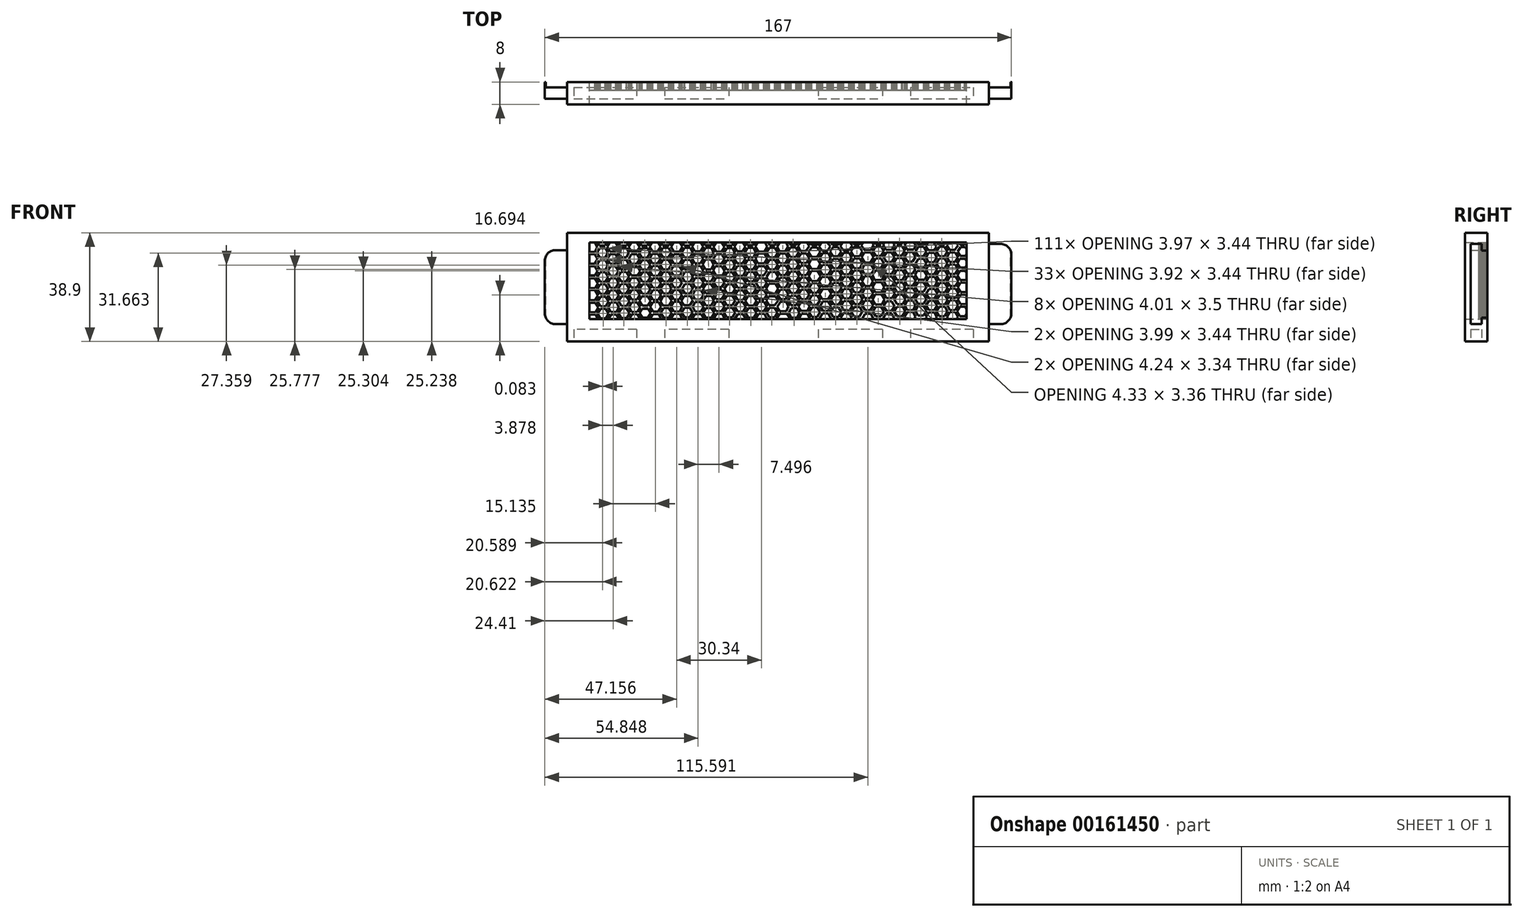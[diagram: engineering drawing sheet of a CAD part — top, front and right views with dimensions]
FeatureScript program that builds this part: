
annotation { "Feature Type Name" : "Feature", "Feature Type Description" : "" }
export const myFeature = defineFeature(function(context is Context, id is Id, definition is map)
    precondition{}
    {
        {
            var Q0;
            Q0=qCreatedBy(makeId("Front.planeOp"),FACE);
            var sketch = newSketch(context, id + "F0", { "sketchPlane" : qUnion([Q0])});
            skLineSegment(sketch, "E0.bottom", {"start": v(-77.72, 39.57) * mm, "end": v(73.28, 39.57) * mm});
            skLineSegment(sketch, "E0.top", {"start": v(-77.72, 0.67) * mm, "end": v(73.28, 0.67) * mm});
            skLineSegment(sketch, "E0.left", {"start": v(-77.72, 39.57) * mm, "end": v(-77.72, 0.67) * mm});
            skLineSegment(sketch, "E0.right", {"start": v(73.28, 39.57) * mm, "end": v(73.28, 0.67) * mm});
            skLineSegment(sketch, "E1.left", {"start": v(-77.72, 0.67) * mm, "end": v(-77.72, 15.56) * mm});
            skLineSegment(sketch, "E1.right", {"start": v(-85.72, 10.7) * mm, "end": v(-85.72, 29.54) * mm});
            skLineSegment(sketch, "E2.left", {"start": v(73.28, 39.57) * mm, "end": v(73.28, -23.35) * mm});
            skLineSegment(sketch, "E3.top", {"start": v(-77.72, 6.87) * mm, "end": v(-81.89, 6.87) * mm});
            skLineSegment(sketch, "E3.left", {"start": v(-77.72, 0.67) * mm, "end": v(-77.72, 6.87) * mm});
            skLineSegment(sketch, "E4.top", {"start": v(-81.89, 33.37) * mm, "end": v(-77.72, 33.37) * mm});
            skLineSegment(sketch, "E4.right", {"start": v(-77.72, 33.37) * mm, "end": v(-77.72, 15.56) * mm});
            skLineSegment(sketch, "E5.bottom", {"start": v(73.28, 6.87) * mm, "end": v(77.44, 6.87) * mm});
            skLineSegment(sketch, "E5.top", {"start": v(73.28, 35.57) * mm, "end": v(77.44, 35.57) * mm});
            skLineSegment(sketch, "E5.left", {"start": v(73.28, 6.87) * mm, "end": v(73.28, 35.57) * mm});
            skLineSegment(sketch, "E5.right", {"start": v(81.28, 10.7) * mm, "end": v(81.28, 31.74) * mm});
            skArc(sketch, "E6.filletArc", {"start": v(81.28, 31.74) * mm, "mid": v(80.15, 34.45) * mm, "end": v(77.44, 35.57) * mm});
            skPoint(sketch, "E7.visualSharp", {"position": v(81.28, 6.87) * mm});
            skArc(sketch, "E7.filletArc", {"start": v(77.44, 6.87) * mm, "mid": v(80.15, 8) * mm, "end": v(81.28, 10.7) * mm});
            skArc(sketch, "E8.filletArc", {"start": v(-81.89, 33.37) * mm, "mid": v(-84.6, 32.25) * mm, "end": v(-85.72, 29.54) * mm});
            skPoint(sketch, "E9.visualSharp", {"position": v(-85.72, 6.87) * mm});
            skArc(sketch, "E9.filletArc", {"start": v(-85.72, 10.7) * mm, "mid": v(-84.6, 8) * mm, "end": v(-81.89, 6.87) * mm});
            skLineSegment(sketch, "E10.bottom", {"start": v(-77.72, 39.57) * mm, "end": v(-69.72, 39.57) * mm});
            skLineSegment(sketch, "E10.top", {"start": v(-77.72, 0.67) * mm, "end": v(-69.72, 0.67) * mm});
            skLineSegment(sketch, "E10.right", {"start": v(-69.72, 36.1) * mm, "end": v(-69.72, 32.73) * mm});
            skLineSegment(sketch, "E11.bottom", {"start": v(73.28, 39.57) * mm, "end": v(65.28, 39.57) * mm});
            skLineSegment(sketch, "E11.top", {"start": v(73.28, 0.67) * mm, "end": v(65.28, 0.67) * mm});
            skLineSegment(sketch, "E11.right", {"start": v(65.28, 36.1) * mm, "end": v(65.28, 8.67) * mm});
            skLineSegment(sketch, "E12.bottom", {"start": v(-69.72, 8.67) * mm, "end": v(-61.72, 8.67) * mm});
            skLineSegment(sketch, "E12.left", {"start": v(-77.72, 8.67) * mm, "end": v(-77.72, 0.67) * mm});
            skLineSegment(sketch, "E12.right", {"start": v(73.28, 8.67) * mm, "end": v(73.28, 0.67) * mm});
            skLineSegment(sketch, "E13.top", {"start": v(-69.72, 36.1) * mm, "end": v(-61.72, 36.1) * mm});
            skLineSegment(sketch, "E13.left", {"start": v(-77.72, 39.57) * mm, "end": v(-77.72, 36.1) * mm});
            skLineSegment(sketch, "E13.right", {"start": v(73.28, 39.57) * mm, "end": v(73.28, 35.57) * mm});
            skLineSegment(sketch, "E14.bottom", {"start": v(-36.72, 36.1) * mm, "end": v(-28.72, 36.1) * mm});
            skLineSegment(sketch, "E14.top", {"start": v(-36.57, 8.67) * mm, "end": v(-28.72, 8.67) * mm});
            skLineSegment(sketch, "E15.bottom", {"start": v(-25.72, 36.1) * mm, "end": v(-17.72, 36.1) * mm});
            skLineSegment(sketch, "E15.top", {"start": v(-25.72, 8.67) * mm, "end": v(-17.72, 8.67) * mm});
            skLineSegment(sketch, "E16.bottom", {"start": v(32.28, 36.1) * mm, "end": v(35.28, 36.1) * mm});
            skLineSegment(sketch, "E17.right", {"start": v(73.28, 11.56) * mm, "end": v(73.28, 8.67) * mm});
            skLineSegment(sketch, "E18.trimOffspring", {"start": v(13.28, 8.67) * mm, "end": v(17.28, 8.67) * mm});
            skLineSegment(sketch, "E19.trimOffspring", {"start": v(24.28, 8.67) * mm, "end": v(32.28, 8.67) * mm});
            skLineSegment(sketch, "E20.trimOffspring", {"start": v(35.28, 8.67) * mm, "end": v(43.28, 8.67) * mm});
            skLineSegment(sketch, "E21.trimOffspring", {"start": v(57.28, 8.67) * mm, "end": v(65.28, 8.67) * mm});
            skLineSegment(sketch, "E22.trimOffspring", {"start": v(24.28, 36.1) * mm, "end": v(32.28, 36.1) * mm});
            skLineSegment(sketch, "E23.trimOffspring", {"start": v(35.28, 36.1) * mm, "end": v(43.28, 36.1) * mm});
            skLineSegment(sketch, "E24.trimOffspring", {"start": v(46.28, 36.1) * mm, "end": v(54.28, 36.1) * mm});
            skLineSegment(sketch, "E25.trimOffspring", {"start": v(-47.72, 36.1) * mm, "end": v(-39.72, 36.1) * mm});
            skLineSegment(sketch, "E26.trimOffspring", {"start": v(-58.72, 8.67) * mm, "end": v(-50.72, 8.67) * mm});
            skLineSegment(sketch, "E27.trimOffspring", {"start": v(-58.72, 36.1) * mm, "end": v(-50.72, 36.1) * mm});
            skLineSegment(sketch, "E28.trimOffspring", {"start": v(-47.72, 8.67) * mm, "end": v(-40.46, 8.67) * mm});
            skLineSegment(sketch, "E29.trimOffspring", {"start": v(-25.48, 36.1) * mm, "end": v(-18.05, 36.1) * mm});
            skLineSegment(sketch, "E30.trimOffspring", {"start": v(57.28, 36.1) * mm, "end": v(65.28, 36.1) * mm});
            skLineSegment(sketch, "E31.trimOffspring", {"start": v(46.28, 8.67) * mm, "end": v(54.28, 8.67) * mm});
            skLineSegment(sketch, "E32", {"start": v(80.98, 9.22) * mm, "end": v(80.98, 33.23) * mm});
            skLineSegment(sketch, "E33", {"start": v(-85.42, 9.22) * mm, "end": v(-85.42, 31.03) * mm});
            skLineSegment(sketch, "E34", {"start": v(7.51, 8.67) * mm, "end": v(-11.96, 8.67) * mm});
            skLineSegment(sketch, "E35", {"start": v(65.28, 8.67) * mm, "end": v(-44.09, 8.67) * mm});
            skLineSegment(sketch, "E36", {"start": v(-69.72, 36.1) * mm, "end": v(-58.72, 36.1) * mm});
            skLineSegment(sketch, "E37.0", {"start": v(-60.4, 28.54) * mm, "end": v(-62.38, 28.54) * mm});
            skLineSegment(sketch, "E37.1", {"start": v(-62.38, 28.54) * mm, "end": v(-63.37, 30.26) * mm});
            skLineSegment(sketch, "E37.2", {"start": v(-63.37, 30.26) * mm, "end": v(-62.38, 31.98) * mm});
            skLineSegment(sketch, "E37.3", {"start": v(-62.38, 31.98) * mm, "end": v(-60.4, 31.98) * mm});
            skLineSegment(sketch, "E37.4", {"start": v(-60.4, 31.98) * mm, "end": v(-59.4, 30.26) * mm});
            skLineSegment(sketch, "E37.5", {"start": v(-59.4, 30.26) * mm, "end": v(-60.4, 28.54) * mm});
            skLineSegment(sketch, "E38.trimOffspring", {"start": v(-47.72, 36.1) * mm, "end": v(-14.8, 36.1) * mm});
            skLineSegment(sketch, "E39", {"start": v(-63.17, 32.36) * mm, "end": v(-64.18, 30.61) * mm});
            skLineSegment(sketch, "E40", {"start": v(-62.32, 27.66) * mm, "end": v(-60.32, 27.66) * mm});
            skLineSegment(sketch, "E41", {"start": v(-47.72, 36.1) * mm, "end": v(-50.72, 36.1) * mm});
            skLineSegment(sketch, "E42.0", {"start": v(-60.4, 32.84) * mm, "end": v(-62.39, 32.84) * mm});
            skLineSegment(sketch, "E42.1", {"start": v(-62.39, 32.84) * mm, "end": v(-63.38, 34.56) * mm});
            skLineSegment(sketch, "E42.2", {"start": v(-63.38, 34.56) * mm, "end": v(-62.5, 36.1) * mm});
            skLineSegment(sketch, "E42.4", {"start": v(-60.3, 36.1) * mm, "end": v(-59.41, 34.56) * mm});
            skLineSegment(sketch, "E42.5", {"start": v(-59.41, 34.56) * mm, "end": v(-60.4, 32.84) * mm});
            skLineSegment(sketch, "E43", {"start": v(-63.5, 36.1) * mm, "end": v(-64.19, 34.92) * mm});
            skLineSegment(sketch, "E44", {"start": v(-59.3, 36.1) * mm, "end": v(-58.68, 35.02) * mm});
            skLineSegment(sketch, "E45.0", {"start": v(-56.6, 26.42) * mm, "end": v(-58.6, 26.42) * mm});
            skLineSegment(sketch, "E45.1", {"start": v(-58.6, 26.42) * mm, "end": v(-59.59, 28.14) * mm});
            skLineSegment(sketch, "E45.2", {"start": v(-59.59, 28.14) * mm, "end": v(-58.6, 29.85) * mm});
            skLineSegment(sketch, "E45.3", {"start": v(-58.6, 29.85) * mm, "end": v(-56.6, 29.85) * mm});
            skLineSegment(sketch, "E45.4", {"start": v(-56.6, 29.85) * mm, "end": v(-55.62, 28.14) * mm});
            skLineSegment(sketch, "E45.5", {"start": v(-55.62, 28.14) * mm, "end": v(-56.6, 26.42) * mm});
            skLineSegment(sketch, "E46", {"start": v(-60.32, 27.66) * mm, "end": v(-59.3, 25.9) * mm});
            skLineSegment(sketch, "E47", {"start": v(-54.93, 27.59) * mm, "end": v(-55.82, 26.02) * mm});
            skLineSegment(sketch, "E48.0", {"start": v(-56.62, 30.72) * mm, "end": v(-58.6, 30.72) * mm});
            skLineSegment(sketch, "E48.1", {"start": v(-58.6, 30.72) * mm, "end": v(-59.6, 32.44) * mm});
            skLineSegment(sketch, "E48.2", {"start": v(-59.6, 32.44) * mm, "end": v(-58.6, 34.16) * mm});
            skLineSegment(sketch, "E48.3", {"start": v(-58.6, 34.16) * mm, "end": v(-56.62, 34.16) * mm});
            skLineSegment(sketch, "E48.4", {"start": v(-56.62, 34.16) * mm, "end": v(-55.63, 32.44) * mm});
            skLineSegment(sketch, "E48.5", {"start": v(-55.63, 32.44) * mm, "end": v(-56.62, 30.72) * mm});
            skLineSegment(sketch, "E49", {"start": v(-56.45, 35.02) * mm, "end": v(-58.68, 35.02) * mm});
            skLineSegment(sketch, "E50.0", {"start": v(-67.9, 28.43) * mm, "end": v(-69.72, 28.43) * mm});
            skLineSegment(sketch, "E50.3", {"start": v(-69.72, 31.87) * mm, "end": v(-67.9, 31.87) * mm});
            skLineSegment(sketch, "E50.4", {"start": v(-67.9, 31.87) * mm, "end": v(-66.9, 30.15) * mm});
            skLineSegment(sketch, "E50.5", {"start": v(-66.9, 30.15) * mm, "end": v(-67.9, 28.43) * mm});
            skLineSegment(sketch, "E51", {"start": v(-69.72, 27.55) * mm, "end": v(-67.82, 27.55) * mm});
            skLineSegment(sketch, "E52.0", {"start": v(-67.9, 32.73) * mm, "end": v(-69.72, 32.73) * mm});
            skLineSegment(sketch, "E52.4", {"start": v(-67.86, 36.1) * mm, "end": v(-66.9, 34.45) * mm});
            skLineSegment(sketch, "E52.5", {"start": v(-66.9, 34.45) * mm, "end": v(-67.9, 32.73) * mm});
            skLineSegment(sketch, "E53", {"start": v(-66.86, 36.1) * mm, "end": v(-66.18, 34.92) * mm});
            skLineSegment(sketch, "E54.0", {"start": v(-64.1, 26.31) * mm, "end": v(-66.09, 26.31) * mm});
            skLineSegment(sketch, "E54.1", {"start": v(-66.09, 26.31) * mm, "end": v(-67.08, 28.03) * mm});
            skLineSegment(sketch, "E54.2", {"start": v(-67.08, 28.03) * mm, "end": v(-66.1, 29.75) * mm});
            skLineSegment(sketch, "E54.3", {"start": v(-66.1, 29.75) * mm, "end": v(-64.1, 29.75) * mm});
            skLineSegment(sketch, "E54.4", {"start": v(-64.1, 29.75) * mm, "end": v(-63.11, 28.03) * mm});
            skLineSegment(sketch, "E54.5", {"start": v(-63.11, 28.03) * mm, "end": v(-64.1, 26.31) * mm});
            skLineSegment(sketch, "E55", {"start": v(-67.82, 27.55) * mm, "end": v(-66.8, 25.8) * mm});
            skLineSegment(sketch, "E56", {"start": v(-62.32, 27.66) * mm, "end": v(-63.31, 25.92) * mm});
            skLineSegment(sketch, "E57.0", {"start": v(-64.18, 30.61) * mm, "end": v(-66.1, 30.61) * mm});
            skLineSegment(sketch, "E57.1", {"start": v(-66.1, 30.61) * mm, "end": v(-67.1, 32.33) * mm});
            skLineSegment(sketch, "E57.2", {"start": v(-67.1, 32.33) * mm, "end": v(-66.1, 34.05) * mm});
            skLineSegment(sketch, "E57.3", {"start": v(-66.1, 34.05) * mm, "end": v(-64.11, 34.05) * mm});
            skLineSegment(sketch, "E57.4", {"start": v(-64.11, 34.05) * mm, "end": v(-63.17, 32.36) * mm});
            skLineSegment(sketch, "E58", {"start": v(-64.19, 34.92) * mm, "end": v(-66.18, 34.92) * mm});
            skLineSegment(sketch, "E59.0", {"start": v(-56.52, 17.78) * mm, "end": v(-58.5, 17.78) * mm});
            skLineSegment(sketch, "E59.1", {"start": v(-58.5, 17.78) * mm, "end": v(-59.5, 19.5) * mm});
            skLineSegment(sketch, "E59.2", {"start": v(-59.5, 19.5) * mm, "end": v(-58.5, 21.22) * mm});
            skLineSegment(sketch, "E59.3", {"start": v(-58.5, 21.22) * mm, "end": v(-56.52, 21.22) * mm});
            skLineSegment(sketch, "E59.4", {"start": v(-56.52, 21.22) * mm, "end": v(-55.53, 19.5) * mm});
            skLineSegment(sketch, "E59.5", {"start": v(-55.53, 19.5) * mm, "end": v(-56.52, 17.78) * mm});
            skLineSegment(sketch, "E60", {"start": v(-59.3, 21.6) * mm, "end": v(-60.3, 19.85) * mm});
            skLineSegment(sketch, "E61.0", {"start": v(-56.53, 22.08) * mm, "end": v(-58.51, 22.08) * mm});
            skLineSegment(sketch, "E61.1", {"start": v(-58.51, 22.08) * mm, "end": v(-59.5, 23.8) * mm});
            skLineSegment(sketch, "E61.2", {"start": v(-59.5, 23.8) * mm, "end": v(-58.51, 25.52) * mm});
            skLineSegment(sketch, "E61.3", {"start": v(-58.51, 25.52) * mm, "end": v(-56.53, 25.52) * mm});
            skLineSegment(sketch, "E61.4", {"start": v(-56.53, 25.52) * mm, "end": v(-55.53, 23.8) * mm});
            skLineSegment(sketch, "E61.5", {"start": v(-55.53, 23.8) * mm, "end": v(-56.53, 22.08) * mm});
            skLineSegment(sketch, "E62", {"start": v(-59.3, 25.9) * mm, "end": v(-60.3, 24.16) * mm});
            skLineSegment(sketch, "E63", {"start": v(-55.82, 26.02) * mm, "end": v(-54.8, 24.26) * mm});
            skLineSegment(sketch, "E64.0", {"start": v(-52.73, 15.66) * mm, "end": v(-54.72, 15.66) * mm});
            skLineSegment(sketch, "E64.1", {"start": v(-54.72, 15.66) * mm, "end": v(-55.7, 17.38) * mm});
            skLineSegment(sketch, "E64.2", {"start": v(-55.7, 17.38) * mm, "end": v(-54.72, 19.1) * mm});
            skLineSegment(sketch, "E64.3", {"start": v(-54.72, 19.1) * mm, "end": v(-52.73, 19.1) * mm});
            skLineSegment(sketch, "E64.4", {"start": v(-52.73, 19.1) * mm, "end": v(-51.74, 17.38) * mm});
            skLineSegment(sketch, "E64.5", {"start": v(-51.74, 17.38) * mm, "end": v(-52.73, 15.66) * mm});
            skLineSegment(sketch, "E65", {"start": v(-56.4, 16.82) * mm, "end": v(-55.4, 15.1) * mm});
            skLineSegment(sketch, "E66", {"start": v(-51.05, 16.83) * mm, "end": v(-51.94, 15.27) * mm});
            skLineSegment(sketch, "E67.0", {"start": v(-52.74, 19.96) * mm, "end": v(-54.72, 19.96) * mm});
            skLineSegment(sketch, "E67.1", {"start": v(-54.72, 19.96) * mm, "end": v(-55.72, 21.68) * mm});
            skLineSegment(sketch, "E67.2", {"start": v(-55.72, 21.68) * mm, "end": v(-54.73, 23.4) * mm});
            skLineSegment(sketch, "E67.3", {"start": v(-54.73, 23.4) * mm, "end": v(-52.74, 23.4) * mm});
            skLineSegment(sketch, "E67.4", {"start": v(-52.74, 23.4) * mm, "end": v(-51.75, 21.68) * mm});
            skLineSegment(sketch, "E67.5", {"start": v(-51.75, 21.68) * mm, "end": v(-52.74, 19.96) * mm});
            skLineSegment(sketch, "E68", {"start": v(-52.57, 24.26) * mm, "end": v(-54.8, 24.26) * mm});
            skLineSegment(sketch, "E69", {"start": v(-54.72, 19.08) * mm, "end": v(-52.72, 19.08) * mm});
            skLineSegment(sketch, "E70.0", {"start": v(-64.01, 17.67) * mm, "end": v(-66, 17.67) * mm});
            skLineSegment(sketch, "E70.1", {"start": v(-66, 17.67) * mm, "end": v(-67, 19.4) * mm});
            skLineSegment(sketch, "E70.2", {"start": v(-67, 19.4) * mm, "end": v(-66, 21.1) * mm});
            skLineSegment(sketch, "E70.3", {"start": v(-66, 21.1) * mm, "end": v(-64.02, 21.1) * mm});
            skLineSegment(sketch, "E70.4", {"start": v(-64.02, 21.1) * mm, "end": v(-63.02, 19.4) * mm});
            skLineSegment(sketch, "E70.5", {"start": v(-63.02, 19.4) * mm, "end": v(-64.01, 17.67) * mm});
            skLineSegment(sketch, "E71", {"start": v(-66.77, 21.54) * mm, "end": v(-67.78, 19.78) * mm});
            skLineSegment(sketch, "E72", {"start": v(-67.8, 19.04) * mm, "end": v(-66.67, 17.09) * mm});
            skLineSegment(sketch, "E73.0", {"start": v(-64.02, 21.98) * mm, "end": v(-66, 21.98) * mm});
            skLineSegment(sketch, "E73.1", {"start": v(-66, 21.98) * mm, "end": v(-67, 23.7) * mm});
            skLineSegment(sketch, "E73.2", {"start": v(-67, 23.7) * mm, "end": v(-66, 25.41) * mm});
            skLineSegment(sketch, "E73.3", {"start": v(-66, 25.41) * mm, "end": v(-64.02, 25.41) * mm});
            skLineSegment(sketch, "E73.4", {"start": v(-64.02, 25.41) * mm, "end": v(-63.03, 23.7) * mm});
            skLineSegment(sketch, "E73.5", {"start": v(-63.03, 23.7) * mm, "end": v(-64.02, 21.98) * mm});
            skLineSegment(sketch, "E74", {"start": v(-66.8, 25.8) * mm, "end": v(-67.69, 24.25) * mm});
            skLineSegment(sketch, "E75", {"start": v(-67.8, 23.33) * mm, "end": v(-66.77, 21.54) * mm});
            skLineSegment(sketch, "E76", {"start": v(-63.31, 25.92) * mm, "end": v(-62.3, 24.16) * mm});
            skLineSegment(sketch, "E77.0", {"start": v(-60.23, 15.55) * mm, "end": v(-62.21, 15.55) * mm});
            skLineSegment(sketch, "E77.1", {"start": v(-62.21, 15.55) * mm, "end": v(-63.2, 17.27) * mm});
            skLineSegment(sketch, "E77.2", {"start": v(-63.2, 17.27) * mm, "end": v(-62.21, 18.99) * mm});
            skLineSegment(sketch, "E77.3", {"start": v(-62.21, 18.99) * mm, "end": v(-60.23, 18.99) * mm});
            skLineSegment(sketch, "E77.4", {"start": v(-60.23, 18.99) * mm, "end": v(-59.24, 17.27) * mm});
            skLineSegment(sketch, "E77.5", {"start": v(-59.24, 17.27) * mm, "end": v(-60.23, 15.55) * mm});
            skLineSegment(sketch, "E78.0", {"start": v(-60.3, 19.85) * mm, "end": v(-62.22, 19.85) * mm});
            skLineSegment(sketch, "E78.1", {"start": v(-62.22, 19.85) * mm, "end": v(-63.21, 21.57) * mm});
            skLineSegment(sketch, "E78.2", {"start": v(-63.21, 21.57) * mm, "end": v(-62.22, 23.3) * mm});
            skLineSegment(sketch, "E78.3", {"start": v(-62.22, 23.3) * mm, "end": v(-60.24, 23.3) * mm});
            skLineSegment(sketch, "E78.4", {"start": v(-60.24, 23.3) * mm, "end": v(-59.3, 21.6) * mm});
            skLineSegment(sketch, "E79", {"start": v(-60.3, 24.16) * mm, "end": v(-62.3, 24.16) * mm});
            skLineSegment(sketch, "E80.0", {"start": v(-45.26, 28.58) * mm, "end": v(-47.24, 28.58) * mm});
            skLineSegment(sketch, "E80.1", {"start": v(-47.24, 28.58) * mm, "end": v(-48.24, 30.3) * mm});
            skLineSegment(sketch, "E80.2", {"start": v(-48.24, 30.3) * mm, "end": v(-47.25, 32.01) * mm});
            skLineSegment(sketch, "E80.3", {"start": v(-47.25, 32.01) * mm, "end": v(-45.26, 32.01) * mm});
            skLineSegment(sketch, "E80.4", {"start": v(-45.26, 32.01) * mm, "end": v(-44.27, 30.3) * mm});
            skLineSegment(sketch, "E80.5", {"start": v(-44.27, 30.3) * mm, "end": v(-45.26, 28.58) * mm});
            skLineSegment(sketch, "E81", {"start": v(-48.04, 32.4) * mm, "end": v(-49.04, 30.65) * mm});
            skLineSegment(sketch, "E82", {"start": v(-47.19, 27.7) * mm, "end": v(-45.19, 27.7) * mm});
            skLineSegment(sketch, "E83.0", {"start": v(-45.27, 32.88) * mm, "end": v(-47.25, 32.88) * mm});
            skLineSegment(sketch, "E83.1", {"start": v(-47.25, 32.88) * mm, "end": v(-48.25, 34.6) * mm});
            skLineSegment(sketch, "E83.2", {"start": v(-48.25, 34.6) * mm, "end": v(-47.38, 36.1) * mm});
            skLineSegment(sketch, "E83.4", {"start": v(-45.15, 36.1) * mm, "end": v(-44.28, 34.6) * mm});
            skLineSegment(sketch, "E83.5", {"start": v(-44.28, 34.6) * mm, "end": v(-45.27, 32.88) * mm});
            skLineSegment(sketch, "E84", {"start": v(-48.4, 36.1) * mm, "end": v(-49.05, 34.95) * mm});
            skLineSegment(sketch, "E85", {"start": v(-44.14, 36.1) * mm, "end": v(-43.54, 35.06) * mm});
            skLineSegment(sketch, "E86.0", {"start": v(-41.47, 26.45) * mm, "end": v(-43.46, 26.45) * mm});
            skLineSegment(sketch, "E86.1", {"start": v(-43.46, 26.45) * mm, "end": v(-44.45, 28.17) * mm});
            skLineSegment(sketch, "E86.2", {"start": v(-44.45, 28.17) * mm, "end": v(-43.46, 29.9) * mm});
            skLineSegment(sketch, "E86.3", {"start": v(-43.46, 29.9) * mm, "end": v(-41.47, 29.9) * mm});
            skLineSegment(sketch, "E86.4", {"start": v(-41.47, 29.9) * mm, "end": v(-40.48, 28.17) * mm});
            skLineSegment(sketch, "E86.5", {"start": v(-40.48, 28.17) * mm, "end": v(-41.47, 26.45) * mm});
            skLineSegment(sketch, "E87", {"start": v(-45.19, 27.7) * mm, "end": v(-44.17, 25.94) * mm});
            skLineSegment(sketch, "E88", {"start": v(-39.78, 27.65) * mm, "end": v(-40.68, 26.06) * mm});
            skLineSegment(sketch, "E89.0", {"start": v(-41.48, 30.76) * mm, "end": v(-43.47, 30.76) * mm});
            skLineSegment(sketch, "E89.1", {"start": v(-43.47, 30.76) * mm, "end": v(-44.46, 32.48) * mm});
            skLineSegment(sketch, "E89.2", {"start": v(-44.46, 32.48) * mm, "end": v(-43.47, 34.2) * mm});
            skLineSegment(sketch, "E89.3", {"start": v(-43.47, 34.2) * mm, "end": v(-41.48, 34.2) * mm});
            skLineSegment(sketch, "E89.4", {"start": v(-41.48, 34.2) * mm, "end": v(-40.5, 32.48) * mm});
            skLineSegment(sketch, "E89.5", {"start": v(-40.5, 32.48) * mm, "end": v(-41.48, 30.76) * mm});
            skLineSegment(sketch, "E90", {"start": v(-41.24, 35.06) * mm, "end": v(-43.54, 35.06) * mm});
            skLineSegment(sketch, "E91", {"start": v(-43.47, 29.88) * mm, "end": v(-41.47, 29.88) * mm});
            skLineSegment(sketch, "E92.0", {"start": v(-52.76, 28.47) * mm, "end": v(-54.74, 28.47) * mm});
            skLineSegment(sketch, "E92.1", {"start": v(-54.74, 28.47) * mm, "end": v(-55.73, 30.19) * mm});
            skLineSegment(sketch, "E92.2", {"start": v(-55.73, 30.19) * mm, "end": v(-54.74, 31.9) * mm});
            skLineSegment(sketch, "E92.3", {"start": v(-54.74, 31.9) * mm, "end": v(-52.76, 31.9) * mm});
            skLineSegment(sketch, "E92.4", {"start": v(-52.76, 31.9) * mm, "end": v(-51.76, 30.19) * mm});
            skLineSegment(sketch, "E92.5", {"start": v(-51.76, 30.19) * mm, "end": v(-52.76, 28.47) * mm});
            skLineSegment(sketch, "E93", {"start": v(-54.93, 27.59) * mm, "end": v(-52.68, 27.59) * mm});
            skLineSegment(sketch, "E94.0", {"start": v(-52.77, 32.77) * mm, "end": v(-54.75, 32.77) * mm});
            skLineSegment(sketch, "E94.1", {"start": v(-54.75, 32.77) * mm, "end": v(-55.74, 34.5) * mm});
            skLineSegment(sketch, "E94.2", {"start": v(-55.74, 34.5) * mm, "end": v(-54.81, 36.1) * mm});
            skLineSegment(sketch, "E94.4", {"start": v(-52.7, 36.1) * mm, "end": v(-51.77, 34.5) * mm});
            skLineSegment(sketch, "E94.5", {"start": v(-51.77, 34.5) * mm, "end": v(-52.77, 32.77) * mm});
            skLineSegment(sketch, "E95", {"start": v(-55.83, 36.1) * mm, "end": v(-56.45, 35.02) * mm});
            skLineSegment(sketch, "E96", {"start": v(-51.7, 36.1) * mm, "end": v(-51.04, 34.95) * mm});
            skLineSegment(sketch, "E97.0", {"start": v(-48.97, 26.35) * mm, "end": v(-50.95, 26.35) * mm});
            skLineSegment(sketch, "E97.1", {"start": v(-50.95, 26.35) * mm, "end": v(-51.95, 28.07) * mm});
            skLineSegment(sketch, "E97.2", {"start": v(-51.95, 28.07) * mm, "end": v(-50.96, 29.79) * mm});
            skLineSegment(sketch, "E97.3", {"start": v(-50.96, 29.79) * mm, "end": v(-48.97, 29.79) * mm});
            skLineSegment(sketch, "E97.4", {"start": v(-48.97, 29.79) * mm, "end": v(-47.98, 28.07) * mm});
            skLineSegment(sketch, "E97.5", {"start": v(-47.98, 28.07) * mm, "end": v(-48.97, 26.35) * mm});
            skLineSegment(sketch, "E98", {"start": v(-52.68, 27.59) * mm, "end": v(-51.67, 25.83) * mm});
            skLineSegment(sketch, "E99", {"start": v(-47.19, 27.7) * mm, "end": v(-48.18, 25.96) * mm});
            skLineSegment(sketch, "E100.0", {"start": v(-49.04, 30.65) * mm, "end": v(-50.96, 30.65) * mm});
            skLineSegment(sketch, "E100.1", {"start": v(-50.96, 30.65) * mm, "end": v(-51.96, 32.37) * mm});
            skLineSegment(sketch, "E100.2", {"start": v(-51.96, 32.37) * mm, "end": v(-50.96, 34.09) * mm});
            skLineSegment(sketch, "E100.3", {"start": v(-50.96, 34.09) * mm, "end": v(-48.98, 34.09) * mm});
            skLineSegment(sketch, "E100.4", {"start": v(-48.98, 34.09) * mm, "end": v(-48.04, 32.4) * mm});
            skLineSegment(sketch, "E101", {"start": v(-49.05, 34.95) * mm, "end": v(-51.04, 34.95) * mm});
            skLineSegment(sketch, "E102", {"start": v(-50.96, 29.77) * mm, "end": v(-48.96, 29.77) * mm});
            skLineSegment(sketch, "E103.0", {"start": v(-41.38, 17.82) * mm, "end": v(-43.37, 17.82) * mm});
            skLineSegment(sketch, "E103.1", {"start": v(-43.37, 17.82) * mm, "end": v(-44.36, 19.53) * mm});
            skLineSegment(sketch, "E103.2", {"start": v(-44.36, 19.53) * mm, "end": v(-43.37, 21.25) * mm});
            skLineSegment(sketch, "E103.3", {"start": v(-43.37, 21.25) * mm, "end": v(-41.38, 21.25) * mm});
            skLineSegment(sketch, "E103.4", {"start": v(-41.38, 21.25) * mm, "end": v(-40.4, 19.53) * mm});
            skLineSegment(sketch, "E103.5", {"start": v(-40.4, 19.53) * mm, "end": v(-41.38, 17.82) * mm});
            skLineSegment(sketch, "E104", {"start": v(-44.16, 21.64) * mm, "end": v(-45.17, 19.9) * mm});
            skLineSegment(sketch, "E105", {"start": v(-43.31, 16.94) * mm, "end": v(-41.3, 16.94) * mm});
            skLineSegment(sketch, "E106.0", {"start": v(-41.4, 22.12) * mm, "end": v(-43.38, 22.12) * mm});
            skLineSegment(sketch, "E106.1", {"start": v(-43.38, 22.12) * mm, "end": v(-44.37, 23.84) * mm});
            skLineSegment(sketch, "E106.2", {"start": v(-44.37, 23.84) * mm, "end": v(-43.38, 25.56) * mm});
            skLineSegment(sketch, "E106.3", {"start": v(-43.38, 25.56) * mm, "end": v(-41.4, 25.56) * mm});
            skLineSegment(sketch, "E106.4", {"start": v(-41.4, 25.56) * mm, "end": v(-40.4, 23.84) * mm});
            skLineSegment(sketch, "E106.5", {"start": v(-40.4, 23.84) * mm, "end": v(-41.4, 22.12) * mm});
            skLineSegment(sketch, "E107", {"start": v(-44.17, 25.94) * mm, "end": v(-45.17, 24.2) * mm});
            skLineSegment(sketch, "E108", {"start": v(-40.68, 26.06) * mm, "end": v(-39.67, 24.3) * mm});
            skLineSegment(sketch, "E109.0", {"start": v(-37.6, 15.7) * mm, "end": v(-39.58, 15.7) * mm});
            skLineSegment(sketch, "E109.1", {"start": v(-39.58, 15.7) * mm, "end": v(-40.57, 17.41) * mm});
            skLineSegment(sketch, "E109.2", {"start": v(-40.57, 17.41) * mm, "end": v(-39.58, 19.13) * mm});
            skLineSegment(sketch, "E109.3", {"start": v(-39.58, 19.13) * mm, "end": v(-37.6, 19.13) * mm});
            skLineSegment(sketch, "E109.4", {"start": v(-37.6, 19.13) * mm, "end": v(-36.6, 17.41) * mm});
            skLineSegment(sketch, "E109.5", {"start": v(-36.6, 17.41) * mm, "end": v(-37.6, 15.7) * mm});
            skLineSegment(sketch, "E110", {"start": v(-41.3, 16.94) * mm, "end": v(-40.33, 15.25) * mm});
            skLineSegment(sketch, "E111", {"start": v(-35.9, 16.89) * mm, "end": v(-36.9, 15.14) * mm});
            skLineSegment(sketch, "E112.0", {"start": v(-37.6, 20) * mm, "end": v(-39.59, 20) * mm});
            skLineSegment(sketch, "E112.1", {"start": v(-39.59, 20) * mm, "end": v(-40.58, 21.72) * mm});
            skLineSegment(sketch, "E112.2", {"start": v(-40.58, 21.72) * mm, "end": v(-39.6, 23.44) * mm});
            skLineSegment(sketch, "E112.3", {"start": v(-39.6, 23.44) * mm, "end": v(-37.6, 23.44) * mm});
            skLineSegment(sketch, "E112.4", {"start": v(-37.6, 23.44) * mm, "end": v(-36.61, 21.72) * mm});
            skLineSegment(sketch, "E112.5", {"start": v(-36.61, 21.72) * mm, "end": v(-37.6, 20) * mm});
            skLineSegment(sketch, "E113", {"start": v(-37.36, 24.3) * mm, "end": v(-39.67, 24.3) * mm});
            skLineSegment(sketch, "E114.0", {"start": v(-48.88, 17.7) * mm, "end": v(-50.86, 17.7) * mm});
            skLineSegment(sketch, "E114.1", {"start": v(-50.86, 17.7) * mm, "end": v(-51.86, 19.43) * mm});
            skLineSegment(sketch, "E114.2", {"start": v(-51.86, 19.43) * mm, "end": v(-50.86, 21.15) * mm});
            skLineSegment(sketch, "E114.3", {"start": v(-50.86, 21.15) * mm, "end": v(-48.88, 21.15) * mm});
            skLineSegment(sketch, "E114.4", {"start": v(-48.88, 21.15) * mm, "end": v(-47.89, 19.43) * mm});
            skLineSegment(sketch, "E114.5", {"start": v(-47.89, 19.43) * mm, "end": v(-48.88, 17.7) * mm});
            skLineSegment(sketch, "E115", {"start": v(-51.05, 16.83) * mm, "end": v(-48.8, 16.83) * mm});
            skLineSegment(sketch, "E116.0", {"start": v(-48.89, 22.01) * mm, "end": v(-50.87, 22.01) * mm});
            skLineSegment(sketch, "E116.1", {"start": v(-50.87, 22.01) * mm, "end": v(-51.86, 23.73) * mm});
            skLineSegment(sketch, "E116.2", {"start": v(-51.86, 23.73) * mm, "end": v(-50.87, 25.45) * mm});
            skLineSegment(sketch, "E116.3", {"start": v(-50.87, 25.45) * mm, "end": v(-48.89, 25.45) * mm});
            skLineSegment(sketch, "E116.4", {"start": v(-48.89, 25.45) * mm, "end": v(-47.9, 23.73) * mm});
            skLineSegment(sketch, "E116.5", {"start": v(-47.9, 23.73) * mm, "end": v(-48.89, 22.01) * mm});
            skLineSegment(sketch, "E117", {"start": v(-51.67, 25.83) * mm, "end": v(-52.57, 24.26) * mm});
            skLineSegment(sketch, "E118", {"start": v(-48.18, 25.96) * mm, "end": v(-47.16, 24.2) * mm});
            skLineSegment(sketch, "E119.0", {"start": v(-45.1, 15.59) * mm, "end": v(-47.08, 15.59) * mm});
            skLineSegment(sketch, "E119.1", {"start": v(-47.08, 15.59) * mm, "end": v(-48.07, 17.3) * mm});
            skLineSegment(sketch, "E119.2", {"start": v(-48.07, 17.3) * mm, "end": v(-47.08, 19.03) * mm});
            skLineSegment(sketch, "E119.3", {"start": v(-47.08, 19.03) * mm, "end": v(-45.1, 19.03) * mm});
            skLineSegment(sketch, "E119.4", {"start": v(-45.1, 19.03) * mm, "end": v(-44.1, 17.3) * mm});
            skLineSegment(sketch, "E119.5", {"start": v(-44.1, 17.3) * mm, "end": v(-45.1, 15.59) * mm});
            skLineSegment(sketch, "E120", {"start": v(-48.8, 16.83) * mm, "end": v(-47.83, 15.14) * mm});
            skLineSegment(sketch, "E121", {"start": v(-47.07, 14.7) * mm, "end": v(-45.06, 14.7) * mm});
            skLineSegment(sketch, "E122", {"start": v(-43.31, 16.94) * mm, "end": v(-44.37, 15.07) * mm});
            skLineSegment(sketch, "E123.0", {"start": v(-45.17, 19.9) * mm, "end": v(-47.09, 19.9) * mm});
            skLineSegment(sketch, "E123.1", {"start": v(-47.09, 19.9) * mm, "end": v(-48.08, 21.61) * mm});
            skLineSegment(sketch, "E123.2", {"start": v(-48.08, 21.61) * mm, "end": v(-47.09, 23.33) * mm});
            skLineSegment(sketch, "E123.3", {"start": v(-47.09, 23.33) * mm, "end": v(-45.1, 23.33) * mm});
            skLineSegment(sketch, "E123.4", {"start": v(-45.1, 23.33) * mm, "end": v(-44.16, 21.64) * mm});
            skLineSegment(sketch, "E124", {"start": v(-45.17, 24.2) * mm, "end": v(-47.16, 24.2) * mm});
            skLineSegment(sketch, "E125.0", {"start": v(-56.39, 9.08) * mm, "end": v(-58.37, 9.08) * mm});
            skLineSegment(sketch, "E125.1", {"start": v(-58.37, 9.08) * mm, "end": v(-59.37, 10.8) * mm});
            skLineSegment(sketch, "E125.2", {"start": v(-59.37, 10.8) * mm, "end": v(-58.37, 12.52) * mm});
            skLineSegment(sketch, "E125.3", {"start": v(-58.37, 12.52) * mm, "end": v(-56.39, 12.52) * mm});
            skLineSegment(sketch, "E125.4", {"start": v(-56.39, 12.52) * mm, "end": v(-55.4, 10.8) * mm});
            skLineSegment(sketch, "E125.5", {"start": v(-55.4, 10.8) * mm, "end": v(-56.39, 9.08) * mm});
            skLineSegment(sketch, "E126", {"start": v(-59.16, 12.9) * mm, "end": v(-60.17, 11.16) * mm});
            skLineSegment(sketch, "E127.0", {"start": v(-56.4, 13.38) * mm, "end": v(-58.38, 13.38) * mm});
            skLineSegment(sketch, "E127.1", {"start": v(-58.38, 13.38) * mm, "end": v(-59.37, 15.1) * mm});
            skLineSegment(sketch, "E127.2", {"start": v(-59.37, 15.1) * mm, "end": v(-58.38, 16.82) * mm});
            skLineSegment(sketch, "E127.3", {"start": v(-58.38, 16.82) * mm, "end": v(-56.4, 16.82) * mm});
            skLineSegment(sketch, "E127.5", {"start": v(-55.4, 15.1) * mm, "end": v(-56.4, 13.38) * mm});
            skLineSegment(sketch, "E128.2", {"start": v(-55.25, 9.24) * mm, "end": v(-54.59, 10.4) * mm});
            skLineSegment(sketch, "E128.3", {"start": v(-54.59, 10.4) * mm, "end": v(-52.6, 10.4) * mm});
            skLineSegment(sketch, "E128.4", {"start": v(-52.6, 10.4) * mm, "end": v(-51.74, 8.9) * mm});
            skLineSegment(sketch, "E129", {"start": v(-51.85, 10.82) * mm, "end": v(-50.87, 9.13) * mm});
            skLineSegment(sketch, "E130.0", {"start": v(-52.61, 11.26) * mm, "end": v(-54.6, 11.26) * mm});
            skLineSegment(sketch, "E130.1", {"start": v(-54.6, 11.26) * mm, "end": v(-55.59, 12.98) * mm});
            skLineSegment(sketch, "E130.2", {"start": v(-55.59, 12.98) * mm, "end": v(-54.6, 14.7) * mm});
            skLineSegment(sketch, "E130.3", {"start": v(-54.6, 14.7) * mm, "end": v(-52.61, 14.7) * mm});
            skLineSegment(sketch, "E130.4", {"start": v(-52.61, 14.7) * mm, "end": v(-51.62, 12.98) * mm});
            skLineSegment(sketch, "E130.5", {"start": v(-51.62, 12.98) * mm, "end": v(-52.61, 11.26) * mm});
            skLineSegment(sketch, "E131", {"start": v(-51.94, 15.27) * mm, "end": v(-50.88, 13.44) * mm});
            skLineSegment(sketch, "E132", {"start": v(-51, 12.31) * mm, "end": v(-51.85, 10.82) * mm});
            skLineSegment(sketch, "E133.0", {"start": v(-63.89, 8.97) * mm, "end": v(-65.87, 8.97) * mm});
            skLineSegment(sketch, "E133.1", {"start": v(-65.87, 8.97) * mm, "end": v(-66.86, 10.7) * mm});
            skLineSegment(sketch, "E133.2", {"start": v(-66.86, 10.7) * mm, "end": v(-65.87, 12.4) * mm});
            skLineSegment(sketch, "E133.3", {"start": v(-65.87, 12.4) * mm, "end": v(-63.89, 12.4) * mm});
            skLineSegment(sketch, "E133.4", {"start": v(-63.89, 12.4) * mm, "end": v(-62.9, 10.7) * mm});
            skLineSegment(sketch, "E133.5", {"start": v(-62.9, 10.7) * mm, "end": v(-63.89, 8.97) * mm});
            skLineSegment(sketch, "E134", {"start": v(-66.64, 12.84) * mm, "end": v(-67.65, 11.08) * mm});
            skLineSegment(sketch, "E135", {"start": v(-67.67, 10.33) * mm, "end": v(-66.7, 8.67) * mm});
            skLineSegment(sketch, "E136.0", {"start": v(-63.9, 13.28) * mm, "end": v(-65.88, 13.28) * mm});
            skLineSegment(sketch, "E136.1", {"start": v(-65.88, 13.28) * mm, "end": v(-66.87, 15) * mm});
            skLineSegment(sketch, "E136.2", {"start": v(-66.87, 15) * mm, "end": v(-65.88, 16.71) * mm});
            skLineSegment(sketch, "E136.3", {"start": v(-65.88, 16.71) * mm, "end": v(-63.9, 16.71) * mm});
            skLineSegment(sketch, "E136.4", {"start": v(-63.9, 16.71) * mm, "end": v(-62.9, 15) * mm});
            skLineSegment(sketch, "E136.5", {"start": v(-62.9, 15) * mm, "end": v(-63.9, 13.28) * mm});
            skLineSegment(sketch, "E137", {"start": v(-66.67, 17.09) * mm, "end": v(-67.68, 15.34) * mm});
            skLineSegment(sketch, "E138", {"start": v(-67.63, 14.56) * mm, "end": v(-66.64, 12.84) * mm});
            skLineSegment(sketch, "E139", {"start": v(-65.88, 12.4) * mm, "end": v(-63.88, 12.4) * mm});
            skLineSegment(sketch, "E140.2", {"start": v(-63.02, 8.67) * mm, "end": v(-62.08, 10.29) * mm});
            skLineSegment(sketch, "E140.3", {"start": v(-62.08, 10.29) * mm, "end": v(-60.1, 10.29) * mm});
            skLineSegment(sketch, "E140.4", {"start": v(-60.1, 10.29) * mm, "end": v(-59.23, 8.79) * mm});
            skLineSegment(sketch, "E141.0", {"start": v(-60.17, 11.16) * mm, "end": v(-62.1, 11.16) * mm});
            skLineSegment(sketch, "E141.1", {"start": v(-62.1, 11.16) * mm, "end": v(-63.08, 12.87) * mm});
            skLineSegment(sketch, "E141.2", {"start": v(-63.08, 12.87) * mm, "end": v(-62.1, 14.6) * mm});
            skLineSegment(sketch, "E141.3", {"start": v(-62.1, 14.6) * mm, "end": v(-60.1, 14.6) * mm});
            skLineSegment(sketch, "E141.4", {"start": v(-60.1, 14.6) * mm, "end": v(-59.16, 12.9) * mm});
            skLineSegment(sketch, "E142.1", {"start": v(-40.46, 8.67) * mm, "end": v(-40.54, 8.81) * mm});
            skLineSegment(sketch, "E142.2", {"start": v(-40.54, 8.81) * mm, "end": v(-39.55, 10.53) * mm});
            skLineSegment(sketch, "E142.3", {"start": v(-39.55, 10.53) * mm, "end": v(-37.56, 10.53) * mm});
            skLineSegment(sketch, "E142.4", {"start": v(-37.56, 10.53) * mm, "end": v(-36.57, 8.81) * mm});
            skLineSegment(sketch, "E143", {"start": v(-40.34, 10.92) * mm, "end": v(-41.35, 9.17) * mm});
            skLineSegment(sketch, "E144.0", {"start": v(-37.57, 11.4) * mm, "end": v(-39.56, 11.4) * mm});
            skLineSegment(sketch, "E144.1", {"start": v(-39.56, 11.4) * mm, "end": v(-40.55, 13.12) * mm});
            skLineSegment(sketch, "E144.2", {"start": v(-40.55, 13.12) * mm, "end": v(-39.56, 14.84) * mm});
            skLineSegment(sketch, "E144.3", {"start": v(-39.56, 14.84) * mm, "end": v(-37.57, 14.84) * mm});
            skLineSegment(sketch, "E144.4", {"start": v(-37.57, 14.84) * mm, "end": v(-36.58, 13.12) * mm});
            skLineSegment(sketch, "E144.5", {"start": v(-36.58, 13.12) * mm, "end": v(-37.57, 11.4) * mm});
            skLineSegment(sketch, "E145.0", {"start": v(-33.78, 9.28) * mm, "end": v(-35.77, 9.28) * mm});
            skLineSegment(sketch, "E145.1", {"start": v(-35.77, 9.28) * mm, "end": v(-36.76, 11) * mm});
            skLineSegment(sketch, "E145.2", {"start": v(-36.76, 11) * mm, "end": v(-35.77, 12.72) * mm});
            skLineSegment(sketch, "E145.3", {"start": v(-35.77, 12.72) * mm, "end": v(-33.79, 12.72) * mm});
            skLineSegment(sketch, "E145.4", {"start": v(-33.79, 12.72) * mm, "end": v(-32.8, 11) * mm});
            skLineSegment(sketch, "E145.5", {"start": v(-32.8, 11) * mm, "end": v(-33.78, 9.28) * mm});
            skLineSegment(sketch, "E146", {"start": v(-33.8, 13.58) * mm, "end": v(-35.85, 13.58) * mm});
            skLineSegment(sketch, "E147", {"start": v(-32.1, 10.47) * mm, "end": v(-33.02, 8.84) * mm});
            skLineSegment(sketch, "E148.1", {"start": v(-48.02, 8.67) * mm, "end": v(-48.04, 8.7) * mm});
            skLineSegment(sketch, "E148.2", {"start": v(-48.04, 8.7) * mm, "end": v(-47.04, 10.43) * mm});
            skLineSegment(sketch, "E148.3", {"start": v(-47.04, 10.43) * mm, "end": v(-45.06, 10.43) * mm});
            skLineSegment(sketch, "E148.4", {"start": v(-45.06, 10.43) * mm, "end": v(-44.07, 8.7) * mm});
            skLineSegment(sketch, "E148.5", {"start": v(-44.07, 8.7) * mm, "end": v(-44.09, 8.67) * mm});
            skLineSegment(sketch, "E149", {"start": v(-47.81, 10.85) * mm, "end": v(-48.8, 9.13) * mm});
            skLineSegment(sketch, "E150.0", {"start": v(-45.07, 11.3) * mm, "end": v(-47.05, 11.3) * mm});
            skLineSegment(sketch, "E150.1", {"start": v(-47.05, 11.3) * mm, "end": v(-48.04, 13.01) * mm});
            skLineSegment(sketch, "E150.2", {"start": v(-48.04, 13.01) * mm, "end": v(-47.05, 14.73) * mm});
            skLineSegment(sketch, "E150.4", {"start": v(-45.07, 14.73) * mm, "end": v(-44.08, 13.01) * mm});
            skLineSegment(sketch, "E150.5", {"start": v(-44.08, 13.01) * mm, "end": v(-45.07, 11.3) * mm});
            skLineSegment(sketch, "E151", {"start": v(-48.65, 12.31) * mm, "end": v(-47.81, 10.85) * mm});
            skLineSegment(sketch, "E152.0", {"start": v(-41.35, 9.17) * mm, "end": v(-43.27, 9.17) * mm});
            skLineSegment(sketch, "E152.1", {"start": v(-43.27, 9.17) * mm, "end": v(-44.26, 10.9) * mm});
            skLineSegment(sketch, "E152.2", {"start": v(-44.26, 10.9) * mm, "end": v(-43.27, 12.6) * mm});
            skLineSegment(sketch, "E152.3", {"start": v(-43.27, 12.6) * mm, "end": v(-41.28, 12.6) * mm});
            skLineSegment(sketch, "E152.4", {"start": v(-41.28, 12.6) * mm, "end": v(-40.34, 10.92) * mm});
            skLineSegment(sketch, "E153", {"start": v(-41.35, 13.48) * mm, "end": v(-43.34, 13.48) * mm});
            skLineSegment(sketch, "E154.1", {"start": v(-10.09, 8.67) * mm, "end": v(-10.2, 8.86) * mm});
            skLineSegment(sketch, "E154.2", {"start": v(-10.2, 8.86) * mm, "end": v(-9.2, 10.58) * mm});
            skLineSegment(sketch, "E154.3", {"start": v(-9.2, 10.58) * mm, "end": v(-7.22, 10.58) * mm});
            skLineSegment(sketch, "E154.4", {"start": v(-7.22, 10.58) * mm, "end": v(-6.23, 8.86) * mm});
            skLineSegment(sketch, "E154.5", {"start": v(-6.23, 8.86) * mm, "end": v(-6.34, 8.67) * mm});
            skLineSegment(sketch, "E155", {"start": v(-10, 10.97) * mm, "end": v(-11, 9.22) * mm});
            skLineSegment(sketch, "E156.0", {"start": v(-7.23, 11.45) * mm, "end": v(-9.21, 11.45) * mm});
            skLineSegment(sketch, "E156.1", {"start": v(-9.21, 11.45) * mm, "end": v(-10.2, 13.17) * mm});
            skLineSegment(sketch, "E156.2", {"start": v(-10.2, 13.17) * mm, "end": v(-9.21, 14.89) * mm});
            skLineSegment(sketch, "E156.3", {"start": v(-9.21, 14.89) * mm, "end": v(-7.23, 14.89) * mm});
            skLineSegment(sketch, "E156.4", {"start": v(-7.23, 14.89) * mm, "end": v(-6.24, 13.17) * mm});
            skLineSegment(sketch, "E156.5", {"start": v(-6.24, 13.17) * mm, "end": v(-7.23, 11.45) * mm});
            skLineSegment(sketch, "E157", {"start": v(-10, 15.27) * mm, "end": v(-11.01, 13.53) * mm});
            skLineSegment(sketch, "E158", {"start": v(-6.47, 15.3) * mm, "end": v(-5.5, 13.63) * mm});
            skLineSegment(sketch, "E159.0", {"start": v(-3.44, 9.33) * mm, "end": v(-5.43, 9.33) * mm});
            skLineSegment(sketch, "E159.1", {"start": v(-5.43, 9.33) * mm, "end": v(-6.42, 11.05) * mm});
            skLineSegment(sketch, "E159.2", {"start": v(-6.42, 11.05) * mm, "end": v(-5.43, 12.77) * mm});
            skLineSegment(sketch, "E159.3", {"start": v(-5.43, 12.77) * mm, "end": v(-3.44, 12.77) * mm});
            skLineSegment(sketch, "E159.4", {"start": v(-3.44, 12.77) * mm, "end": v(-2.45, 11.05) * mm});
            skLineSegment(sketch, "E159.5", {"start": v(-2.45, 11.05) * mm, "end": v(-3.44, 9.33) * mm});
            skLineSegment(sketch, "E160", {"start": v(-3.45, 13.63) * mm, "end": v(-5.5, 13.63) * mm});
            skLineSegment(sketch, "E161", {"start": v(-2.6, 13.04) * mm, "end": v(-1.68, 11.45) * mm});
            skLineSegment(sketch, "E162", {"start": v(-1.71, 10.58) * mm, "end": v(-2.68, 8.89) * mm});
            skLineSegment(sketch, "E163.1", {"start": v(-17.64, 8.67) * mm, "end": v(-17.7, 8.76) * mm});
            skLineSegment(sketch, "E163.2", {"start": v(-17.7, 8.76) * mm, "end": v(-16.7, 10.48) * mm});
            skLineSegment(sketch, "E163.3", {"start": v(-16.7, 10.48) * mm, "end": v(-14.72, 10.48) * mm});
            skLineSegment(sketch, "E163.4", {"start": v(-14.72, 10.48) * mm, "end": v(-13.72, 8.76) * mm});
            skLineSegment(sketch, "E163.5", {"start": v(-13.72, 8.76) * mm, "end": v(-13.77, 8.67) * mm});
            skLineSegment(sketch, "E164.0", {"start": v(-14.72, 11.34) * mm, "end": v(-16.7, 11.34) * mm});
            skLineSegment(sketch, "E164.1", {"start": v(-16.7, 11.34) * mm, "end": v(-17.7, 13.06) * mm});
            skLineSegment(sketch, "E164.2", {"start": v(-17.7, 13.06) * mm, "end": v(-16.7, 14.78) * mm});
            skLineSegment(sketch, "E164.3", {"start": v(-16.7, 14.78) * mm, "end": v(-14.73, 14.78) * mm});
            skLineSegment(sketch, "E164.4", {"start": v(-14.73, 14.78) * mm, "end": v(-13.73, 13.06) * mm});
            skLineSegment(sketch, "E164.5", {"start": v(-13.73, 13.06) * mm, "end": v(-14.72, 11.34) * mm});
            skLineSegment(sketch, "E165", {"start": v(-13.96, 15.19) * mm, "end": v(-13, 13.53) * mm});
            skLineSegment(sketch, "E166.0", {"start": v(-11, 9.22) * mm, "end": v(-12.92, 9.22) * mm});
            skLineSegment(sketch, "E166.1", {"start": v(-12.92, 9.22) * mm, "end": v(-13.91, 10.94) * mm});
            skLineSegment(sketch, "E166.2", {"start": v(-13.91, 10.94) * mm, "end": v(-12.92, 12.66) * mm});
            skLineSegment(sketch, "E166.3", {"start": v(-12.92, 12.66) * mm, "end": v(-10.94, 12.66) * mm});
            skLineSegment(sketch, "E166.4", {"start": v(-10.94, 12.66) * mm, "end": v(-10, 10.97) * mm});
            skLineSegment(sketch, "E167", {"start": v(-11.01, 13.53) * mm, "end": v(-13, 13.53) * mm});
            skLineSegment(sketch, "E168.0", {"start": v(-22.39, 11.45) * mm, "end": v(-24.37, 11.45) * mm});
            skLineSegment(sketch, "E168.1", {"start": v(-24.37, 11.45) * mm, "end": v(-25.36, 13.17) * mm});
            skLineSegment(sketch, "E168.2", {"start": v(-25.36, 13.17) * mm, "end": v(-24.37, 14.9) * mm});
            skLineSegment(sketch, "E168.3", {"start": v(-24.37, 14.9) * mm, "end": v(-22.39, 14.9) * mm});
            skLineSegment(sketch, "E168.4", {"start": v(-22.39, 14.9) * mm, "end": v(-21.4, 13.17) * mm});
            skLineSegment(sketch, "E168.5", {"start": v(-21.4, 13.17) * mm, "end": v(-22.39, 11.45) * mm});
            skLineSegment(sketch, "E169", {"start": v(-25.16, 15.28) * mm, "end": v(-26.17, 13.53) * mm});
            skLineSegment(sketch, "E170", {"start": v(-24.31, 10.57) * mm, "end": v(-22.31, 10.57) * mm});
            skLineSegment(sketch, "E171.0", {"start": v(-22.4, 15.76) * mm, "end": v(-24.38, 15.76) * mm});
            skLineSegment(sketch, "E171.1", {"start": v(-24.38, 15.76) * mm, "end": v(-25.37, 17.48) * mm});
            skLineSegment(sketch, "E171.2", {"start": v(-25.37, 17.48) * mm, "end": v(-24.38, 19.2) * mm});
            skLineSegment(sketch, "E171.3", {"start": v(-24.38, 19.2) * mm, "end": v(-22.4, 19.2) * mm});
            skLineSegment(sketch, "E172", {"start": v(-25.17, 19.57) * mm, "end": v(-26.18, 17.83) * mm});
            skLineSegment(sketch, "E173.0", {"start": v(-18.6, 9.33) * mm, "end": v(-20.58, 9.33) * mm});
            skLineSegment(sketch, "E173.1", {"start": v(-20.58, 9.33) * mm, "end": v(-21.58, 11.05) * mm});
            skLineSegment(sketch, "E173.2", {"start": v(-21.58, 11.05) * mm, "end": v(-20.58, 12.77) * mm});
            skLineSegment(sketch, "E173.3", {"start": v(-20.58, 12.77) * mm, "end": v(-18.6, 12.77) * mm});
            skLineSegment(sketch, "E173.4", {"start": v(-18.6, 12.77) * mm, "end": v(-17.6, 11.05) * mm});
            skLineSegment(sketch, "E173.5", {"start": v(-17.6, 11.05) * mm, "end": v(-18.6, 9.33) * mm});
            skLineSegment(sketch, "E174", {"start": v(-22.31, 10.57) * mm, "end": v(-21.22, 8.67) * mm});
            skLineSegment(sketch, "E175.0", {"start": v(-18.6, 13.64) * mm, "end": v(-20.6, 13.64) * mm});
            skLineSegment(sketch, "E175.1", {"start": v(-20.6, 13.64) * mm, "end": v(-21.58, 15.36) * mm});
            skLineSegment(sketch, "E175.2", {"start": v(-21.58, 15.36) * mm, "end": v(-20.6, 17.07) * mm});
            skLineSegment(sketch, "E175.3", {"start": v(-20.6, 17.07) * mm, "end": v(-18.6, 17.07) * mm});
            skLineSegment(sketch, "E175.4", {"start": v(-18.6, 17.07) * mm, "end": v(-17.62, 15.36) * mm});
            skLineSegment(sketch, "E175.5", {"start": v(-17.62, 15.36) * mm, "end": v(-18.6, 13.64) * mm});
            skLineSegment(sketch, "E176", {"start": v(-18.4, 17.94) * mm, "end": v(-20.66, 17.94) * mm});
            skLineSegment(sketch, "E177.0", {"start": v(-29.88, 11.35) * mm, "end": v(-31.87, 11.35) * mm});
            skLineSegment(sketch, "E177.1", {"start": v(-31.87, 11.35) * mm, "end": v(-32.86, 13.07) * mm});
            skLineSegment(sketch, "E177.2", {"start": v(-32.86, 13.07) * mm, "end": v(-31.87, 14.78) * mm});
            skLineSegment(sketch, "E177.3", {"start": v(-31.87, 14.78) * mm, "end": v(-29.88, 14.78) * mm});
            skLineSegment(sketch, "E177.4", {"start": v(-29.88, 14.78) * mm, "end": v(-28.9, 13.07) * mm});
            skLineSegment(sketch, "E177.5", {"start": v(-28.9, 13.07) * mm, "end": v(-29.88, 11.35) * mm});
            skLineSegment(sketch, "E178", {"start": v(-32.1, 10.47) * mm, "end": v(-29.8, 10.47) * mm});
            skLineSegment(sketch, "E179.0", {"start": v(-31.86, 15.65) * mm, "end": v(-31.88, 15.65) * mm});
            skLineSegment(sketch, "E179.1", {"start": v(-31.88, 15.65) * mm, "end": v(-32.87, 17.37) * mm});
            skLineSegment(sketch, "E179.2", {"start": v(-32.87, 17.37) * mm, "end": v(-31.88, 19.08) * mm});
            skLineSegment(sketch, "E179.4", {"start": v(-29.9, 19.09) * mm, "end": v(-29.88, 19.07) * mm});
            skLineSegment(sketch, "E180", {"start": v(-29.16, 19.56) * mm, "end": v(-28.17, 17.83) * mm});
            skLineSegment(sketch, "E181.0", {"start": v(-26.1, 9.23) * mm, "end": v(-28.08, 9.23) * mm});
            skLineSegment(sketch, "E181.1", {"start": v(-28.08, 9.23) * mm, "end": v(-29.07, 10.94) * mm});
            skLineSegment(sketch, "E181.2", {"start": v(-29.07, 10.94) * mm, "end": v(-28.08, 12.66) * mm});
            skLineSegment(sketch, "E181.3", {"start": v(-28.08, 12.66) * mm, "end": v(-26.1, 12.66) * mm});
            skLineSegment(sketch, "E181.4", {"start": v(-26.1, 12.66) * mm, "end": v(-25.1, 10.94) * mm});
            skLineSegment(sketch, "E181.5", {"start": v(-25.1, 10.94) * mm, "end": v(-26.1, 9.23) * mm});
            skLineSegment(sketch, "E182", {"start": v(-29.8, 10.47) * mm, "end": v(-28.77, 8.67) * mm});
            skLineSegment(sketch, "E183", {"start": v(-24.31, 10.57) * mm, "end": v(-25.4, 8.67) * mm});
            skLineSegment(sketch, "E184.0", {"start": v(-26.17, 13.53) * mm, "end": v(-28.09, 13.53) * mm});
            skLineSegment(sketch, "E184.1", {"start": v(-28.09, 13.53) * mm, "end": v(-29.08, 15.25) * mm});
            skLineSegment(sketch, "E184.2", {"start": v(-29.08, 15.25) * mm, "end": v(-28.09, 16.97) * mm});
            skLineSegment(sketch, "E184.3", {"start": v(-28.09, 16.97) * mm, "end": v(-26.1, 16.97) * mm});
            skLineSegment(sketch, "E184.4", {"start": v(-26.1, 16.97) * mm, "end": v(-25.16, 15.28) * mm});
            skLineSegment(sketch, "E185", {"start": v(-26.18, 17.83) * mm, "end": v(-28.17, 17.83) * mm});
            skLineSegment(sketch, "E186.trimOffspring", {"start": v(-40.33, 15.25) * mm, "end": v(-41.35, 13.48) * mm});
            skLineSegment(sketch, "E187.trimOffspring", {"start": v(-47.83, 15.14) * mm, "end": v(-48.81, 13.44) * mm});
            skLineSegment(sketch, "E188", {"start": v(-36.57, 8.81) * mm, "end": v(-36.57, 8.67) * mm});
            skLineSegment(sketch, "E189", {"start": v(-33.02, 8.84) * mm, "end": v(-33.02, 8.67) * mm});
            skLineSegment(sketch, "E190", {"start": v(-59.23, 8.79) * mm, "end": v(-59.23, 8.67) * mm});
            skLineSegment(sketch, "E191", {"start": v(-55.25, 9.24) * mm, "end": v(-55.58, 8.67) * mm});
            skLineSegment(sketch, "E192", {"start": v(-50.87, 9.13) * mm, "end": v(-48.8, 9.13) * mm});
            skLineSegment(sketch, "E193", {"start": v(-51.74, 8.9) * mm, "end": v(-51.86, 8.67) * mm});
            skLineSegment(sketch, "E194.trimOffspring", {"start": v(-48.02, 8.67) * mm, "end": v(-69.72, 8.67) * mm});
            skLineSegment(sketch, "E195", {"start": v(-47.72, 8.67) * mm, "end": v(-48.02, 8.67) * mm});
            skPoint(sketch, "E196.end.orphan", {"position": v(-65.72, 36.1) * mm});
            skLineSegment(sketch, "E197", {"start": v(-50.88, 13.44) * mm, "end": v(-48.81, 13.44) * mm});
            skLineSegment(sketch, "E198", {"start": v(-51, 12.31) * mm, "end": v(-48.65, 12.31) * mm});
            skLineSegment(sketch, "E199", {"start": v(-43.34, 13.48) * mm, "end": v(-44.37, 15.07) * mm});
            skLineSegment(sketch, "E200", {"start": v(-67.69, 24.25) * mm, "end": v(-69.72, 24.25) * mm});
            skLineSegment(sketch, "E201", {"start": v(-67.8, 23.33) * mm, "end": v(-69.72, 23.33) * mm});
            skLineSegment(sketch, "E202", {"start": v(-67.78, 19.78) * mm, "end": v(-69.72, 19.78) * mm});
            skLineSegment(sketch, "E203", {"start": v(-67.8, 19.04) * mm, "end": v(-69.72, 19.04) * mm});
            skLineSegment(sketch, "E204", {"start": v(-67.68, 15.34) * mm, "end": v(-69.72, 15.34) * mm});
            skLineSegment(sketch, "E205", {"start": v(-67.63, 14.56) * mm, "end": v(-69.72, 14.56) * mm});
            skLineSegment(sketch, "E206", {"start": v(-67.65, 11.08) * mm, "end": v(-69.72, 11.08) * mm});
            skLineSegment(sketch, "E207", {"start": v(-67.67, 10.33) * mm, "end": v(-69.72, 10.33) * mm});
            skLineSegment(sketch, "E208.trimOffspring", {"start": v(-69.72, 31.87) * mm, "end": v(-69.72, 8.67) * mm});
            skLineSegment(sketch, "E209.0", {"start": v(-30.04, 28.63) * mm, "end": v(-32.02, 28.63) * mm});
            skLineSegment(sketch, "E209.1", {"start": v(-32.02, 28.63) * mm, "end": v(-33.01, 30.35) * mm});
            skLineSegment(sketch, "E209.2", {"start": v(-33.01, 30.35) * mm, "end": v(-32.02, 32.07) * mm});
            skLineSegment(sketch, "E209.3", {"start": v(-32.02, 32.07) * mm, "end": v(-30.04, 32.07) * mm});
            skLineSegment(sketch, "E209.4", {"start": v(-30.04, 32.07) * mm, "end": v(-29.05, 30.35) * mm});
            skLineSegment(sketch, "E209.5", {"start": v(-29.05, 30.35) * mm, "end": v(-30.04, 28.63) * mm});
            skLineSegment(sketch, "E210", {"start": v(-32.81, 32.46) * mm, "end": v(-33.82, 30.7) * mm});
            skLineSegment(sketch, "E211", {"start": v(-31.97, 27.75) * mm, "end": v(-29.96, 27.75) * mm});
            skLineSegment(sketch, "E212.0", {"start": v(-30.05, 32.94) * mm, "end": v(-32.03, 32.94) * mm});
            skLineSegment(sketch, "E212.1", {"start": v(-32.03, 32.94) * mm, "end": v(-33.02, 34.65) * mm});
            skLineSegment(sketch, "E212.2", {"start": v(-33.02, 34.65) * mm, "end": v(-32.19, 36.1) * mm});
            skLineSegment(sketch, "E212.4", {"start": v(-29.89, 36.1) * mm, "end": v(-29.05, 34.65) * mm});
            skLineSegment(sketch, "E212.5", {"start": v(-29.05, 34.65) * mm, "end": v(-30.05, 32.94) * mm});
            skLineSegment(sketch, "E213", {"start": v(-33.2, 36.1) * mm, "end": v(-33.83, 35.01) * mm});
            skLineSegment(sketch, "E214", {"start": v(-28.89, 36.1) * mm, "end": v(-28.32, 35.12) * mm});
            skLineSegment(sketch, "E215.0", {"start": v(-26.25, 26.51) * mm, "end": v(-28.24, 26.51) * mm});
            skLineSegment(sketch, "E215.1", {"start": v(-28.24, 26.51) * mm, "end": v(-29.23, 28.23) * mm});
            skLineSegment(sketch, "E215.2", {"start": v(-29.23, 28.23) * mm, "end": v(-28.24, 29.95) * mm});
            skLineSegment(sketch, "E215.3", {"start": v(-28.24, 29.95) * mm, "end": v(-26.25, 29.95) * mm});
            skLineSegment(sketch, "E215.4", {"start": v(-26.25, 29.95) * mm, "end": v(-26.24, 29.94) * mm});
            skLineSegment(sketch, "E215.5", {"start": v(-25.26, 28.23) * mm, "end": v(-26.25, 26.51) * mm});
            skLineSegment(sketch, "E216", {"start": v(-29.96, 27.75) * mm, "end": v(-28.95, 26) * mm});
            skLineSegment(sketch, "E217", {"start": v(-24.63, 27.58) * mm, "end": v(-25.46, 26.12) * mm});
            skLineSegment(sketch, "E218.0", {"start": v(-26.26, 30.81) * mm, "end": v(-28.24, 30.81) * mm});
            skLineSegment(sketch, "E218.1", {"start": v(-28.24, 30.81) * mm, "end": v(-29.24, 32.53) * mm});
            skLineSegment(sketch, "E218.2", {"start": v(-29.24, 32.53) * mm, "end": v(-28.24, 34.25) * mm});
            skLineSegment(sketch, "E218.3", {"start": v(-28.24, 34.25) * mm, "end": v(-26.26, 34.25) * mm});
            skLineSegment(sketch, "E218.4", {"start": v(-26.26, 34.25) * mm, "end": v(-25.27, 32.53) * mm});
            skLineSegment(sketch, "E218.5", {"start": v(-25.27, 32.53) * mm, "end": v(-26.26, 30.81) * mm});
            skLineSegment(sketch, "E219", {"start": v(-26.05, 35.12) * mm, "end": v(-28.32, 35.12) * mm});
            skLineSegment(sketch, "E220", {"start": v(-28.24, 29.94) * mm, "end": v(-26.24, 29.94) * mm});
            skLineSegment(sketch, "E221.0", {"start": v(-37.53, 28.53) * mm, "end": v(-39.52, 28.53) * mm});
            skLineSegment(sketch, "E221.1", {"start": v(-39.52, 28.53) * mm, "end": v(-40.51, 30.24) * mm});
            skLineSegment(sketch, "E221.2", {"start": v(-40.51, 30.24) * mm, "end": v(-39.52, 31.96) * mm});
            skLineSegment(sketch, "E221.3", {"start": v(-39.52, 31.96) * mm, "end": v(-37.53, 31.96) * mm});
            skLineSegment(sketch, "E221.4", {"start": v(-37.53, 31.96) * mm, "end": v(-36.54, 30.24) * mm});
            skLineSegment(sketch, "E221.5", {"start": v(-36.54, 30.24) * mm, "end": v(-37.53, 28.53) * mm});
            skLineSegment(sketch, "E222", {"start": v(-39.78, 27.65) * mm, "end": v(-37.46, 27.65) * mm});
            skLineSegment(sketch, "E223.0", {"start": v(-37.54, 32.83) * mm, "end": v(-39.53, 32.83) * mm});
            skLineSegment(sketch, "E223.1", {"start": v(-39.53, 32.83) * mm, "end": v(-40.52, 34.55) * mm});
            skLineSegment(sketch, "E223.2", {"start": v(-40.52, 34.55) * mm, "end": v(-39.62, 36.1) * mm});
            skLineSegment(sketch, "E223.4", {"start": v(-37.45, 36.1) * mm, "end": v(-36.55, 34.55) * mm});
            skLineSegment(sketch, "E223.5", {"start": v(-36.55, 34.55) * mm, "end": v(-37.54, 32.83) * mm});
            skLineSegment(sketch, "E224", {"start": v(-40.64, 36.1) * mm, "end": v(-41.24, 35.06) * mm});
            skLineSegment(sketch, "E225", {"start": v(-36.45, 36.1) * mm, "end": v(-35.82, 35.01) * mm});
            skLineSegment(sketch, "E226.0", {"start": v(-33.75, 26.4) * mm, "end": v(-35.73, 26.4) * mm});
            skLineSegment(sketch, "E226.1", {"start": v(-35.73, 26.4) * mm, "end": v(-36.72, 28.12) * mm});
            skLineSegment(sketch, "E226.2", {"start": v(-36.72, 28.12) * mm, "end": v(-35.73, 29.84) * mm});
            skLineSegment(sketch, "E226.3", {"start": v(-35.73, 29.84) * mm, "end": v(-33.75, 29.84) * mm});
            skLineSegment(sketch, "E226.4", {"start": v(-33.75, 29.84) * mm, "end": v(-32.76, 28.12) * mm});
            skLineSegment(sketch, "E226.5", {"start": v(-32.76, 28.12) * mm, "end": v(-33.75, 26.4) * mm});
            skLineSegment(sketch, "E227", {"start": v(-37.46, 27.65) * mm, "end": v(-36.44, 25.89) * mm});
            skLineSegment(sketch, "E228", {"start": v(-31.97, 27.75) * mm, "end": v(-32.96, 26.01) * mm});
            skLineSegment(sketch, "E229.0", {"start": v(-33.82, 30.7) * mm, "end": v(-35.74, 30.7) * mm});
            skLineSegment(sketch, "E229.1", {"start": v(-35.74, 30.7) * mm, "end": v(-36.73, 32.43) * mm});
            skLineSegment(sketch, "E229.2", {"start": v(-36.73, 32.43) * mm, "end": v(-35.74, 34.15) * mm});
            skLineSegment(sketch, "E229.3", {"start": v(-35.74, 34.15) * mm, "end": v(-33.76, 34.15) * mm});
            skLineSegment(sketch, "E229.4", {"start": v(-33.76, 34.15) * mm, "end": v(-32.81, 32.46) * mm});
            skLineSegment(sketch, "E230", {"start": v(-33.83, 35.01) * mm, "end": v(-35.82, 35.01) * mm});
            skLineSegment(sketch, "E231.2", {"start": v(-29.14, 19.6) * mm, "end": v(-28.14, 21.3) * mm});
            skLineSegment(sketch, "E231.3", {"start": v(-28.14, 21.3) * mm, "end": v(-26.16, 21.3) * mm});
            skLineSegment(sketch, "E231.4", {"start": v(-26.16, 21.3) * mm, "end": v(-25.17, 19.6) * mm});
            skLineSegment(sketch, "E232", {"start": v(-28.94, 21.7) * mm, "end": v(-29.94, 19.95) * mm});
            skLineSegment(sketch, "E233.0", {"start": v(-26.17, 22.18) * mm, "end": v(-28.15, 22.18) * mm});
            skLineSegment(sketch, "E233.1", {"start": v(-28.15, 22.18) * mm, "end": v(-29.14, 23.9) * mm});
            skLineSegment(sketch, "E233.2", {"start": v(-29.14, 23.9) * mm, "end": v(-28.15, 25.61) * mm});
            skLineSegment(sketch, "E233.3", {"start": v(-28.15, 25.61) * mm, "end": v(-26.17, 25.61) * mm});
            skLineSegment(sketch, "E233.4", {"start": v(-26.17, 25.61) * mm, "end": v(-25.18, 23.9) * mm});
            skLineSegment(sketch, "E233.5", {"start": v(-25.18, 23.9) * mm, "end": v(-26.17, 22.18) * mm});
            skLineSegment(sketch, "E234", {"start": v(-28.95, 26) * mm, "end": v(-29.95, 24.25) * mm});
            skLineSegment(sketch, "E235", {"start": v(-25.46, 26.12) * mm, "end": v(-24.44, 24.36) * mm});
            skLineSegment(sketch, "E236.4", {"start": v(-22.37, 19.19) * mm, "end": v(-21.38, 17.47) * mm});
            skLineSegment(sketch, "E236.5", {"start": v(-21.38, 17.47) * mm, "end": v(-22.37, 15.76) * mm});
            skLineSegment(sketch, "E237.0", {"start": v(-22.38, 20.06) * mm, "end": v(-24.37, 20.06) * mm});
            skLineSegment(sketch, "E237.1", {"start": v(-24.37, 20.06) * mm, "end": v(-25.36, 21.77) * mm});
            skLineSegment(sketch, "E237.2", {"start": v(-25.36, 21.77) * mm, "end": v(-24.37, 23.5) * mm});
            skLineSegment(sketch, "E237.3", {"start": v(-24.37, 23.5) * mm, "end": v(-22.38, 23.5) * mm});
            skLineSegment(sketch, "E237.4", {"start": v(-22.38, 23.5) * mm, "end": v(-21.39, 21.77) * mm});
            skLineSegment(sketch, "E237.5", {"start": v(-21.39, 21.77) * mm, "end": v(-22.38, 20.06) * mm});
            skLineSegment(sketch, "E238", {"start": v(-22.17, 24.36) * mm, "end": v(-24.44, 24.36) * mm});
            skLineSegment(sketch, "E239.0", {"start": v(-33.66, 17.77) * mm, "end": v(-35.64, 17.77) * mm});
            skLineSegment(sketch, "E239.1", {"start": v(-35.64, 17.77) * mm, "end": v(-36.63, 19.48) * mm});
            skLineSegment(sketch, "E239.2", {"start": v(-36.63, 19.48) * mm, "end": v(-35.64, 21.2) * mm});
            skLineSegment(sketch, "E239.3", {"start": v(-35.64, 21.2) * mm, "end": v(-33.66, 21.2) * mm});
            skLineSegment(sketch, "E239.4", {"start": v(-33.66, 21.2) * mm, "end": v(-32.66, 19.48) * mm});
            skLineSegment(sketch, "E239.5", {"start": v(-32.66, 19.48) * mm, "end": v(-33.66, 17.77) * mm});
            skLineSegment(sketch, "E240", {"start": v(-35.9, 16.89) * mm, "end": v(-33.58, 16.89) * mm});
            skLineSegment(sketch, "E241.0", {"start": v(-33.66, 22.07) * mm, "end": v(-35.65, 22.07) * mm});
            skLineSegment(sketch, "E241.1", {"start": v(-35.65, 22.07) * mm, "end": v(-36.64, 23.79) * mm});
            skLineSegment(sketch, "E241.2", {"start": v(-36.64, 23.79) * mm, "end": v(-35.65, 25.5) * mm});
            skLineSegment(sketch, "E241.3", {"start": v(-35.65, 25.5) * mm, "end": v(-33.67, 25.5) * mm});
            skLineSegment(sketch, "E241.4", {"start": v(-33.67, 25.5) * mm, "end": v(-32.67, 23.79) * mm});
            skLineSegment(sketch, "E241.5", {"start": v(-32.67, 23.79) * mm, "end": v(-33.66, 22.07) * mm});
            skLineSegment(sketch, "E242", {"start": v(-36.44, 25.89) * mm, "end": v(-37.36, 24.3) * mm});
            skLineSegment(sketch, "E243", {"start": v(-35.65, 21.2) * mm, "end": v(-33.65, 21.2) * mm});
            skLineSegment(sketch, "E244", {"start": v(-32.96, 26.01) * mm, "end": v(-31.94, 24.25) * mm});
            skLineSegment(sketch, "E245.0", {"start": v(-29.87, 15.65) * mm, "end": v(-31.85, 15.65) * mm});
            skLineSegment(sketch, "E245.1", {"start": v(-31.85, 15.65) * mm, "end": v(-31.86, 15.65) * mm});
            skLineSegment(sketch, "E245.3", {"start": v(-31.85, 19.08) * mm, "end": v(-29.87, 19.08) * mm});
            skLineSegment(sketch, "E245.4", {"start": v(-29.87, 19.08) * mm, "end": v(-28.88, 17.36) * mm});
            skLineSegment(sketch, "E245.5", {"start": v(-28.88, 17.36) * mm, "end": v(-29.87, 15.65) * mm});
            skLineSegment(sketch, "E246", {"start": v(-33.58, 16.89) * mm, "end": v(-32.73, 15.4) * mm});
            skLineSegment(sketch, "E247.0", {"start": v(-29.94, 19.95) * mm, "end": v(-31.86, 19.95) * mm});
            skLineSegment(sketch, "E247.1", {"start": v(-31.86, 19.95) * mm, "end": v(-32.85, 21.67) * mm});
            skLineSegment(sketch, "E247.2", {"start": v(-32.85, 21.67) * mm, "end": v(-31.86, 23.39) * mm});
            skLineSegment(sketch, "E247.3", {"start": v(-31.86, 23.39) * mm, "end": v(-29.88, 23.39) * mm});
            skLineSegment(sketch, "E247.4", {"start": v(-29.88, 23.39) * mm, "end": v(-28.94, 21.7) * mm});
            skLineSegment(sketch, "E248", {"start": v(-29.95, 24.25) * mm, "end": v(-31.94, 24.25) * mm});
            skLineSegment(sketch, "E249", {"start": v(-29.88, 19.07) * mm, "end": v(-29.86, 19.07) * mm});
            skLineSegment(sketch, "E250.0", {"start": v(-14.92, 28.57) * mm, "end": v(-16.9, 28.57) * mm});
            skLineSegment(sketch, "E250.1", {"start": v(-16.9, 28.57) * mm, "end": v(-17.9, 30.29) * mm});
            skLineSegment(sketch, "E250.2", {"start": v(-17.9, 30.29) * mm, "end": v(-16.9, 32) * mm});
            skLineSegment(sketch, "E250.3", {"start": v(-16.9, 32) * mm, "end": v(-14.92, 32) * mm});
            skLineSegment(sketch, "E250.4", {"start": v(-14.92, 32) * mm, "end": v(-13.93, 30.29) * mm});
            skLineSegment(sketch, "E250.5", {"start": v(-13.93, 30.29) * mm, "end": v(-14.92, 28.57) * mm});
            skLineSegment(sketch, "E251", {"start": v(-17.7, 32.4) * mm, "end": v(-18.7, 30.65) * mm});
            skLineSegment(sketch, "E252", {"start": v(-16.85, 27.69) * mm, "end": v(-14.85, 27.69) * mm});
            skLineSegment(sketch, "E253.0", {"start": v(-14.93, 32.87) * mm, "end": v(-16.91, 32.87) * mm});
            skLineSegment(sketch, "E253.1", {"start": v(-16.91, 32.87) * mm, "end": v(-17.9, 34.6) * mm});
            skLineSegment(sketch, "E253.2", {"start": v(-17.9, 34.6) * mm, "end": v(-17.03, 36.1) * mm});
            skLineSegment(sketch, "E253.4", {"start": v(-14.8, 36.1) * mm, "end": v(-13.94, 34.6) * mm});
            skLineSegment(sketch, "E253.5", {"start": v(-13.94, 34.6) * mm, "end": v(-14.93, 32.87) * mm});
            skLineSegment(sketch, "E254", {"start": v(-18.05, 36.1) * mm, "end": v(-18.71, 34.95) * mm});
            skLineSegment(sketch, "E255", {"start": v(-13.8, 36.1) * mm, "end": v(-13.2, 35.05) * mm});
            skLineSegment(sketch, "E256.0", {"start": v(-11.13, 26.45) * mm, "end": v(-13.12, 26.45) * mm});
            skLineSegment(sketch, "E256.1", {"start": v(-13.12, 26.45) * mm, "end": v(-14.11, 28.17) * mm});
            skLineSegment(sketch, "E256.2", {"start": v(-14.11, 28.17) * mm, "end": v(-13.12, 29.89) * mm});
            skLineSegment(sketch, "E256.3", {"start": v(-13.12, 29.89) * mm, "end": v(-11.13, 29.89) * mm});
            skLineSegment(sketch, "E256.4", {"start": v(-11.13, 29.89) * mm, "end": v(-10.14, 28.17) * mm});
            skLineSegment(sketch, "E256.5", {"start": v(-10.14, 28.17) * mm, "end": v(-11.13, 26.45) * mm});
            skLineSegment(sketch, "E257", {"start": v(-14.85, 27.69) * mm, "end": v(-13.83, 25.93) * mm});
            skLineSegment(sketch, "E258", {"start": v(-10.38, 30.31) * mm, "end": v(-9.41, 28.64) * mm});
            skLineSegment(sketch, "E259", {"start": v(-9.44, 27.64) * mm, "end": v(-10.34, 26.06) * mm});
            skLineSegment(sketch, "E260.0", {"start": v(-11.14, 30.75) * mm, "end": v(-13.13, 30.75) * mm});
            skLineSegment(sketch, "E260.1", {"start": v(-13.13, 30.75) * mm, "end": v(-14.12, 32.47) * mm});
            skLineSegment(sketch, "E260.2", {"start": v(-14.12, 32.47) * mm, "end": v(-13.13, 34.19) * mm});
            skLineSegment(sketch, "E260.3", {"start": v(-13.13, 34.19) * mm, "end": v(-11.14, 34.19) * mm});
            skLineSegment(sketch, "E260.4", {"start": v(-11.14, 34.19) * mm, "end": v(-10.15, 32.47) * mm});
            skLineSegment(sketch, "E260.5", {"start": v(-10.15, 32.47) * mm, "end": v(-11.14, 30.75) * mm});
            skLineSegment(sketch, "E261", {"start": v(-11.37, 35.05) * mm, "end": v(-13.2, 35.05) * mm});
            skLineSegment(sketch, "E262", {"start": v(-10.42, 34.66) * mm, "end": v(-9.34, 32.8) * mm});
            skLineSegment(sketch, "E263", {"start": v(-9.32, 32.18) * mm, "end": v(-10.38, 30.31) * mm});
            skLineSegment(sketch, "E264.0", {"start": v(-22.42, 28.46) * mm, "end": v(-24.4, 28.46) * mm});
            skLineSegment(sketch, "E264.1", {"start": v(-24.4, 28.46) * mm, "end": v(-25.4, 30.18) * mm});
            skLineSegment(sketch, "E264.2", {"start": v(-25.4, 30.18) * mm, "end": v(-24.4, 31.9) * mm});
            skLineSegment(sketch, "E264.3", {"start": v(-24.4, 31.9) * mm, "end": v(-22.42, 31.9) * mm});
            skLineSegment(sketch, "E264.4", {"start": v(-22.42, 31.9) * mm, "end": v(-21.42, 30.18) * mm});
            skLineSegment(sketch, "E264.5", {"start": v(-21.42, 30.18) * mm, "end": v(-22.42, 28.46) * mm});
            skLineSegment(sketch, "E265", {"start": v(-26.27, 29.95) * mm, "end": v(-25.27, 28.21) * mm});
            skLineSegment(sketch, "E266", {"start": v(-24.63, 27.58) * mm, "end": v(-22.34, 27.58) * mm});
            skLineSegment(sketch, "E267.0", {"start": v(-22.43, 32.77) * mm, "end": v(-24.4, 32.77) * mm});
            skLineSegment(sketch, "E267.1", {"start": v(-24.4, 32.77) * mm, "end": v(-25.4, 34.48) * mm});
            skLineSegment(sketch, "E267.2", {"start": v(-25.4, 34.48) * mm, "end": v(-24.47, 36.1) * mm});
            skLineSegment(sketch, "E267.4", {"start": v(-22.37, 36.1) * mm, "end": v(-21.43, 34.48) * mm});
            skLineSegment(sketch, "E267.5", {"start": v(-21.43, 34.48) * mm, "end": v(-22.43, 32.77) * mm});
            skLineSegment(sketch, "E268", {"start": v(-25.48, 36.1) * mm, "end": v(-26.05, 35.12) * mm});
            skLineSegment(sketch, "E269", {"start": v(-21.37, 36.1) * mm, "end": v(-20.7, 34.95) * mm});
            skLineSegment(sketch, "E270.0", {"start": v(-18.63, 26.34) * mm, "end": v(-20.61, 26.34) * mm});
            skLineSegment(sketch, "E270.1", {"start": v(-20.61, 26.34) * mm, "end": v(-21.6, 28.06) * mm});
            skLineSegment(sketch, "E270.2", {"start": v(-21.6, 28.06) * mm, "end": v(-20.62, 29.78) * mm});
            skLineSegment(sketch, "E270.3", {"start": v(-20.62, 29.78) * mm, "end": v(-18.63, 29.78) * mm});
            skLineSegment(sketch, "E270.4", {"start": v(-18.63, 29.78) * mm, "end": v(-17.64, 28.06) * mm});
            skLineSegment(sketch, "E270.5", {"start": v(-17.64, 28.06) * mm, "end": v(-18.63, 26.34) * mm});
            skLineSegment(sketch, "E271", {"start": v(-22.34, 27.58) * mm, "end": v(-21.33, 25.82) * mm});
            skLineSegment(sketch, "E272", {"start": v(-16.85, 27.69) * mm, "end": v(-17.84, 25.95) * mm});
            skLineSegment(sketch, "E273.0", {"start": v(-18.7, 30.65) * mm, "end": v(-20.62, 30.65) * mm});
            skLineSegment(sketch, "E273.1", {"start": v(-20.62, 30.65) * mm, "end": v(-21.62, 32.36) * mm});
            skLineSegment(sketch, "E273.2", {"start": v(-21.62, 32.36) * mm, "end": v(-20.62, 34.08) * mm});
            skLineSegment(sketch, "E273.3", {"start": v(-20.62, 34.08) * mm, "end": v(-18.64, 34.08) * mm});
            skLineSegment(sketch, "E273.4", {"start": v(-18.64, 34.08) * mm, "end": v(-17.7, 32.4) * mm});
            skLineSegment(sketch, "E274", {"start": v(-18.71, 34.95) * mm, "end": v(-20.7, 34.95) * mm});
            skLineSegment(sketch, "E275.0", {"start": v(-11.04, 17.8) * mm, "end": v(-13.03, 17.8) * mm});
            skLineSegment(sketch, "E275.1", {"start": v(-13.03, 17.8) * mm, "end": v(-14.02, 19.53) * mm});
            skLineSegment(sketch, "E275.2", {"start": v(-14.02, 19.53) * mm, "end": v(-13.03, 21.25) * mm});
            skLineSegment(sketch, "E275.3", {"start": v(-13.03, 21.25) * mm, "end": v(-11.04, 21.25) * mm});
            skLineSegment(sketch, "E275.4", {"start": v(-11.04, 21.25) * mm, "end": v(-10.05, 19.53) * mm});
            skLineSegment(sketch, "E275.5", {"start": v(-10.05, 19.53) * mm, "end": v(-11.04, 17.8) * mm});
            skLineSegment(sketch, "E276", {"start": v(-13.82, 21.63) * mm, "end": v(-14.83, 19.89) * mm});
            skLineSegment(sketch, "E277", {"start": v(-12.97, 16.93) * mm, "end": v(-10.97, 16.93) * mm});
            skLineSegment(sketch, "E278.0", {"start": v(-11.05, 22.11) * mm, "end": v(-13.04, 22.11) * mm});
            skLineSegment(sketch, "E278.1", {"start": v(-13.04, 22.11) * mm, "end": v(-14.03, 23.83) * mm});
            skLineSegment(sketch, "E278.2", {"start": v(-14.03, 23.83) * mm, "end": v(-13.04, 25.55) * mm});
            skLineSegment(sketch, "E278.3", {"start": v(-13.04, 25.55) * mm, "end": v(-11.05, 25.55) * mm});
            skLineSegment(sketch, "E278.4", {"start": v(-11.05, 25.55) * mm, "end": v(-10.06, 23.83) * mm});
            skLineSegment(sketch, "E278.5", {"start": v(-10.06, 23.83) * mm, "end": v(-11.05, 22.11) * mm});
            skLineSegment(sketch, "E279", {"start": v(-13.83, 25.93) * mm, "end": v(-14.83, 24.19) * mm});
            skLineSegment(sketch, "E280", {"start": v(-10.34, 26.06) * mm, "end": v(-9.33, 24.3) * mm});
            skLineSegment(sketch, "E281.0", {"start": v(-7.26, 15.69) * mm, "end": v(-9.24, 15.69) * mm});
            skLineSegment(sketch, "E281.1", {"start": v(-9.24, 15.69) * mm, "end": v(-10.23, 17.4) * mm});
            skLineSegment(sketch, "E281.2", {"start": v(-10.23, 17.4) * mm, "end": v(-9.24, 19.13) * mm});
            skLineSegment(sketch, "E281.3", {"start": v(-9.24, 19.13) * mm, "end": v(-7.26, 19.13) * mm});
            skLineSegment(sketch, "E281.4", {"start": v(-7.26, 19.13) * mm, "end": v(-6.26, 17.4) * mm});
            skLineSegment(sketch, "E281.5", {"start": v(-6.26, 17.4) * mm, "end": v(-7.26, 15.69) * mm});
            skLineSegment(sketch, "E282", {"start": v(-10.97, 16.93) * mm, "end": v(-10, 15.27) * mm});
            skLineSegment(sketch, "E283", {"start": v(-6.5, 19.55) * mm, "end": v(-5.54, 17.88) * mm});
            skLineSegment(sketch, "E284", {"start": v(-5.63, 16.77) * mm, "end": v(-6.47, 15.3) * mm});
            skLineSegment(sketch, "E285.0", {"start": v(-7.26, 20) * mm, "end": v(-9.25, 20) * mm});
            skLineSegment(sketch, "E285.1", {"start": v(-9.25, 20) * mm, "end": v(-10.24, 21.71) * mm});
            skLineSegment(sketch, "E285.2", {"start": v(-10.24, 21.71) * mm, "end": v(-9.25, 23.43) * mm});
            skLineSegment(sketch, "E285.3", {"start": v(-9.25, 23.43) * mm, "end": v(-7.27, 23.43) * mm});
            skLineSegment(sketch, "E285.4", {"start": v(-7.27, 23.43) * mm, "end": v(-6.27, 21.71) * mm});
            skLineSegment(sketch, "E285.5", {"start": v(-6.27, 21.71) * mm, "end": v(-7.26, 20) * mm});
            skLineSegment(sketch, "E286", {"start": v(-7.46, 24.3) * mm, "end": v(-9.33, 24.3) * mm});
            skLineSegment(sketch, "E287", {"start": v(-6.46, 23.76) * mm, "end": v(-5.47, 22.06) * mm});
            skLineSegment(sketch, "E288", {"start": v(-5.45, 21.4) * mm, "end": v(-6.5, 19.55) * mm});
            skLineSegment(sketch, "E289.1", {"start": v(-20.66, 17.94) * mm, "end": v(-21.52, 19.42) * mm});
            skLineSegment(sketch, "E289.2", {"start": v(-21.52, 19.42) * mm, "end": v(-20.52, 21.14) * mm});
            skLineSegment(sketch, "E289.3", {"start": v(-20.52, 21.14) * mm, "end": v(-18.54, 21.14) * mm});
            skLineSegment(sketch, "E289.4", {"start": v(-18.54, 21.14) * mm, "end": v(-17.55, 19.42) * mm});
            skLineSegment(sketch, "E289.5", {"start": v(-17.55, 19.42) * mm, "end": v(-18.4, 17.94) * mm});
            skLineSegment(sketch, "E290.0", {"start": v(-18.55, 22) * mm, "end": v(-20.53, 22) * mm});
            skLineSegment(sketch, "E290.1", {"start": v(-20.53, 22) * mm, "end": v(-21.52, 23.73) * mm});
            skLineSegment(sketch, "E290.2", {"start": v(-21.52, 23.73) * mm, "end": v(-20.53, 25.44) * mm});
            skLineSegment(sketch, "E290.3", {"start": v(-20.53, 25.44) * mm, "end": v(-18.55, 25.44) * mm});
            skLineSegment(sketch, "E290.4", {"start": v(-18.55, 25.44) * mm, "end": v(-17.56, 23.73) * mm});
            skLineSegment(sketch, "E290.5", {"start": v(-17.56, 23.73) * mm, "end": v(-18.55, 22) * mm});
            skLineSegment(sketch, "E291", {"start": v(-21.33, 25.82) * mm, "end": v(-22.17, 24.36) * mm});
            skLineSegment(sketch, "E292", {"start": v(-17.84, 25.95) * mm, "end": v(-16.82, 24.19) * mm});
            skLineSegment(sketch, "E293.0", {"start": v(-14.75, 15.58) * mm, "end": v(-16.74, 15.58) * mm});
            skLineSegment(sketch, "E293.1", {"start": v(-16.74, 15.58) * mm, "end": v(-17.73, 17.3) * mm});
            skLineSegment(sketch, "E293.2", {"start": v(-17.73, 17.3) * mm, "end": v(-16.74, 19.02) * mm});
            skLineSegment(sketch, "E293.3", {"start": v(-16.74, 19.02) * mm, "end": v(-14.75, 19.02) * mm});
            skLineSegment(sketch, "E293.4", {"start": v(-14.75, 19.02) * mm, "end": v(-13.76, 17.3) * mm});
            skLineSegment(sketch, "E293.5", {"start": v(-13.76, 17.3) * mm, "end": v(-14.75, 15.58) * mm});
            skLineSegment(sketch, "E294", {"start": v(-12.97, 16.93) * mm, "end": v(-13.96, 15.19) * mm});
            skLineSegment(sketch, "E295.0", {"start": v(-14.83, 19.89) * mm, "end": v(-16.75, 19.89) * mm});
            skLineSegment(sketch, "E295.1", {"start": v(-16.75, 19.89) * mm, "end": v(-17.74, 21.6) * mm});
            skLineSegment(sketch, "E295.2", {"start": v(-17.74, 21.6) * mm, "end": v(-16.75, 23.32) * mm});
            skLineSegment(sketch, "E295.3", {"start": v(-16.75, 23.32) * mm, "end": v(-14.76, 23.32) * mm});
            skLineSegment(sketch, "E295.4", {"start": v(-14.76, 23.32) * mm, "end": v(-13.82, 21.63) * mm});
            skLineSegment(sketch, "E296", {"start": v(-14.83, 24.19) * mm, "end": v(-16.82, 24.19) * mm});
            skLineSegment(sketch, "E297", {"start": v(-36.9, 15.14) * mm, "end": v(-35.85, 13.58) * mm});
            skLineSegment(sketch, "E298", {"start": v(-33.8, 13.58) * mm, "end": v(-32.73, 15.4) * mm});
            skLineSegment(sketch, "E299.0", {"start": v(4.14, 26.6) * mm, "end": v(2.16, 26.6) * mm});
            skLineSegment(sketch, "E299.1", {"start": v(2.16, 26.6) * mm, "end": v(1.16, 28.31) * mm});
            skLineSegment(sketch, "E299.2", {"start": v(1.16, 28.31) * mm, "end": v(2.15, 30.03) * mm});
            skLineSegment(sketch, "E299.3", {"start": v(2.15, 30.03) * mm, "end": v(4.14, 30.03) * mm});
            skLineSegment(sketch, "E299.4", {"start": v(4.14, 30.03) * mm, "end": v(5.13, 28.31) * mm});
            skLineSegment(sketch, "E299.5", {"start": v(5.13, 28.31) * mm, "end": v(4.14, 26.6) * mm});
            skLineSegment(sketch, "E300", {"start": v(1.36, 30.42) * mm, "end": v(0.36, 28.67) * mm});
            skLineSegment(sketch, "E301", {"start": v(2.21, 25.72) * mm, "end": v(4.21, 25.72) * mm});
            skLineSegment(sketch, "E302.0", {"start": v(4.13, 30.9) * mm, "end": v(2.15, 30.9) * mm});
            skLineSegment(sketch, "E302.1", {"start": v(2.15, 30.9) * mm, "end": v(1.16, 32.62) * mm});
            skLineSegment(sketch, "E302.2", {"start": v(1.16, 32.62) * mm, "end": v(2.15, 34.34) * mm});
            skLineSegment(sketch, "E302.3", {"start": v(2.15, 34.34) * mm, "end": v(4.13, 34.34) * mm});
            skLineSegment(sketch, "E302.4", {"start": v(4.13, 34.34) * mm, "end": v(5.12, 32.62) * mm});
            skLineSegment(sketch, "E302.5", {"start": v(5.12, 32.62) * mm, "end": v(4.13, 30.9) * mm});
            skLineSegment(sketch, "E303", {"start": v(4.14, 35.2) * mm, "end": v(2.24, 35.2) * mm});
            skLineSegment(sketch, "E304", {"start": v(1.36, 34.72) * mm, "end": v(0.35, 32.97) * mm});
            skLineSegment(sketch, "E305", {"start": v(4.85, 34.82) * mm, "end": v(5.86, 33.08) * mm});
            skLineSegment(sketch, "E306.0", {"start": v(7.93, 24.47) * mm, "end": v(5.94, 24.47) * mm});
            skLineSegment(sketch, "E306.1", {"start": v(5.94, 24.47) * mm, "end": v(4.95, 26.2) * mm});
            skLineSegment(sketch, "E306.2", {"start": v(4.95, 26.2) * mm, "end": v(5.94, 27.91) * mm});
            skLineSegment(sketch, "E306.3", {"start": v(5.94, 27.91) * mm, "end": v(7.93, 27.91) * mm});
            skLineSegment(sketch, "E306.4", {"start": v(7.93, 27.91) * mm, "end": v(8.92, 26.2) * mm});
            skLineSegment(sketch, "E306.5", {"start": v(8.92, 26.2) * mm, "end": v(7.93, 24.47) * mm});
            skLineSegment(sketch, "E307", {"start": v(4.21, 25.72) * mm, "end": v(5.23, 23.96) * mm});
            skLineSegment(sketch, "E308", {"start": v(8.68, 28.34) * mm, "end": v(9.68, 26.6) * mm});
            skLineSegment(sketch, "E309", {"start": v(9.75, 25.89) * mm, "end": v(8.72, 24.08) * mm});
            skLineSegment(sketch, "E310.0", {"start": v(7.92, 28.78) * mm, "end": v(5.93, 28.78) * mm});
            skLineSegment(sketch, "E310.1", {"start": v(5.93, 28.78) * mm, "end": v(4.94, 30.5) * mm});
            skLineSegment(sketch, "E310.2", {"start": v(4.94, 30.5) * mm, "end": v(5.93, 32.22) * mm});
            skLineSegment(sketch, "E310.3", {"start": v(5.93, 32.22) * mm, "end": v(7.92, 32.22) * mm});
            skLineSegment(sketch, "E310.4", {"start": v(7.92, 32.22) * mm, "end": v(8.91, 30.5) * mm});
            skLineSegment(sketch, "E310.5", {"start": v(8.91, 30.5) * mm, "end": v(7.92, 28.78) * mm});
            skLineSegment(sketch, "E311", {"start": v(7.74, 33.08) * mm, "end": v(5.86, 33.08) * mm});
            skLineSegment(sketch, "E312", {"start": v(8.62, 32.73) * mm, "end": v(9.7, 30.87) * mm});
            skLineSegment(sketch, "E313", {"start": v(9.63, 30) * mm, "end": v(8.68, 28.34) * mm});
            skLineSegment(sketch, "E314.0", {"start": v(-3.36, 26.49) * mm, "end": v(-5.34, 26.49) * mm});
            skLineSegment(sketch, "E314.1", {"start": v(-5.34, 26.49) * mm, "end": v(-6.33, 28.2) * mm});
            skLineSegment(sketch, "E314.2", {"start": v(-6.33, 28.2) * mm, "end": v(-5.34, 29.93) * mm});
            skLineSegment(sketch, "E314.3", {"start": v(-5.34, 29.93) * mm, "end": v(-3.36, 29.93) * mm});
            skLineSegment(sketch, "E314.4", {"start": v(-3.36, 29.93) * mm, "end": v(-2.36, 28.2) * mm});
            skLineSegment(sketch, "E314.5", {"start": v(-2.36, 28.2) * mm, "end": v(-3.36, 26.49) * mm});
            skLineSegment(sketch, "E315", {"start": v(-6.1, 30.35) * mm, "end": v(-7.1, 28.64) * mm});
            skLineSegment(sketch, "E316", {"start": v(-7.02, 27.64) * mm, "end": v(-6.1, 26.06) * mm});
            skLineSegment(sketch, "E317", {"start": v(-5.25, 25.6) * mm, "end": v(-3.28, 25.6) * mm});
            skLineSegment(sketch, "E318.0", {"start": v(-3.36, 30.8) * mm, "end": v(-5.35, 30.8) * mm});
            skLineSegment(sketch, "E318.1", {"start": v(-5.35, 30.8) * mm, "end": v(-6.34, 32.51) * mm});
            skLineSegment(sketch, "E318.2", {"start": v(-6.34, 32.51) * mm, "end": v(-5.35, 34.23) * mm});
            skLineSegment(sketch, "E318.3", {"start": v(-5.35, 34.23) * mm, "end": v(-3.37, 34.23) * mm});
            skLineSegment(sketch, "E318.4", {"start": v(-3.37, 34.23) * mm, "end": v(-2.37, 32.51) * mm});
            skLineSegment(sketch, "E318.5", {"start": v(-2.37, 32.51) * mm, "end": v(-3.36, 30.8) * mm});
            skLineSegment(sketch, "E319", {"start": v(-3.45, 35.1) * mm, "end": v(-5.3, 35.1) * mm});
            skLineSegment(sketch, "E320", {"start": v(-6.12, 34.64) * mm, "end": v(-7.2, 32.8) * mm});
            skLineSegment(sketch, "E321", {"start": v(-7.16, 32.18) * mm, "end": v(-6.1, 30.35) * mm});
            skLineSegment(sketch, "E322", {"start": v(-2.59, 34.62) * mm, "end": v(-1.64, 32.97) * mm});
            skLineSegment(sketch, "E323.0", {"start": v(0.43, 24.37) * mm, "end": v(-1.55, 24.37) * mm});
            skLineSegment(sketch, "E323.1", {"start": v(-1.55, 24.37) * mm, "end": v(-2.55, 26.09) * mm});
            skLineSegment(sketch, "E323.2", {"start": v(-2.55, 26.09) * mm, "end": v(-1.56, 27.8) * mm});
            skLineSegment(sketch, "E323.3", {"start": v(-1.56, 27.8) * mm, "end": v(0.43, 27.8) * mm});
            skLineSegment(sketch, "E323.4", {"start": v(0.43, 27.8) * mm, "end": v(1.42, 26.09) * mm});
            skLineSegment(sketch, "E323.5", {"start": v(1.42, 26.09) * mm, "end": v(0.43, 24.37) * mm});
            skLineSegment(sketch, "E324", {"start": v(-3.28, 25.6) * mm, "end": v(-2.27, 23.85) * mm});
            skLineSegment(sketch, "E325", {"start": v(2.21, 25.72) * mm, "end": v(1.22, 23.97) * mm});
            skLineSegment(sketch, "E326.0", {"start": v(0.36, 28.67) * mm, "end": v(-1.56, 28.67) * mm});
            skLineSegment(sketch, "E326.1", {"start": v(-1.56, 28.67) * mm, "end": v(-2.55, 30.39) * mm});
            skLineSegment(sketch, "E326.2", {"start": v(-2.55, 30.39) * mm, "end": v(-1.56, 32.1) * mm});
            skLineSegment(sketch, "E326.3", {"start": v(-1.56, 32.1) * mm, "end": v(0.42, 32.1) * mm});
            skLineSegment(sketch, "E326.4", {"start": v(0.42, 32.1) * mm, "end": v(1.36, 30.42) * mm});
            skLineSegment(sketch, "E327", {"start": v(0.35, 32.97) * mm, "end": v(-1.64, 32.97) * mm});
            skLineSegment(sketch, "E328.0", {"start": v(8.02, 15.84) * mm, "end": v(6.03, 15.84) * mm});
            skLineSegment(sketch, "E328.1", {"start": v(6.03, 15.84) * mm, "end": v(5.04, 17.55) * mm});
            skLineSegment(sketch, "E328.2", {"start": v(5.04, 17.55) * mm, "end": v(6.03, 19.27) * mm});
            skLineSegment(sketch, "E328.3", {"start": v(6.03, 19.27) * mm, "end": v(8.02, 19.27) * mm});
            skLineSegment(sketch, "E328.4", {"start": v(8.02, 19.27) * mm, "end": v(9, 17.55) * mm});
            skLineSegment(sketch, "E328.5", {"start": v(9, 17.55) * mm, "end": v(8.02, 15.84) * mm});
            skLineSegment(sketch, "E329", {"start": v(5.24, 19.66) * mm, "end": v(4.23, 17.91) * mm});
            skLineSegment(sketch, "E330", {"start": v(6.09, 14.96) * mm, "end": v(8.1, 14.96) * mm});
            skLineSegment(sketch, "E331.0", {"start": v(8, 20.14) * mm, "end": v(6.02, 20.14) * mm});
            skLineSegment(sketch, "E331.1", {"start": v(6.02, 20.14) * mm, "end": v(5.03, 21.86) * mm});
            skLineSegment(sketch, "E331.2", {"start": v(5.03, 21.86) * mm, "end": v(6.02, 23.58) * mm});
            skLineSegment(sketch, "E331.3", {"start": v(6.02, 23.58) * mm, "end": v(8, 23.58) * mm});
            skLineSegment(sketch, "E331.4", {"start": v(8, 23.58) * mm, "end": v(9, 21.86) * mm});
            skLineSegment(sketch, "E331.5", {"start": v(9, 21.86) * mm, "end": v(8, 20.14) * mm});
            skLineSegment(sketch, "E332", {"start": v(5.23, 23.96) * mm, "end": v(4.23, 22.21) * mm});
            skLineSegment(sketch, "E333", {"start": v(8.72, 24.08) * mm, "end": v(9.73, 22.32) * mm});
            skLineSegment(sketch, "E334.0", {"start": v(11.8, 13.71) * mm, "end": v(9.82, 13.71) * mm});
            skLineSegment(sketch, "E334.1", {"start": v(9.82, 13.71) * mm, "end": v(8.83, 15.43) * mm});
            skLineSegment(sketch, "E334.2", {"start": v(8.83, 15.43) * mm, "end": v(9.82, 17.15) * mm});
            skLineSegment(sketch, "E334.3", {"start": v(9.82, 17.15) * mm, "end": v(11.8, 17.15) * mm});
            skLineSegment(sketch, "E334.4", {"start": v(11.8, 17.15) * mm, "end": v(12.8, 15.43) * mm});
            skLineSegment(sketch, "E334.5", {"start": v(12.8, 15.43) * mm, "end": v(11.8, 13.71) * mm});
            skLineSegment(sketch, "E335", {"start": v(8.1, 14.96) * mm, "end": v(9.05, 13.29) * mm});
            skLineSegment(sketch, "E336", {"start": v(12.56, 17.58) * mm, "end": v(13.58, 15.8) * mm});
            skLineSegment(sketch, "E337.0", {"start": v(11.8, 18.02) * mm, "end": v(9.81, 18.02) * mm});
            skLineSegment(sketch, "E337.1", {"start": v(9.81, 18.02) * mm, "end": v(8.82, 19.74) * mm});
            skLineSegment(sketch, "E337.2", {"start": v(8.82, 19.74) * mm, "end": v(9.81, 21.46) * mm});
            skLineSegment(sketch, "E337.3", {"start": v(9.81, 21.46) * mm, "end": v(11.8, 21.46) * mm});
            skLineSegment(sketch, "E337.4", {"start": v(11.8, 21.46) * mm, "end": v(12.79, 19.74) * mm});
            skLineSegment(sketch, "E337.5", {"start": v(12.79, 19.74) * mm, "end": v(11.8, 18.02) * mm});
            skLineSegment(sketch, "E338", {"start": v(11.82, 22.32) * mm, "end": v(9.73, 22.32) * mm});
            skLineSegment(sketch, "E339", {"start": v(12.46, 22.04) * mm, "end": v(13.54, 20.17) * mm});
            skLineSegment(sketch, "E340", {"start": v(13.65, 19.49) * mm, "end": v(12.56, 17.58) * mm});
            skLineSegment(sketch, "E341.0", {"start": v(0.52, 15.73) * mm, "end": v(-1.46, 15.73) * mm});
            skLineSegment(sketch, "E341.1", {"start": v(-1.46, 15.73) * mm, "end": v(-2.46, 17.45) * mm});
            skLineSegment(sketch, "E341.2", {"start": v(-2.46, 17.45) * mm, "end": v(-1.46, 19.17) * mm});
            skLineSegment(sketch, "E341.3", {"start": v(-1.46, 19.17) * mm, "end": v(0.52, 19.17) * mm});
            skLineSegment(sketch, "E341.4", {"start": v(0.52, 19.17) * mm, "end": v(1.51, 17.45) * mm});
            skLineSegment(sketch, "E341.5", {"start": v(1.51, 17.45) * mm, "end": v(0.52, 15.73) * mm});
            skLineSegment(sketch, "E342", {"start": v(-2.23, 19.6) * mm, "end": v(-3.22, 17.88) * mm});
            skLineSegment(sketch, "E343", {"start": v(-3.08, 16.77) * mm, "end": v(-2.21, 15.27) * mm});
            skLineSegment(sketch, "E344", {"start": v(-1.36, 14.85) * mm, "end": v(0.6, 14.85) * mm});
            skLineSegment(sketch, "E345.0", {"start": v(0.51, 20.03) * mm, "end": v(-1.47, 20.03) * mm});
            skLineSegment(sketch, "E345.1", {"start": v(-1.47, 20.03) * mm, "end": v(-2.46, 21.75) * mm});
            skLineSegment(sketch, "E345.2", {"start": v(-2.46, 21.75) * mm, "end": v(-1.47, 23.47) * mm});
            skLineSegment(sketch, "E345.3", {"start": v(-1.47, 23.47) * mm, "end": v(0.51, 23.47) * mm});
            skLineSegment(sketch, "E345.4", {"start": v(0.51, 23.47) * mm, "end": v(1.5, 21.75) * mm});
            skLineSegment(sketch, "E345.5", {"start": v(1.5, 21.75) * mm, "end": v(0.51, 20.03) * mm});
            skLineSegment(sketch, "E346", {"start": v(-2.27, 23.85) * mm, "end": v(-3.3, 22.06) * mm});
            skLineSegment(sketch, "E347", {"start": v(-3.28, 21.4) * mm, "end": v(-2.23, 19.6) * mm});
            skLineSegment(sketch, "E348", {"start": v(1.22, 23.97) * mm, "end": v(2.24, 22.21) * mm});
            skLineSegment(sketch, "E349.0", {"start": v(4.3, 13.6) * mm, "end": v(2.32, 13.6) * mm});
            skLineSegment(sketch, "E349.1", {"start": v(2.32, 13.6) * mm, "end": v(1.33, 15.33) * mm});
            skLineSegment(sketch, "E349.2", {"start": v(1.33, 15.33) * mm, "end": v(2.32, 17.05) * mm});
            skLineSegment(sketch, "E349.3", {"start": v(2.32, 17.05) * mm, "end": v(4.3, 17.05) * mm});
            skLineSegment(sketch, "E349.4", {"start": v(4.3, 17.05) * mm, "end": v(5.3, 15.33) * mm});
            skLineSegment(sketch, "E349.5", {"start": v(5.3, 15.33) * mm, "end": v(4.3, 13.6) * mm});
            skLineSegment(sketch, "E350", {"start": v(0.6, 14.85) * mm, "end": v(1.49, 13.3) * mm});
            skLineSegment(sketch, "E351", {"start": v(6.09, 14.96) * mm, "end": v(5.06, 13.15) * mm});
            skLineSegment(sketch, "E352.0", {"start": v(4.23, 17.91) * mm, "end": v(2.32, 17.91) * mm});
            skLineSegment(sketch, "E352.1", {"start": v(2.32, 17.91) * mm, "end": v(1.32, 19.63) * mm});
            skLineSegment(sketch, "E352.2", {"start": v(1.32, 19.63) * mm, "end": v(2.31, 21.35) * mm});
            skLineSegment(sketch, "E352.3", {"start": v(2.31, 21.35) * mm, "end": v(4.3, 21.35) * mm});
            skLineSegment(sketch, "E352.4", {"start": v(4.3, 21.35) * mm, "end": v(5.24, 19.66) * mm});
            skLineSegment(sketch, "E353", {"start": v(4.23, 22.21) * mm, "end": v(2.24, 22.21) * mm});
            skLineSegment(sketch, "E354", {"start": v(-31.85, 19.08) * mm, "end": v(-31.88, 19.08) * mm});
            skLineSegment(sketch, "E355", {"start": v(-22.4, 19.2) * mm, "end": v(-22.38, 19.2) * mm});
            skLineSegment(sketch, "E356", {"start": v(-22.37, 19.19) * mm, "end": v(-22.38, 19.2) * mm});
            skLineSegment(sketch, "E357.trimOffspring", {"start": v(24.28, 36.1) * mm, "end": v(65.28, 36.1) * mm});
            skLineSegment(sketch, "E358", {"start": v(-2.68, 8.89) * mm, "end": v(-2.3, 8.67) * mm});
            skLineSegment(sketch, "E359", {"start": v(-25.17, 19.57) * mm, "end": v(-25.17, 19.59) * mm});
            skLineSegment(sketch, "E360", {"start": v(-25.17, 19.6) * mm, "end": v(-25.17, 19.59) * mm});
            skLineSegment(sketch, "E361", {"start": v(-29.14, 19.6) * mm, "end": v(-29.16, 19.56) * mm});
            skLineSegment(sketch, "E362", {"start": v(24.28, 36.1) * mm, "end": v(-14.8, 36.1) * mm});
            skLineSegment(sketch, "E363.0", {"start": v(23.17, 24.71) * mm, "end": v(21.18, 24.71) * mm});
            skLineSegment(sketch, "E363.1", {"start": v(21.18, 24.71) * mm, "end": v(20.2, 26.43) * mm});
            skLineSegment(sketch, "E363.2", {"start": v(20.2, 26.43) * mm, "end": v(21.18, 28.15) * mm});
            skLineSegment(sketch, "E363.3", {"start": v(21.18, 28.15) * mm, "end": v(23.17, 28.15) * mm});
            skLineSegment(sketch, "E363.4", {"start": v(23.17, 28.15) * mm, "end": v(24.16, 26.43) * mm});
            skLineSegment(sketch, "E363.5", {"start": v(24.16, 26.43) * mm, "end": v(23.17, 24.71) * mm});
            skLineSegment(sketch, "E364", {"start": v(20.4, 28.54) * mm, "end": v(19.38, 26.79) * mm});
            skLineSegment(sketch, "E365", {"start": v(21.24, 23.83) * mm, "end": v(23.24, 23.83) * mm});
            skLineSegment(sketch, "E366.0", {"start": v(23.16, 29.02) * mm, "end": v(21.17, 29.02) * mm});
            skLineSegment(sketch, "E366.1", {"start": v(21.17, 29.02) * mm, "end": v(20.18, 30.73) * mm});
            skLineSegment(sketch, "E366.2", {"start": v(20.18, 30.73) * mm, "end": v(21.17, 32.45) * mm});
            skLineSegment(sketch, "E366.3", {"start": v(21.17, 32.45) * mm, "end": v(23.16, 32.45) * mm});
            skLineSegment(sketch, "E366.4", {"start": v(23.16, 32.45) * mm, "end": v(24.15, 30.73) * mm});
            skLineSegment(sketch, "E366.5", {"start": v(24.15, 30.73) * mm, "end": v(23.16, 29.02) * mm});
            skLineSegment(sketch, "E367", {"start": v(23.06, 33.32) * mm, "end": v(21.13, 33.32) * mm});
            skLineSegment(sketch, "E368", {"start": v(20.38, 32.83) * mm, "end": v(19.38, 31.1) * mm});
            skLineSegment(sketch, "E369", {"start": v(23.86, 32.97) * mm, "end": v(24.88, 31.2) * mm});
            skLineSegment(sketch, "E370.0", {"start": v(26.95, 22.6) * mm, "end": v(24.97, 22.6) * mm});
            skLineSegment(sketch, "E370.1", {"start": v(24.97, 22.6) * mm, "end": v(23.98, 24.3) * mm});
            skLineSegment(sketch, "E370.2", {"start": v(23.98, 24.3) * mm, "end": v(24.97, 26.03) * mm});
            skLineSegment(sketch, "E370.3", {"start": v(24.97, 26.03) * mm, "end": v(26.95, 26.03) * mm});
            skLineSegment(sketch, "E370.4", {"start": v(26.95, 26.03) * mm, "end": v(27.95, 24.3) * mm});
            skLineSegment(sketch, "E370.5", {"start": v(27.95, 24.3) * mm, "end": v(26.95, 22.6) * mm});
            skLineSegment(sketch, "E371", {"start": v(23.24, 23.83) * mm, "end": v(24.26, 22.07) * mm});
            skLineSegment(sketch, "E372", {"start": v(27.7, 26.45) * mm, "end": v(28.68, 24.77) * mm});
            skLineSegment(sketch, "E373", {"start": v(28.81, 24.08) * mm, "end": v(27.74, 22.2) * mm});
            skLineSegment(sketch, "E374.0", {"start": v(26.95, 26.9) * mm, "end": v(24.96, 26.9) * mm});
            skLineSegment(sketch, "E374.1", {"start": v(24.96, 26.9) * mm, "end": v(23.97, 28.61) * mm});
            skLineSegment(sketch, "E374.2", {"start": v(23.97, 28.61) * mm, "end": v(24.96, 30.33) * mm});
            skLineSegment(sketch, "E374.3", {"start": v(24.96, 30.33) * mm, "end": v(26.94, 30.33) * mm});
            skLineSegment(sketch, "E374.4", {"start": v(26.94, 30.33) * mm, "end": v(27.94, 28.61) * mm});
            skLineSegment(sketch, "E374.5", {"start": v(27.94, 28.61) * mm, "end": v(26.95, 26.9) * mm});
            skLineSegment(sketch, "E375", {"start": v(26.95, 31.2) * mm, "end": v(24.88, 31.2) * mm});
            skLineSegment(sketch, "E376", {"start": v(27.66, 30.82) * mm, "end": v(28.78, 28.89) * mm});
            skLineSegment(sketch, "E377", {"start": v(28.66, 28.13) * mm, "end": v(27.7, 26.45) * mm});
            skLineSegment(sketch, "E378.0", {"start": v(15.67, 24.6) * mm, "end": v(13.69, 24.6) * mm});
            skLineSegment(sketch, "E378.1", {"start": v(13.69, 24.6) * mm, "end": v(12.7, 26.32) * mm});
            skLineSegment(sketch, "E378.2", {"start": v(12.7, 26.32) * mm, "end": v(13.69, 28.04) * mm});
            skLineSegment(sketch, "E378.3", {"start": v(13.69, 28.04) * mm, "end": v(15.67, 28.04) * mm});
            skLineSegment(sketch, "E378.4", {"start": v(15.67, 28.04) * mm, "end": v(16.66, 26.32) * mm});
            skLineSegment(sketch, "E378.5", {"start": v(16.66, 26.32) * mm, "end": v(15.67, 24.6) * mm});
            skLineSegment(sketch, "E379", {"start": v(12.92, 28.47) * mm, "end": v(11.84, 26.6) * mm});
            skLineSegment(sketch, "E380", {"start": v(11.93, 25.89) * mm, "end": v(13, 24.06) * mm});
            skLineSegment(sketch, "E381", {"start": v(13.46, 23.73) * mm, "end": v(15.74, 23.73) * mm});
            skLineSegment(sketch, "E382.0", {"start": v(15.66, 28.9) * mm, "end": v(13.68, 28.9) * mm});
            skLineSegment(sketch, "E382.1", {"start": v(13.68, 28.9) * mm, "end": v(12.69, 30.63) * mm});
            skLineSegment(sketch, "E382.2", {"start": v(12.69, 30.63) * mm, "end": v(13.68, 32.35) * mm});
            skLineSegment(sketch, "E382.3", {"start": v(13.68, 32.35) * mm, "end": v(15.66, 32.35) * mm});
            skLineSegment(sketch, "E382.4", {"start": v(15.66, 32.35) * mm, "end": v(16.65, 30.63) * mm});
            skLineSegment(sketch, "E382.5", {"start": v(16.65, 30.63) * mm, "end": v(15.66, 28.9) * mm});
            skLineSegment(sketch, "E383", {"start": v(15.5, 33.21) * mm, "end": v(13.57, 33.21) * mm});
            skLineSegment(sketch, "E384", {"start": v(12.9, 32.74) * mm, "end": v(11.81, 30.87) * mm});
            skLineSegment(sketch, "E385", {"start": v(12.04, 30) * mm, "end": v(12.92, 28.47) * mm});
            skLineSegment(sketch, "E386", {"start": v(16.38, 32.83) * mm, "end": v(17.39, 31.1) * mm});
            skLineSegment(sketch, "E387.0", {"start": v(19.46, 22.48) * mm, "end": v(17.47, 22.48) * mm});
            skLineSegment(sketch, "E387.1", {"start": v(17.47, 22.48) * mm, "end": v(16.48, 24.2) * mm});
            skLineSegment(sketch, "E387.2", {"start": v(16.48, 24.2) * mm, "end": v(17.47, 25.92) * mm});
            skLineSegment(sketch, "E387.3", {"start": v(17.47, 25.92) * mm, "end": v(19.46, 25.92) * mm});
            skLineSegment(sketch, "E387.4", {"start": v(19.46, 25.92) * mm, "end": v(20.45, 24.2) * mm});
            skLineSegment(sketch, "E387.5", {"start": v(20.45, 24.2) * mm, "end": v(19.46, 22.48) * mm});
            skLineSegment(sketch, "E388", {"start": v(15.74, 23.73) * mm, "end": v(16.76, 21.97) * mm});
            skLineSegment(sketch, "E389", {"start": v(21.24, 23.83) * mm, "end": v(20.25, 22.1) * mm});
            skLineSegment(sketch, "E390.0", {"start": v(19.38, 26.79) * mm, "end": v(17.46, 26.79) * mm});
            skLineSegment(sketch, "E390.1", {"start": v(17.46, 26.79) * mm, "end": v(16.47, 28.5) * mm});
            skLineSegment(sketch, "E390.2", {"start": v(16.47, 28.5) * mm, "end": v(17.46, 30.23) * mm});
            skLineSegment(sketch, "E390.3", {"start": v(17.46, 30.23) * mm, "end": v(19.45, 30.23) * mm});
            skLineSegment(sketch, "E390.4", {"start": v(19.45, 30.23) * mm, "end": v(20.4, 28.54) * mm});
            skLineSegment(sketch, "E391", {"start": v(19.38, 31.1) * mm, "end": v(17.39, 31.1) * mm});
            skLineSegment(sketch, "E392.0", {"start": v(27.04, 13.95) * mm, "end": v(25.06, 13.95) * mm});
            skLineSegment(sketch, "E392.1", {"start": v(25.06, 13.95) * mm, "end": v(24.07, 15.67) * mm});
            skLineSegment(sketch, "E392.2", {"start": v(24.07, 15.67) * mm, "end": v(25.06, 17.4) * mm});
            skLineSegment(sketch, "E392.3", {"start": v(25.06, 17.4) * mm, "end": v(27.04, 17.4) * mm});
            skLineSegment(sketch, "E392.4", {"start": v(27.04, 17.4) * mm, "end": v(28.04, 15.67) * mm});
            skLineSegment(sketch, "E392.5", {"start": v(28.04, 15.67) * mm, "end": v(27.04, 13.95) * mm});
            skLineSegment(sketch, "E393", {"start": v(24.27, 17.78) * mm, "end": v(23.26, 16.03) * mm});
            skLineSegment(sketch, "E394.0", {"start": v(27.04, 18.26) * mm, "end": v(25.05, 18.26) * mm});
            skLineSegment(sketch, "E394.1", {"start": v(25.05, 18.26) * mm, "end": v(24.06, 19.97) * mm});
            skLineSegment(sketch, "E394.2", {"start": v(24.06, 19.97) * mm, "end": v(25.05, 21.7) * mm});
            skLineSegment(sketch, "E394.3", {"start": v(25.05, 21.7) * mm, "end": v(27.04, 21.7) * mm});
            skLineSegment(sketch, "E394.4", {"start": v(27.04, 21.7) * mm, "end": v(28.03, 19.97) * mm});
            skLineSegment(sketch, "E394.5", {"start": v(28.03, 19.97) * mm, "end": v(27.04, 18.26) * mm});
            skLineSegment(sketch, "E395", {"start": v(24.26, 22.07) * mm, "end": v(23.25, 20.33) * mm});
            skLineSegment(sketch, "E396", {"start": v(27.74, 22.2) * mm, "end": v(28.76, 20.44) * mm});
            skLineSegment(sketch, "E397.0", {"start": v(30.83, 11.83) * mm, "end": v(28.85, 11.83) * mm});
            skLineSegment(sketch, "E397.1", {"start": v(28.85, 11.83) * mm, "end": v(27.85, 13.55) * mm});
            skLineSegment(sketch, "E397.2", {"start": v(27.85, 13.55) * mm, "end": v(28.85, 15.27) * mm});
            skLineSegment(sketch, "E397.3", {"start": v(28.85, 15.27) * mm, "end": v(30.83, 15.27) * mm});
            skLineSegment(sketch, "E397.4", {"start": v(30.83, 15.27) * mm, "end": v(31.82, 13.55) * mm});
            skLineSegment(sketch, "E397.5", {"start": v(31.82, 13.55) * mm, "end": v(30.83, 11.83) * mm});
            skLineSegment(sketch, "E398", {"start": v(31.59, 15.7) * mm, "end": v(32.6, 13.93) * mm});
            skLineSegment(sketch, "E399.0", {"start": v(30.82, 16.14) * mm, "end": v(28.84, 16.14) * mm});
            skLineSegment(sketch, "E399.1", {"start": v(28.84, 16.14) * mm, "end": v(27.85, 17.85) * mm});
            skLineSegment(sketch, "E399.2", {"start": v(27.85, 17.85) * mm, "end": v(28.84, 19.57) * mm});
            skLineSegment(sketch, "E399.3", {"start": v(28.84, 19.57) * mm, "end": v(30.82, 19.57) * mm});
            skLineSegment(sketch, "E399.4", {"start": v(30.82, 19.57) * mm, "end": v(31.81, 17.85) * mm});
            skLineSegment(sketch, "E399.5", {"start": v(31.81, 17.85) * mm, "end": v(30.82, 16.14) * mm});
            skLineSegment(sketch, "E400", {"start": v(30.82, 20.44) * mm, "end": v(28.76, 20.44) * mm});
            skLineSegment(sketch, "E401", {"start": v(28.84, 15.26) * mm, "end": v(30.84, 15.26) * mm});
            skLineSegment(sketch, "E402", {"start": v(31.55, 20.05) * mm, "end": v(32.6, 18.22) * mm});
            skLineSegment(sketch, "E403", {"start": v(32.63, 17.53) * mm, "end": v(31.59, 15.7) * mm});
            skLineSegment(sketch, "E404.0", {"start": v(19.55, 13.85) * mm, "end": v(17.56, 13.85) * mm});
            skLineSegment(sketch, "E404.1", {"start": v(17.56, 13.85) * mm, "end": v(16.57, 15.56) * mm});
            skLineSegment(sketch, "E404.2", {"start": v(16.57, 15.56) * mm, "end": v(17.56, 17.28) * mm});
            skLineSegment(sketch, "E404.3", {"start": v(17.56, 17.28) * mm, "end": v(19.55, 17.28) * mm});
            skLineSegment(sketch, "E404.4", {"start": v(19.55, 17.28) * mm, "end": v(20.54, 15.56) * mm});
            skLineSegment(sketch, "E404.5", {"start": v(20.54, 15.56) * mm, "end": v(19.55, 13.85) * mm});
            skLineSegment(sketch, "E405", {"start": v(16.8, 17.71) * mm, "end": v(15.7, 15.8) * mm});
            skLineSegment(sketch, "E406.0", {"start": v(19.54, 18.15) * mm, "end": v(17.56, 18.15) * mm});
            skLineSegment(sketch, "E406.1", {"start": v(17.56, 18.15) * mm, "end": v(16.56, 19.87) * mm});
            skLineSegment(sketch, "E406.2", {"start": v(16.56, 19.87) * mm, "end": v(17.55, 21.59) * mm});
            skLineSegment(sketch, "E406.3", {"start": v(17.55, 21.59) * mm, "end": v(19.54, 21.59) * mm});
            skLineSegment(sketch, "E406.4", {"start": v(19.54, 21.59) * mm, "end": v(20.53, 19.87) * mm});
            skLineSegment(sketch, "E406.5", {"start": v(20.53, 19.87) * mm, "end": v(19.54, 18.15) * mm});
            skLineSegment(sketch, "E407", {"start": v(16.76, 21.97) * mm, "end": v(15.72, 20.17) * mm});
            skLineSegment(sketch, "E408", {"start": v(15.77, 19.49) * mm, "end": v(16.8, 17.71) * mm});
            skLineSegment(sketch, "E409", {"start": v(20.25, 22.1) * mm, "end": v(21.26, 20.33) * mm});
            skLineSegment(sketch, "E410.0", {"start": v(23.33, 11.73) * mm, "end": v(21.35, 11.73) * mm});
            skLineSegment(sketch, "E410.1", {"start": v(21.35, 11.73) * mm, "end": v(20.36, 13.44) * mm});
            skLineSegment(sketch, "E410.2", {"start": v(20.36, 13.44) * mm, "end": v(21.35, 15.16) * mm});
            skLineSegment(sketch, "E410.3", {"start": v(21.35, 15.16) * mm, "end": v(23.33, 15.16) * mm});
            skLineSegment(sketch, "E410.4", {"start": v(23.33, 15.16) * mm, "end": v(24.33, 13.44) * mm});
            skLineSegment(sketch, "E410.5", {"start": v(24.33, 13.44) * mm, "end": v(23.33, 11.73) * mm});
            skLineSegment(sketch, "E411.0", {"start": v(23.26, 16.03) * mm, "end": v(21.34, 16.03) * mm});
            skLineSegment(sketch, "E411.1", {"start": v(21.34, 16.03) * mm, "end": v(20.35, 17.75) * mm});
            skLineSegment(sketch, "E411.2", {"start": v(20.35, 17.75) * mm, "end": v(21.34, 19.47) * mm});
            skLineSegment(sketch, "E411.3", {"start": v(21.34, 19.47) * mm, "end": v(23.33, 19.47) * mm});
            skLineSegment(sketch, "E411.4", {"start": v(23.33, 19.47) * mm, "end": v(24.27, 17.78) * mm});
            skLineSegment(sketch, "E412", {"start": v(23.25, 20.33) * mm, "end": v(21.26, 20.33) * mm});
            skLineSegment(sketch, "E413", {"start": v(21.34, 15.15) * mm, "end": v(23.34, 15.15) * mm});
            skLineSegment(sketch, "E414.0", {"start": v(42.19, 27.05) * mm, "end": v(40.2, 27.05) * mm});
            skLineSegment(sketch, "E414.1", {"start": v(40.2, 27.05) * mm, "end": v(39.21, 28.77) * mm});
            skLineSegment(sketch, "E414.2", {"start": v(39.21, 28.77) * mm, "end": v(40.2, 30.48) * mm});
            skLineSegment(sketch, "E414.3", {"start": v(40.2, 30.48) * mm, "end": v(42.19, 30.48) * mm});
            skLineSegment(sketch, "E414.4", {"start": v(42.19, 30.48) * mm, "end": v(43.18, 28.77) * mm});
            skLineSegment(sketch, "E414.5", {"start": v(43.18, 28.77) * mm, "end": v(42.19, 27.05) * mm});
            skLineSegment(sketch, "E415", {"start": v(39.41, 30.87) * mm, "end": v(38.4, 29.12) * mm});
            skLineSegment(sketch, "E416", {"start": v(40.26, 26.17) * mm, "end": v(42.26, 26.17) * mm});
            skLineSegment(sketch, "E417.0", {"start": v(42.18, 31.35) * mm, "end": v(40.2, 31.35) * mm});
            skLineSegment(sketch, "E417.1", {"start": v(40.2, 31.35) * mm, "end": v(39.2, 33.07) * mm});
            skLineSegment(sketch, "E417.2", {"start": v(39.2, 33.07) * mm, "end": v(40.2, 34.79) * mm});
            skLineSegment(sketch, "E417.3", {"start": v(40.2, 34.79) * mm, "end": v(42.18, 34.79) * mm});
            skLineSegment(sketch, "E417.4", {"start": v(42.18, 34.79) * mm, "end": v(43.17, 33.07) * mm});
            skLineSegment(sketch, "E417.5", {"start": v(43.17, 33.07) * mm, "end": v(42.18, 31.35) * mm});
            skLineSegment(sketch, "E418", {"start": v(41.99, 35.65) * mm, "end": v(40.33, 35.65) * mm});
            skLineSegment(sketch, "E419", {"start": v(39.4, 35.17) * mm, "end": v(38.4, 33.43) * mm});
            skLineSegment(sketch, "E420", {"start": v(42.97, 35.14) * mm, "end": v(43.9, 33.53) * mm});
            skLineSegment(sketch, "E421.0", {"start": v(45.97, 24.93) * mm, "end": v(44, 24.93) * mm});
            skLineSegment(sketch, "E421.1", {"start": v(44, 24.93) * mm, "end": v(43, 26.64) * mm});
            skLineSegment(sketch, "E421.2", {"start": v(43, 26.64) * mm, "end": v(43.99, 28.36) * mm});
            skLineSegment(sketch, "E421.3", {"start": v(43.99, 28.36) * mm, "end": v(45.97, 28.36) * mm});
            skLineSegment(sketch, "E421.4", {"start": v(45.97, 28.36) * mm, "end": v(46.97, 26.64) * mm});
            skLineSegment(sketch, "E421.5", {"start": v(46.97, 26.64) * mm, "end": v(45.97, 24.93) * mm});
            skLineSegment(sketch, "E422", {"start": v(42.26, 26.17) * mm, "end": v(43.28, 24.4) * mm});
            skLineSegment(sketch, "E423", {"start": v(47.55, 25.9) * mm, "end": v(46.77, 24.53) * mm});
            skLineSegment(sketch, "E424.0", {"start": v(45.97, 29.23) * mm, "end": v(43.98, 29.23) * mm});
            skLineSegment(sketch, "E424.1", {"start": v(43.98, 29.23) * mm, "end": v(42.99, 30.95) * mm});
            skLineSegment(sketch, "E424.2", {"start": v(42.99, 30.95) * mm, "end": v(43.98, 32.67) * mm});
            skLineSegment(sketch, "E424.3", {"start": v(43.98, 32.67) * mm, "end": v(45.97, 32.67) * mm});
            skLineSegment(sketch, "E424.4", {"start": v(45.97, 32.67) * mm, "end": v(46.96, 30.95) * mm});
            skLineSegment(sketch, "E424.5", {"start": v(46.96, 30.95) * mm, "end": v(45.97, 29.23) * mm});
            skLineSegment(sketch, "E425", {"start": v(46.31, 33.53) * mm, "end": v(43.9, 33.53) * mm});
            skLineSegment(sketch, "E426.0", {"start": v(34.7, 26.94) * mm, "end": v(32.7, 26.94) * mm});
            skLineSegment(sketch, "E426.1", {"start": v(32.7, 26.94) * mm, "end": v(31.72, 28.66) * mm});
            skLineSegment(sketch, "E426.2", {"start": v(31.72, 28.66) * mm, "end": v(32.7, 30.38) * mm});
            skLineSegment(sketch, "E426.3", {"start": v(32.7, 30.38) * mm, "end": v(34.7, 30.38) * mm});
            skLineSegment(sketch, "E426.4", {"start": v(34.7, 30.38) * mm, "end": v(35.68, 28.66) * mm});
            skLineSegment(sketch, "E426.5", {"start": v(35.68, 28.66) * mm, "end": v(34.7, 26.94) * mm});
            skLineSegment(sketch, "E427", {"start": v(31.94, 30.8) * mm, "end": v(30.83, 28.89) * mm});
            skLineSegment(sketch, "E428", {"start": v(31, 28.13) * mm, "end": v(32.03, 26.35) * mm});
            skLineSegment(sketch, "E429", {"start": v(32.7, 26.06) * mm, "end": v(34.76, 26.06) * mm});
            skLineSegment(sketch, "E430.0", {"start": v(34.68, 31.24) * mm, "end": v(32.7, 31.24) * mm});
            skLineSegment(sketch, "E430.1", {"start": v(32.7, 31.24) * mm, "end": v(31.7, 32.96) * mm});
            skLineSegment(sketch, "E430.2", {"start": v(31.7, 32.96) * mm, "end": v(32.7, 34.68) * mm});
            skLineSegment(sketch, "E430.3", {"start": v(32.7, 34.68) * mm, "end": v(34.68, 34.68) * mm});
            skLineSegment(sketch, "E430.4", {"start": v(34.68, 34.68) * mm, "end": v(35.68, 32.96) * mm});
            skLineSegment(sketch, "E430.5", {"start": v(35.68, 32.96) * mm, "end": v(34.68, 31.24) * mm});
            skLineSegment(sketch, "E431", {"start": v(34.57, 35.55) * mm, "end": v(32.72, 35.55) * mm});
            skLineSegment(sketch, "E432", {"start": v(31.97, 35.18) * mm, "end": v(30.9, 33.3) * mm});
            skLineSegment(sketch, "E433", {"start": v(30.9, 32.61) * mm, "end": v(31.94, 30.8) * mm});
            skLineSegment(sketch, "E434", {"start": v(32.7, 30.36) * mm, "end": v(34.7, 30.36) * mm});
            skLineSegment(sketch, "E435", {"start": v(35.4, 35.16) * mm, "end": v(36.4, 33.43) * mm});
            skLineSegment(sketch, "E436.0", {"start": v(38.48, 24.82) * mm, "end": v(36.5, 24.82) * mm});
            skLineSegment(sketch, "E436.1", {"start": v(36.5, 24.82) * mm, "end": v(35.5, 26.54) * mm});
            skLineSegment(sketch, "E436.2", {"start": v(35.5, 26.54) * mm, "end": v(36.5, 28.26) * mm});
            skLineSegment(sketch, "E436.3", {"start": v(36.5, 28.26) * mm, "end": v(38.48, 28.26) * mm});
            skLineSegment(sketch, "E436.4", {"start": v(38.48, 28.26) * mm, "end": v(39.47, 26.54) * mm});
            skLineSegment(sketch, "E436.5", {"start": v(39.47, 26.54) * mm, "end": v(38.48, 24.82) * mm});
            skLineSegment(sketch, "E437", {"start": v(34.76, 26.06) * mm, "end": v(35.78, 24.3) * mm});
            skLineSegment(sketch, "E438", {"start": v(40.26, 26.17) * mm, "end": v(39.27, 24.43) * mm});
            skLineSegment(sketch, "E439.0", {"start": v(38.4, 29.12) * mm, "end": v(36.49, 29.12) * mm});
            skLineSegment(sketch, "E439.1", {"start": v(36.49, 29.12) * mm, "end": v(35.5, 30.84) * mm});
            skLineSegment(sketch, "E439.2", {"start": v(35.5, 30.84) * mm, "end": v(36.48, 32.56) * mm});
            skLineSegment(sketch, "E439.3", {"start": v(36.48, 32.56) * mm, "end": v(38.47, 32.56) * mm});
            skLineSegment(sketch, "E439.4", {"start": v(38.47, 32.56) * mm, "end": v(39.41, 30.87) * mm});
            skLineSegment(sketch, "E440", {"start": v(38.4, 33.43) * mm, "end": v(36.4, 33.43) * mm});
            skLineSegment(sketch, "E441.0", {"start": v(46.07, 16.29) * mm, "end": v(44.08, 16.29) * mm});
            skLineSegment(sketch, "E441.1", {"start": v(44.08, 16.29) * mm, "end": v(43.09, 18) * mm});
            skLineSegment(sketch, "E441.2", {"start": v(43.09, 18) * mm, "end": v(44.08, 19.72) * mm});
            skLineSegment(sketch, "E441.3", {"start": v(44.08, 19.72) * mm, "end": v(46.06, 19.72) * mm});
            skLineSegment(sketch, "E441.4", {"start": v(46.06, 19.72) * mm, "end": v(47.06, 18) * mm});
            skLineSegment(sketch, "E441.5", {"start": v(47.06, 18) * mm, "end": v(46.07, 16.29) * mm});
            skLineSegment(sketch, "E442", {"start": v(43.3, 20.11) * mm, "end": v(42.28, 18.36) * mm});
            skLineSegment(sketch, "E443.0", {"start": v(46.06, 20.6) * mm, "end": v(44.07, 20.6) * mm});
            skLineSegment(sketch, "E443.1", {"start": v(44.07, 20.6) * mm, "end": v(43.08, 22.3) * mm});
            skLineSegment(sketch, "E443.2", {"start": v(43.08, 22.3) * mm, "end": v(44.07, 24.03) * mm});
            skLineSegment(sketch, "E443.3", {"start": v(44.07, 24.03) * mm, "end": v(46.06, 24.03) * mm});
            skLineSegment(sketch, "E443.4", {"start": v(46.06, 24.03) * mm, "end": v(47.05, 22.3) * mm});
            skLineSegment(sketch, "E443.5", {"start": v(47.05, 22.3) * mm, "end": v(46.06, 20.6) * mm});
            skLineSegment(sketch, "E444", {"start": v(43.28, 24.4) * mm, "end": v(42.27, 22.67) * mm});
            skLineSegment(sketch, "E445", {"start": v(46.77, 24.53) * mm, "end": v(47.78, 22.77) * mm});
            skLineSegment(sketch, "E446.0", {"start": v(49.85, 14.17) * mm, "end": v(47.87, 14.17) * mm});
            skLineSegment(sketch, "E446.1", {"start": v(47.87, 14.17) * mm, "end": v(46.88, 15.89) * mm});
            skLineSegment(sketch, "E446.2", {"start": v(46.88, 15.89) * mm, "end": v(47.87, 17.6) * mm});
            skLineSegment(sketch, "E446.3", {"start": v(47.87, 17.6) * mm, "end": v(49.85, 17.6) * mm});
            skLineSegment(sketch, "E446.4", {"start": v(49.85, 17.6) * mm, "end": v(50.84, 15.89) * mm});
            skLineSegment(sketch, "E446.5", {"start": v(50.84, 15.89) * mm, "end": v(49.85, 14.17) * mm});
            skLineSegment(sketch, "E447.0", {"start": v(49.84, 18.47) * mm, "end": v(47.86, 18.47) * mm});
            skLineSegment(sketch, "E447.1", {"start": v(47.86, 18.47) * mm, "end": v(46.87, 20.19) * mm});
            skLineSegment(sketch, "E447.2", {"start": v(46.87, 20.19) * mm, "end": v(47.86, 21.9) * mm});
            skLineSegment(sketch, "E447.3", {"start": v(47.86, 21.9) * mm, "end": v(49.84, 21.9) * mm});
            skLineSegment(sketch, "E447.4", {"start": v(49.84, 21.9) * mm, "end": v(50.84, 20.19) * mm});
            skLineSegment(sketch, "E447.5", {"start": v(50.84, 20.19) * mm, "end": v(49.84, 18.47) * mm});
            skLineSegment(sketch, "E448", {"start": v(50.19, 22.77) * mm, "end": v(47.78, 22.77) * mm});
            skLineSegment(sketch, "E449.0", {"start": v(38.57, 16.18) * mm, "end": v(36.59, 16.18) * mm});
            skLineSegment(sketch, "E449.1", {"start": v(36.59, 16.18) * mm, "end": v(35.6, 17.9) * mm});
            skLineSegment(sketch, "E449.2", {"start": v(35.6, 17.9) * mm, "end": v(36.58, 19.62) * mm});
            skLineSegment(sketch, "E449.3", {"start": v(36.58, 19.62) * mm, "end": v(38.57, 19.62) * mm});
            skLineSegment(sketch, "E449.4", {"start": v(38.57, 19.62) * mm, "end": v(39.56, 17.9) * mm});
            skLineSegment(sketch, "E449.5", {"start": v(39.56, 17.9) * mm, "end": v(38.57, 16.18) * mm});
            skLineSegment(sketch, "E450", {"start": v(35.82, 20.05) * mm, "end": v(34.76, 18.22) * mm});
            skLineSegment(sketch, "E451", {"start": v(34.8, 17.53) * mm, "end": v(35.83, 15.73) * mm});
            skLineSegment(sketch, "E452.0", {"start": v(38.56, 20.48) * mm, "end": v(36.58, 20.48) * mm});
            skLineSegment(sketch, "E452.1", {"start": v(36.58, 20.48) * mm, "end": v(35.58, 22.2) * mm});
            skLineSegment(sketch, "E452.2", {"start": v(35.58, 22.2) * mm, "end": v(36.58, 23.92) * mm});
            skLineSegment(sketch, "E452.3", {"start": v(36.58, 23.92) * mm, "end": v(38.56, 23.92) * mm});
            skLineSegment(sketch, "E452.4", {"start": v(38.56, 23.92) * mm, "end": v(39.55, 22.2) * mm});
            skLineSegment(sketch, "E452.5", {"start": v(39.55, 22.2) * mm, "end": v(38.56, 20.48) * mm});
            skLineSegment(sketch, "E453", {"start": v(35.78, 24.3) * mm, "end": v(34.84, 22.67) * mm});
            skLineSegment(sketch, "E454", {"start": v(34.74, 21.9) * mm, "end": v(35.82, 20.05) * mm});
            skLineSegment(sketch, "E455", {"start": v(36.58, 19.6) * mm, "end": v(38.58, 19.6) * mm});
            skLineSegment(sketch, "E456", {"start": v(39.27, 24.43) * mm, "end": v(40.29, 22.67) * mm});
            skLineSegment(sketch, "E457.0", {"start": v(42.36, 14.06) * mm, "end": v(40.37, 14.06) * mm});
            skLineSegment(sketch, "E457.1", {"start": v(40.37, 14.06) * mm, "end": v(39.38, 15.78) * mm});
            skLineSegment(sketch, "E457.2", {"start": v(39.38, 15.78) * mm, "end": v(40.37, 17.5) * mm});
            skLineSegment(sketch, "E457.3", {"start": v(40.37, 17.5) * mm, "end": v(42.35, 17.5) * mm});
            skLineSegment(sketch, "E457.4", {"start": v(42.35, 17.5) * mm, "end": v(43.35, 15.78) * mm});
            skLineSegment(sketch, "E457.5", {"start": v(43.35, 15.78) * mm, "end": v(42.36, 14.06) * mm});
            skLineSegment(sketch, "E458.0", {"start": v(42.28, 18.36) * mm, "end": v(40.36, 18.36) * mm});
            skLineSegment(sketch, "E458.1", {"start": v(40.36, 18.36) * mm, "end": v(39.37, 20.08) * mm});
            skLineSegment(sketch, "E458.2", {"start": v(39.37, 20.08) * mm, "end": v(40.36, 21.8) * mm});
            skLineSegment(sketch, "E458.3", {"start": v(40.36, 21.8) * mm, "end": v(42.35, 21.8) * mm});
            skLineSegment(sketch, "E458.4", {"start": v(42.35, 21.8) * mm, "end": v(43.3, 20.11) * mm});
            skLineSegment(sketch, "E459", {"start": v(42.27, 22.67) * mm, "end": v(40.29, 22.67) * mm});
            skLineSegment(sketch, "E460", {"start": v(40.36, 17.48) * mm, "end": v(42.36, 17.48) * mm});
            skLineSegment(sketch, "E461.0", {"start": v(57.39, 26.9) * mm, "end": v(55.4, 26.9) * mm});
            skLineSegment(sketch, "E461.1", {"start": v(55.4, 26.9) * mm, "end": v(54.41, 28.61) * mm});
            skLineSegment(sketch, "E461.2", {"start": v(54.41, 28.61) * mm, "end": v(55.4, 30.33) * mm});
            skLineSegment(sketch, "E461.3", {"start": v(55.4, 30.33) * mm, "end": v(57.39, 30.33) * mm});
            skLineSegment(sketch, "E461.4", {"start": v(57.39, 30.33) * mm, "end": v(58.38, 28.61) * mm});
            skLineSegment(sketch, "E461.5", {"start": v(58.38, 28.61) * mm, "end": v(57.39, 26.9) * mm});
            skLineSegment(sketch, "E462", {"start": v(54.61, 30.72) * mm, "end": v(53.6, 28.97) * mm});
            skLineSegment(sketch, "E463", {"start": v(55.46, 26.01) * mm, "end": v(57.46, 26.01) * mm});
            skLineSegment(sketch, "E464.0", {"start": v(57.38, 31.2) * mm, "end": v(55.4, 31.2) * mm});
            skLineSegment(sketch, "E464.1", {"start": v(55.4, 31.2) * mm, "end": v(54.4, 32.91) * mm});
            skLineSegment(sketch, "E464.2", {"start": v(54.4, 32.91) * mm, "end": v(55.4, 34.63) * mm});
            skLineSegment(sketch, "E464.3", {"start": v(55.4, 34.63) * mm, "end": v(57.38, 34.63) * mm});
            skLineSegment(sketch, "E464.4", {"start": v(57.38, 34.63) * mm, "end": v(58.37, 32.91) * mm});
            skLineSegment(sketch, "E464.5", {"start": v(58.37, 32.91) * mm, "end": v(57.38, 31.2) * mm});
            skLineSegment(sketch, "E465", {"start": v(57.33, 35.5) * mm, "end": v(55, 35.5) * mm});
            skLineSegment(sketch, "E466", {"start": v(54.38, 34.63) * mm, "end": v(53.6, 33.27) * mm});
            skLineSegment(sketch, "E467", {"start": v(58.12, 35.07) * mm, "end": v(59.1, 33.38) * mm});
            skLineSegment(sketch, "E468.0", {"start": v(61.17, 24.77) * mm, "end": v(59.19, 24.77) * mm});
            skLineSegment(sketch, "E468.1", {"start": v(59.19, 24.77) * mm, "end": v(58.2, 26.5) * mm});
            skLineSegment(sketch, "E468.2", {"start": v(58.2, 26.5) * mm, "end": v(59.19, 28.2) * mm});
            skLineSegment(sketch, "E468.3", {"start": v(59.19, 28.2) * mm, "end": v(61.17, 28.2) * mm});
            skLineSegment(sketch, "E468.4", {"start": v(61.17, 28.2) * mm, "end": v(62.17, 26.5) * mm});
            skLineSegment(sketch, "E468.5", {"start": v(62.17, 26.5) * mm, "end": v(61.17, 24.77) * mm});
            skLineSegment(sketch, "E469", {"start": v(57.46, 26.01) * mm, "end": v(58.48, 24.25) * mm});
            skLineSegment(sketch, "E470", {"start": v(61.93, 28.63) * mm, "end": v(62.8, 27.14) * mm});
            skLineSegment(sketch, "E471", {"start": v(62.85, 25.94) * mm, "end": v(61.96, 24.38) * mm});
            skLineSegment(sketch, "E472.0", {"start": v(61.17, 29.08) * mm, "end": v(59.18, 29.08) * mm});
            skLineSegment(sketch, "E472.1", {"start": v(59.18, 29.08) * mm, "end": v(58.19, 30.8) * mm});
            skLineSegment(sketch, "E472.2", {"start": v(58.19, 30.8) * mm, "end": v(59.18, 32.51) * mm});
            skLineSegment(sketch, "E472.3", {"start": v(59.18, 32.51) * mm, "end": v(61.16, 32.51) * mm});
            skLineSegment(sketch, "E472.4", {"start": v(61.16, 32.51) * mm, "end": v(62.16, 30.8) * mm});
            skLineSegment(sketch, "E472.5", {"start": v(62.16, 30.8) * mm, "end": v(61.17, 29.08) * mm});
            skLineSegment(sketch, "E473", {"start": v(61.02, 33.38) * mm, "end": v(59.1, 33.38) * mm});
            skLineSegment(sketch, "E474", {"start": v(62.02, 32.77) * mm, "end": v(62.9, 31.25) * mm});
            skLineSegment(sketch, "E475", {"start": v(62.87, 30.3) * mm, "end": v(61.93, 28.63) * mm});
            skLineSegment(sketch, "E476.0", {"start": v(49.9, 26.79) * mm, "end": v(47.9, 26.79) * mm});
            skLineSegment(sketch, "E476.1", {"start": v(47.9, 26.79) * mm, "end": v(46.91, 28.5) * mm});
            skLineSegment(sketch, "E476.2", {"start": v(46.91, 28.5) * mm, "end": v(47.9, 30.22) * mm});
            skLineSegment(sketch, "E476.3", {"start": v(47.9, 30.22) * mm, "end": v(49.9, 30.22) * mm});
            skLineSegment(sketch, "E476.4", {"start": v(49.9, 30.22) * mm, "end": v(50.88, 28.5) * mm});
            skLineSegment(sketch, "E476.5", {"start": v(50.88, 28.5) * mm, "end": v(49.9, 26.79) * mm});
            skLineSegment(sketch, "E477", {"start": v(47.55, 25.9) * mm, "end": v(49.96, 25.9) * mm});
            skLineSegment(sketch, "E478.0", {"start": v(49.88, 31.09) * mm, "end": v(47.9, 31.09) * mm});
            skLineSegment(sketch, "E478.1", {"start": v(47.9, 31.09) * mm, "end": v(46.9, 32.8) * mm});
            skLineSegment(sketch, "E478.2", {"start": v(46.9, 32.8) * mm, "end": v(47.9, 34.53) * mm});
            skLineSegment(sketch, "E478.3", {"start": v(47.9, 34.53) * mm, "end": v(49.88, 34.53) * mm});
            skLineSegment(sketch, "E478.4", {"start": v(49.88, 34.53) * mm, "end": v(50.87, 32.8) * mm});
            skLineSegment(sketch, "E478.5", {"start": v(50.87, 32.8) * mm, "end": v(49.88, 31.09) * mm});
            skLineSegment(sketch, "E479", {"start": v(49.9, 35.4) * mm, "end": v(47.78, 35.4) * mm});
            skLineSegment(sketch, "E480", {"start": v(47.12, 34.93) * mm, "end": v(46.31, 33.53) * mm});
            skLineSegment(sketch, "E481", {"start": v(50.68, 34.87) * mm, "end": v(51.6, 33.27) * mm});
            skLineSegment(sketch, "E482.0", {"start": v(53.68, 24.67) * mm, "end": v(51.7, 24.67) * mm});
            skLineSegment(sketch, "E482.1", {"start": v(51.7, 24.67) * mm, "end": v(50.7, 26.38) * mm});
            skLineSegment(sketch, "E482.2", {"start": v(50.7, 26.38) * mm, "end": v(51.7, 28.1) * mm});
            skLineSegment(sketch, "E482.3", {"start": v(51.7, 28.1) * mm, "end": v(53.68, 28.1) * mm});
            skLineSegment(sketch, "E482.4", {"start": v(53.68, 28.1) * mm, "end": v(54.67, 26.38) * mm});
            skLineSegment(sketch, "E482.5", {"start": v(54.67, 26.38) * mm, "end": v(53.68, 24.67) * mm});
            skLineSegment(sketch, "E483", {"start": v(49.96, 25.9) * mm, "end": v(50.98, 24.15) * mm});
            skLineSegment(sketch, "E484", {"start": v(55.46, 26.01) * mm, "end": v(54.47, 24.27) * mm});
            skLineSegment(sketch, "E485.0", {"start": v(53.6, 28.97) * mm, "end": v(51.68, 28.97) * mm});
            skLineSegment(sketch, "E485.1", {"start": v(51.68, 28.97) * mm, "end": v(50.7, 30.69) * mm});
            skLineSegment(sketch, "E485.2", {"start": v(50.7, 30.69) * mm, "end": v(51.68, 32.4) * mm});
            skLineSegment(sketch, "E485.3", {"start": v(51.68, 32.4) * mm, "end": v(53.67, 32.4) * mm});
            skLineSegment(sketch, "E485.4", {"start": v(53.67, 32.4) * mm, "end": v(54.61, 30.72) * mm});
            skLineSegment(sketch, "E486", {"start": v(53.6, 33.27) * mm, "end": v(51.6, 33.27) * mm});
            skLineSegment(sketch, "E487.0", {"start": v(61.27, 16.13) * mm, "end": v(59.28, 16.13) * mm});
            skLineSegment(sketch, "E487.1", {"start": v(59.28, 16.13) * mm, "end": v(58.29, 17.85) * mm});
            skLineSegment(sketch, "E487.2", {"start": v(58.29, 17.85) * mm, "end": v(59.28, 19.57) * mm});
            skLineSegment(sketch, "E487.3", {"start": v(59.28, 19.57) * mm, "end": v(61.26, 19.57) * mm});
            skLineSegment(sketch, "E487.4", {"start": v(61.26, 19.57) * mm, "end": v(62.26, 17.85) * mm});
            skLineSegment(sketch, "E487.5", {"start": v(62.26, 17.85) * mm, "end": v(61.27, 16.13) * mm});
            skLineSegment(sketch, "E488", {"start": v(58.49, 19.96) * mm, "end": v(57.48, 18.2) * mm});
            skLineSegment(sketch, "E489.0", {"start": v(61.26, 20.44) * mm, "end": v(59.27, 20.44) * mm});
            skLineSegment(sketch, "E489.1", {"start": v(59.27, 20.44) * mm, "end": v(58.28, 22.16) * mm});
            skLineSegment(sketch, "E489.2", {"start": v(58.28, 22.16) * mm, "end": v(59.27, 23.87) * mm});
            skLineSegment(sketch, "E489.3", {"start": v(59.27, 23.87) * mm, "end": v(61.26, 23.87) * mm});
            skLineSegment(sketch, "E489.4", {"start": v(61.26, 23.87) * mm, "end": v(62.25, 22.16) * mm});
            skLineSegment(sketch, "E489.5", {"start": v(62.25, 22.16) * mm, "end": v(61.26, 20.44) * mm});
            skLineSegment(sketch, "E490", {"start": v(58.48, 24.25) * mm, "end": v(57.47, 22.51) * mm});
            skLineSegment(sketch, "E491", {"start": v(61.96, 24.38) * mm, "end": v(62.98, 22.62) * mm});
            skLineSegment(sketch, "E492.0", {"start": v(65.05, 14.01) * mm, "end": v(63.07, 14.01) * mm});
            skLineSegment(sketch, "E492.1", {"start": v(63.07, 14.01) * mm, "end": v(62.08, 15.73) * mm});
            skLineSegment(sketch, "E492.2", {"start": v(62.08, 15.73) * mm, "end": v(63.07, 17.45) * mm});
            skLineSegment(sketch, "E492.3", {"start": v(63.07, 17.45) * mm, "end": v(65.05, 17.45) * mm});
            skLineSegment(sketch, "E492.4", {"start": v(65.05, 17.45) * mm, "end": v(65.28, 17.06) * mm});
            skLineSegment(sketch, "E492.5", {"start": v(65.28, 14.4) * mm, "end": v(65.05, 14.01) * mm});
            skLineSegment(sketch, "E493.0", {"start": v(65.04, 18.32) * mm, "end": v(63.06, 18.32) * mm});
            skLineSegment(sketch, "E493.1", {"start": v(63.06, 18.32) * mm, "end": v(62.07, 20.03) * mm});
            skLineSegment(sketch, "E493.2", {"start": v(62.07, 20.03) * mm, "end": v(63.06, 21.75) * mm});
            skLineSegment(sketch, "E493.3", {"start": v(63.06, 21.75) * mm, "end": v(65.04, 21.75) * mm});
            skLineSegment(sketch, "E493.4", {"start": v(65.04, 21.75) * mm, "end": v(65.28, 21.35) * mm});
            skLineSegment(sketch, "E493.5", {"start": v(65.28, 18.72) * mm, "end": v(65.04, 18.32) * mm});
            skLineSegment(sketch, "E494", {"start": v(64.8, 22.62) * mm, "end": v(62.98, 22.62) * mm});
            skLineSegment(sketch, "E495", {"start": v(63.06, 17.44) * mm, "end": v(65.06, 17.44) * mm});
            skLineSegment(sketch, "E496.0", {"start": v(53.77, 16.03) * mm, "end": v(51.78, 16.03) * mm});
            skLineSegment(sketch, "E496.1", {"start": v(51.78, 16.03) * mm, "end": v(50.8, 17.75) * mm});
            skLineSegment(sketch, "E496.2", {"start": v(50.8, 17.75) * mm, "end": v(51.78, 19.46) * mm});
            skLineSegment(sketch, "E496.3", {"start": v(51.78, 19.46) * mm, "end": v(53.77, 19.46) * mm});
            skLineSegment(sketch, "E496.4", {"start": v(53.77, 19.46) * mm, "end": v(54.76, 17.75) * mm});
            skLineSegment(sketch, "E496.5", {"start": v(54.76, 17.75) * mm, "end": v(53.77, 16.03) * mm});
            skLineSegment(sketch, "E497.0", {"start": v(53.76, 20.33) * mm, "end": v(51.78, 20.33) * mm});
            skLineSegment(sketch, "E497.1", {"start": v(51.78, 20.33) * mm, "end": v(50.78, 22.05) * mm});
            skLineSegment(sketch, "E497.2", {"start": v(50.78, 22.05) * mm, "end": v(51.78, 23.77) * mm});
            skLineSegment(sketch, "E497.3", {"start": v(51.78, 23.77) * mm, "end": v(53.76, 23.77) * mm});
            skLineSegment(sketch, "E497.4", {"start": v(53.76, 23.77) * mm, "end": v(54.75, 22.05) * mm});
            skLineSegment(sketch, "E497.5", {"start": v(54.75, 22.05) * mm, "end": v(53.76, 20.33) * mm});
            skLineSegment(sketch, "E498", {"start": v(50.98, 24.15) * mm, "end": v(50.19, 22.77) * mm});
            skLineSegment(sketch, "E499", {"start": v(54.47, 24.27) * mm, "end": v(55.49, 22.51) * mm});
            skLineSegment(sketch, "E500.0", {"start": v(57.56, 13.9) * mm, "end": v(55.57, 13.9) * mm});
            skLineSegment(sketch, "E500.1", {"start": v(55.57, 13.9) * mm, "end": v(54.58, 15.62) * mm});
            skLineSegment(sketch, "E500.2", {"start": v(54.58, 15.62) * mm, "end": v(55.57, 17.34) * mm});
            skLineSegment(sketch, "E500.3", {"start": v(55.57, 17.34) * mm, "end": v(57.55, 17.34) * mm});
            skLineSegment(sketch, "E500.4", {"start": v(57.55, 17.34) * mm, "end": v(58.55, 15.62) * mm});
            skLineSegment(sketch, "E500.5", {"start": v(58.55, 15.62) * mm, "end": v(57.56, 13.9) * mm});
            skLineSegment(sketch, "E501.0", {"start": v(57.48, 18.2) * mm, "end": v(55.56, 18.2) * mm});
            skLineSegment(sketch, "E501.1", {"start": v(55.56, 18.2) * mm, "end": v(54.57, 19.93) * mm});
            skLineSegment(sketch, "E501.2", {"start": v(54.57, 19.93) * mm, "end": v(55.56, 21.65) * mm});
            skLineSegment(sketch, "E501.3", {"start": v(55.56, 21.65) * mm, "end": v(57.55, 21.65) * mm});
            skLineSegment(sketch, "E501.4", {"start": v(57.55, 21.65) * mm, "end": v(58.49, 19.96) * mm});
            skLineSegment(sketch, "E502", {"start": v(57.47, 22.51) * mm, "end": v(55.49, 22.51) * mm});
            skLineSegment(sketch, "E503", {"start": v(55.56, 17.33) * mm, "end": v(57.56, 17.33) * mm});
            skLineSegment(sketch, "E504", {"start": v(62.8, 27.14) * mm, "end": v(64.83, 27.14) * mm});
            skLineSegment(sketch, "E505", {"start": v(62.87, 25.94) * mm, "end": v(64.75, 25.94) * mm});
            skLineSegment(sketch, "E506", {"start": v(62.9, 31.25) * mm, "end": v(64.79, 31.25) * mm});
            skLineSegment(sketch, "E507", {"start": v(62.87, 30.3) * mm, "end": v(64.82, 30.3) * mm});
            skLineSegment(sketch, "E508", {"start": v(64.85, 27.17) * mm, "end": v(65.28, 27.95) * mm});
            skLineSegment(sketch, "E509", {"start": v(64.82, 30.3) * mm, "end": v(65.28, 29.69) * mm});
            skLineSegment(sketch, "E510", {"start": v(64.82, 31.3) * mm, "end": v(65.28, 32.09) * mm});
            skLineSegment(sketch, "E511", {"start": v(62.02, 32.77) * mm, "end": v(63.1, 34.44) * mm});
            skLineSegment(sketch, "E512", {"start": v(61.06, 33.44) * mm, "end": v(62.18, 35.04) * mm});
            skLineSegment(sketch, "E513", {"start": v(63.1, 34.44) * mm, "end": v(64.56, 34.44) * mm});
            skLineSegment(sketch, "E514", {"start": v(64.55, 34.44) * mm, "end": v(65.28, 33.8) * mm});
            skLineSegment(sketch, "E515", {"start": v(61.06, 33.44) * mm, "end": v(61.02, 33.38) * mm});
            skLineSegment(sketch, "E516", {"start": v(64.82, 31.3) * mm, "end": v(64.79, 31.25) * mm});
            skLineSegment(sketch, "E517", {"start": v(64.85, 27.17) * mm, "end": v(64.83, 27.14) * mm});
            skLineSegment(sketch, "E518", {"start": v(64.75, 25.94) * mm, "end": v(65.28, 25.13) * mm});
            skLineSegment(sketch, "E519", {"start": v(65.28, 23.19) * mm, "end": v(64.83, 22.64) * mm});
            skLineSegment(sketch, "E520", {"start": v(64.83, 22.64) * mm, "end": v(64.8, 22.62) * mm});
            skLineSegment(sketch, "E521", {"start": v(64.5, 35.3) * mm, "end": v(65.23, 36.1) * mm});
            skLineSegment(sketch, "E522", {"start": v(64.5, 35.3) * mm, "end": v(63, 35.3) * mm});
            skLineSegment(sketch, "E523", {"start": v(62.99, 35.32) * mm, "end": v(62.4, 36.1) * mm});
            skPoint(sketch, "E524.orphan", {"position": v(64.18, 36.1) * mm});
            skLineSegment(sketch, "E525", {"start": v(62.99, 35.32) * mm, "end": v(63, 35.3) * mm});
            skLineSegment(sketch, "E526", {"start": v(62.18, 35.04) * mm, "end": v(61.46, 36.1) * mm});
            skLineSegment(sketch, "E527", {"start": v(58.12, 35.07) * mm, "end": v(58.97, 36.1) * mm});
            skLineSegment(sketch, "E528", {"start": v(57.33, 35.5) * mm, "end": v(57.9, 36.1) * mm});
            skLineSegment(sketch, "E529", {"start": v(54.38, 34.63) * mm, "end": v(53.37, 36.1) * mm});
            skLineSegment(sketch, "E530", {"start": v(54.91, 35.6) * mm, "end": v(54.5, 36.1) * mm});
            skLineSegment(sketch, "E531", {"start": v(50.74, 34.98) * mm, "end": v(51.42, 36.1) * mm});
            skLineSegment(sketch, "E532", {"start": v(50.25, 36.1) * mm, "end": v(49.9, 35.4) * mm});
            skLineSegment(sketch, "E533", {"start": v(47.46, 36.1) * mm, "end": v(47.78, 35.4) * mm});
            skLineSegment(sketch, "E534", {"start": v(46.29, 36.1) * mm, "end": v(47.12, 34.93) * mm});
            skLineSegment(sketch, "E535", {"start": v(42.97, 35.14) * mm, "end": v(43.67, 36.1) * mm});
            skLineSegment(sketch, "E536", {"start": v(42.35, 36.1) * mm, "end": v(41.99, 35.65) * mm});
            skLineSegment(sketch, "E537", {"start": v(40.08, 36.1) * mm, "end": v(40.33, 35.65) * mm});
            skLineSegment(sketch, "E538", {"start": v(38.96, 36.1) * mm, "end": v(39.4, 35.17) * mm});
            skLineSegment(sketch, "E539", {"start": v(35.4, 35.16) * mm, "end": v(35.8, 36.1) * mm});
            skLineSegment(sketch, "E540", {"start": v(34.88, 36.1) * mm, "end": v(34.57, 35.55) * mm});
            skLineSegment(sketch, "E541", {"start": v(31.97, 35.18) * mm, "end": v(31.54, 36.1) * mm});
            skLineSegment(sketch, "E542", {"start": v(32.4, 36.1) * mm, "end": v(32.72, 35.55) * mm});
            skLineSegment(sketch, "E543", {"start": v(-22.4, 15.76) * mm, "end": v(-22.37, 15.76) * mm});
            skLineSegment(sketch, "E544", {"start": v(50.74, 34.98) * mm, "end": v(50.68, 34.87) * mm});
            skLineSegment(sketch, "E545", {"start": v(-11.37, 35.05) * mm, "end": v(-10.64, 36.1) * mm});
            skLineSegment(sketch, "E546", {"start": v(-10.42, 34.66) * mm, "end": v(-9.62, 36.1) * mm});
            skLineSegment(sketch, "E547", {"start": v(-6.12, 34.64) * mm, "end": v(-6.9, 36.1) * mm});
            skLineSegment(sketch, "E548", {"start": v(-5.74, 36.1) * mm, "end": v(-5.3, 35.1) * mm});
            skLineSegment(sketch, "E549", {"start": v(-2.59, 34.62) * mm, "end": v(-1.65, 36.1) * mm});
            skLineSegment(sketch, "E550", {"start": v(-3.45, 35.1) * mm, "end": v(-2.72, 36.1) * mm});
            skLineSegment(sketch, "E551", {"start": v(2.24, 35.2) * mm, "end": v(1.63, 36.1) * mm});
            skLineSegment(sketch, "E552", {"start": v(-9.41, 28.64) * mm, "end": v(-7.1, 28.64) * mm});
            skLineSegment(sketch, "E553", {"start": v(1.36, 34.72) * mm, "end": v(0.62, 36.1) * mm});
            skLineSegment(sketch, "E554", {"start": v(4.85, 34.82) * mm, "end": v(5.77, 36.1) * mm});
            skLineSegment(sketch, "E555", {"start": v(4.14, 35.2) * mm, "end": v(4.73, 36.1) * mm});
            skLineSegment(sketch, "E556", {"start": v(-9.44, 27.64) * mm, "end": v(-7.02, 27.64) * mm});
            skLineSegment(sketch, "E557", {"start": v(-6.46, 23.76) * mm, "end": v(-5.25, 25.6) * mm});
            skLineSegment(sketch, "E558", {"start": v(-7.46, 24.3) * mm, "end": v(-6.1, 26.06) * mm});
            skLineSegment(sketch, "E559", {"start": v(-5.54, 17.88) * mm, "end": v(-3.22, 17.88) * mm});
            skLineSegment(sketch, "E560", {"start": v(-5.63, 16.77) * mm, "end": v(-3.08, 16.77) * mm});
            skLineSegment(sketch, "E561", {"start": v(-2.6, 13.04) * mm, "end": v(-1.36, 14.85) * mm});
            skLineSegment(sketch, "E562", {"start": v(-3.45, 13.63) * mm, "end": v(-2.21, 15.27) * mm});
            skLineSegment(sketch, "E563", {"start": v(1.49, 13.3) * mm, "end": v(0.72, 11.48) * mm});
            skLineSegment(sketch, "E564", {"start": v(5.06, 13.15) * mm, "end": v(6.04, 11.54) * mm});
            skLineSegment(sketch, "E565", {"start": v(9.05, 13.29) * mm, "end": v(8.16, 11.57) * mm});
            skLineSegment(sketch, "E566", {"start": v(13.58, 15.8) * mm, "end": v(15.7, 15.8) * mm});
            skLineSegment(sketch, "E567", {"start": v(-5.47, 22.06) * mm, "end": v(-3.3, 22.06) * mm});
            skLineSegment(sketch, "E568", {"start": v(-3.28, 21.4) * mm, "end": v(-5.45, 21.4) * mm});
            skLineSegment(sketch, "E569", {"start": v(-9.32, 32.18) * mm, "end": v(-7.16, 32.18) * mm});
            skLineSegment(sketch, "E570", {"start": v(-7.2, 32.8) * mm, "end": v(-9.34, 32.8) * mm});
            skLineSegment(sketch, "E571", {"start": v(-7.2, 32.8) * mm, "end": v(-7.2, 32.8) * mm});
            skLineSegment(sketch, "E572", {"start": v(9.63, 30) * mm, "end": v(12.04, 30) * mm});
            skLineSegment(sketch, "E573", {"start": v(9.68, 26.6) * mm, "end": v(11.84, 26.6) * mm});
            skLineSegment(sketch, "E574", {"start": v(9.74, 25.89) * mm, "end": v(11.93, 25.89) * mm});
            skLineSegment(sketch, "E575", {"start": v(13.46, 23.73) * mm, "end": v(12.46, 22.04) * mm});
            skLineSegment(sketch, "E576", {"start": v(11.88, 22.36) * mm, "end": v(13, 24.06) * mm});
            skLineSegment(sketch, "E577", {"start": v(11.88, 22.36) * mm, "end": v(11.82, 22.32) * mm});
            skLineSegment(sketch, "E578", {"start": v(13.62, 19.49) * mm, "end": v(15.77, 19.49) * mm});
            skLineSegment(sketch, "E579", {"start": v(13.54, 20.17) * mm, "end": v(15.72, 20.17) * mm});
            skLineSegment(sketch, "E580", {"start": v(9.7, 30.87) * mm, "end": v(11.81, 30.87) * mm});
            skLineSegment(sketch, "E581", {"start": v(28.78, 28.89) * mm, "end": v(30.83, 28.89) * mm});
            skLineSegment(sketch, "E582", {"start": v(32.63, 17.53) * mm, "end": v(34.8, 17.53) * mm});
            skLineSegment(sketch, "E583", {"start": v(34.76, 18.22) * mm, "end": v(32.6, 18.22) * mm});
            skLineSegment(sketch, "E584", {"start": v(34.74, 21.9) * mm, "end": v(32.58, 21.9) * mm});
            skLineSegment(sketch, "E585", {"start": v(34.84, 22.67) * mm, "end": v(32.32, 22.67) * mm});
            skLineSegment(sketch, "E586", {"start": v(31.73, 22.18) * mm, "end": v(30.78, 20.35) * mm});
            skLineSegment(sketch, "E587", {"start": v(28.68, 24.77) * mm, "end": v(30.98, 24.77) * mm});
            skLineSegment(sketch, "E588", {"start": v(31.55, 20.05) * mm, "end": v(32.58, 21.9) * mm});
            skLineSegment(sketch, "E589", {"start": v(28.81, 24.08) * mm, "end": v(30.83, 24.08) * mm});
            skLineSegment(sketch, "E590", {"start": v(31.57, 24.37) * mm, "end": v(32.7, 26.06) * mm});
            skLineSegment(sketch, "E591", {"start": v(30.98, 24.77) * mm, "end": v(32.03, 26.35) * mm});
            skLineSegment(sketch, "E592", {"start": v(31.57, 24.37) * mm, "end": v(32.32, 22.67) * mm});
            skLineSegment(sketch, "E593", {"start": v(30.83, 24.08) * mm, "end": v(31.73, 22.18) * mm});
            skLineSegment(sketch, "E594", {"start": v(54.91, 35.6) * mm, "end": v(55, 35.5) * mm});
            skLineSegment(sketch, "E595", {"start": v(28.66, 28.13) * mm, "end": v(31, 28.13) * mm});
            skLineSegment(sketch, "E596", {"start": v(62.87, 25.94) * mm, "end": v(62.85, 25.94) * mm});
            skLineSegment(sketch, "E597", {"start": v(30.9, 32.61) * mm, "end": v(28.6, 32.61) * mm});
            skLineSegment(sketch, "E598", {"start": v(30.9, 33.3) * mm, "end": v(28.74, 33.3) * mm});
            skLineSegment(sketch, "E599", {"start": v(27.88, 33) * mm, "end": v(26.95, 31.2) * mm});
            skLineSegment(sketch, "E600", {"start": v(27.66, 30.82) * mm, "end": v(28.6, 32.61) * mm});
            skLineSegment(sketch, "E601", {"start": v(27.88, 33) * mm, "end": v(26.84, 34.48) * mm});
            skLineSegment(sketch, "E602", {"start": v(23.86, 32.97) * mm, "end": v(24.84, 34.48) * mm});
            skLineSegment(sketch, "E603", {"start": v(23.06, 33.32) * mm, "end": v(24.3, 35.02) * mm});
            skLineSegment(sketch, "E604", {"start": v(24.87, 34.48) * mm, "end": v(26.84, 34.48) * mm});
            skLineSegment(sketch, "E605", {"start": v(26.8, 35.28) * mm, "end": v(27.26, 36.1) * mm});
            skLineSegment(sketch, "E606", {"start": v(25.05, 35.28) * mm, "end": v(24.57, 36.1) * mm});
            skLineSegment(sketch, "E607", {"start": v(24.87, 34.48) * mm, "end": v(24.84, 34.48) * mm});
            skLineSegment(sketch, "E608", {"start": v(25.05, 35.28) * mm, "end": v(26.8, 35.28) * mm});
            skLineSegment(sketch, "E609", {"start": v(27.48, 35.13) * mm, "end": v(28.14, 36.1) * mm});
            skLineSegment(sketch, "E610", {"start": v(23.4, 36.1) * mm, "end": v(24.3, 35.02) * mm});
            skLineSegment(sketch, "E611", {"start": v(27.48, 35.13) * mm, "end": v(28.74, 33.3) * mm});
            skLineSegment(sketch, "E612", {"start": v(8.62, 32.73) * mm, "end": v(9.8, 34.37) * mm});
            skLineSegment(sketch, "E613", {"start": v(7.74, 33.08) * mm, "end": v(9, 34.82) * mm});
            skLineSegment(sketch, "E614", {"start": v(12.9, 32.74) * mm, "end": v(11.65, 34.37) * mm});
            skLineSegment(sketch, "E615", {"start": v(13.57, 33.21) * mm, "end": v(12.44, 34.69) * mm});
            skLineSegment(sketch, "E616", {"start": v(9.8, 34.37) * mm, "end": v(11.65, 34.37) * mm});
            skLineSegment(sketch, "E617", {"start": v(15.5, 33.21) * mm, "end": v(16.47, 34.65) * mm});
            skLineSegment(sketch, "E618", {"start": v(17.47, 34.48) * mm, "end": v(16.38, 32.83) * mm});
            skLineSegment(sketch, "E619", {"start": v(12.44, 34.69) * mm, "end": v(13.33, 36.1) * mm});
            skLineSegment(sketch, "E620", {"start": v(15.33, 36.1) * mm, "end": v(16.47, 34.65) * mm});
            skLineSegment(sketch, "E621", {"start": v(21.13, 33.32) * mm, "end": v(19.98, 34.87) * mm});
            skLineSegment(sketch, "E622", {"start": v(19.08, 35.22) * mm, "end": v(17.27, 35.27) * mm});
            skLineSegment(sketch, "E623", {"start": v(20.38, 32.83) * mm, "end": v(19.12, 34.48) * mm});
            skLineSegment(sketch, "E624", {"start": v(19.12, 34.48) * mm, "end": v(17.47, 34.48) * mm});
            skLineSegment(sketch, "E625", {"start": v(19.98, 34.87) * mm, "end": v(20.74, 36.1) * mm});
            skLineSegment(sketch, "E626", {"start": v(19.08, 35.22) * mm, "end": v(19.74, 36.1) * mm});
            skLineSegment(sketch, "E627", {"start": v(17.27, 35.27) * mm, "end": v(16.73, 36.1) * mm});
            skLineSegment(sketch, "E628", {"start": v(10.13, 35.17) * mm, "end": v(11.71, 35.17) * mm});
            skLineSegment(sketch, "E629", {"start": v(11.71, 35.17) * mm, "end": v(12.37, 36.1) * mm});
            skLineSegment(sketch, "E630", {"start": v(9, 34.82) * mm, "end": v(8.2, 36.1) * mm});
            skLineSegment(sketch, "E631", {"start": v(10.13, 35.17) * mm, "end": v(9.9, 35.17) * mm});
            skLineSegment(sketch, "E632", {"start": v(9.9, 35.17) * mm, "end": v(9.24, 36.1) * mm});
            skLineSegment(sketch, "E633", {"start": v(32.6, 13.93) * mm, "end": v(34.94, 13.93) * mm});
            skLineSegment(sketch, "E634", {"start": v(35.83, 15.73) * mm, "end": v(34.94, 13.93) * mm});
            skLineSegment(sketch, "E635", {"start": v(0.89, 10.61) * mm, "end": v(2.05, 8.67) * mm});
            skLineSegment(sketch, "E636.trimOffspring", {"start": v(0.72, 11.48) * mm, "end": v(-1.45, 11.45) * mm});
            skLineSegment(sketch, "E637.trimOffspring", {"start": v(0.89, 10.61) * mm, "end": v(-1.71, 10.58) * mm});
            skLineSegment(sketch, "E638", {"start": v(-1.45, 11.45) * mm, "end": v(-1.68, 11.45) * mm});
            skLineSegment(sketch, "E639", {"start": v(5.47, 10.98) * mm, "end": v(4.46, 9.23) * mm});
            skLineSegment(sketch, "E640.0", {"start": v(4.46, 9.23) * mm, "end": v(2.54, 9.23) * mm});
            skLineSegment(sketch, "E640.1", {"start": v(2.54, 9.23) * mm, "end": v(1.55, 10.95) * mm});
            skLineSegment(sketch, "E640.2", {"start": v(1.55, 10.95) * mm, "end": v(2.54, 12.67) * mm});
            skLineSegment(sketch, "E640.3", {"start": v(2.54, 12.67) * mm, "end": v(4.53, 12.67) * mm});
            skLineSegment(sketch, "E640.4", {"start": v(4.53, 12.67) * mm, "end": v(5.47, 10.98) * mm});
            skLineSegment(sketch, "E641", {"start": v(12.75, 11.23) * mm, "end": v(11.74, 9.48) * mm});
            skLineSegment(sketch, "E642.0", {"start": v(11.74, 9.48) * mm, "end": v(9.82, 9.48) * mm});
            skLineSegment(sketch, "E642.1", {"start": v(9.82, 9.48) * mm, "end": v(8.83, 11.2) * mm});
            skLineSegment(sketch, "E642.2", {"start": v(8.83, 11.2) * mm, "end": v(9.82, 12.92) * mm});
            skLineSegment(sketch, "E642.3", {"start": v(9.82, 12.92) * mm, "end": v(11.8, 12.92) * mm});
            skLineSegment(sketch, "E642.4", {"start": v(11.8, 12.92) * mm, "end": v(12.75, 11.23) * mm});
            skLineSegment(sketch, "E643.trimOffspring", {"start": v(8.16, 11.57) * mm, "end": v(6.04, 11.54) * mm});
            skLineSegment(sketch, "E644", {"start": v(16.68, 13.32) * mm, "end": v(15.68, 11.57) * mm});
            skLineSegment(sketch, "E645.0", {"start": v(15.68, 11.57) * mm, "end": v(13.76, 11.57) * mm});
            skLineSegment(sketch, "E645.1", {"start": v(13.76, 11.57) * mm, "end": v(12.76, 13.3) * mm});
            skLineSegment(sketch, "E645.2", {"start": v(12.76, 13.3) * mm, "end": v(13.76, 15.01) * mm});
            skLineSegment(sketch, "E645.3", {"start": v(13.76, 15.01) * mm, "end": v(15.74, 15.01) * mm});
            skLineSegment(sketch, "E645.4", {"start": v(15.74, 15.01) * mm, "end": v(16.68, 13.32) * mm});
            skLineSegment(sketch, "E646", {"start": v(20.35, 11.21) * mm, "end": v(19.34, 9.47) * mm});
            skLineSegment(sketch, "E647.0", {"start": v(19.34, 9.47) * mm, "end": v(17.42, 9.47) * mm});
            skLineSegment(sketch, "E647.1", {"start": v(17.42, 9.47) * mm, "end": v(16.43, 11.19) * mm});
            skLineSegment(sketch, "E647.2", {"start": v(16.43, 11.19) * mm, "end": v(17.42, 12.9) * mm});
            skLineSegment(sketch, "E647.3", {"start": v(17.42, 12.9) * mm, "end": v(19.4, 12.9) * mm});
            skLineSegment(sketch, "E647.4", {"start": v(19.4, 12.9) * mm, "end": v(20.35, 11.21) * mm});
            skLineSegment(sketch, "E648", {"start": v(27.91, 11.36) * mm, "end": v(26.9, 9.61) * mm});
            skLineSegment(sketch, "E649.0", {"start": v(26.9, 9.61) * mm, "end": v(24.99, 9.61) * mm});
            skLineSegment(sketch, "E649.1", {"start": v(24.99, 9.61) * mm, "end": v(24, 11.33) * mm});
            skLineSegment(sketch, "E649.2", {"start": v(24, 11.33) * mm, "end": v(24.98, 13.05) * mm});
            skLineSegment(sketch, "E649.3", {"start": v(24.98, 13.05) * mm, "end": v(26.97, 13.05) * mm});
            skLineSegment(sketch, "E649.4", {"start": v(26.97, 13.05) * mm, "end": v(27.91, 11.36) * mm});
            skLineSegment(sketch, "E650", {"start": v(24.12, 9.17) * mm, "end": v(23.83, 8.67) * mm});
            skLineSegment(sketch, "E651.1", {"start": v(20.47, 8.67) * mm, "end": v(20.2, 9.14) * mm});
            skLineSegment(sketch, "E651.2", {"start": v(20.2, 9.14) * mm, "end": v(21.2, 10.86) * mm});
            skLineSegment(sketch, "E651.3", {"start": v(21.2, 10.86) * mm, "end": v(23.18, 10.86) * mm});
            skLineSegment(sketch, "E651.4", {"start": v(23.18, 10.86) * mm, "end": v(24.12, 9.17) * mm});
            skLineSegment(sketch, "E652", {"start": v(16.64, 8.98) * mm, "end": v(16.46, 8.67) * mm});
            skLineSegment(sketch, "E653.1", {"start": v(12.88, 8.67) * mm, "end": v(12.72, 8.95) * mm});
            skLineSegment(sketch, "E653.2", {"start": v(12.72, 8.95) * mm, "end": v(13.7, 10.67) * mm});
            skLineSegment(sketch, "E653.3", {"start": v(13.7, 10.67) * mm, "end": v(15.7, 10.67) * mm});
            skLineSegment(sketch, "E653.4", {"start": v(15.7, 10.67) * mm, "end": v(16.64, 8.98) * mm});
            skLineSegment(sketch, "E654", {"start": v(9.15, 8.93) * mm, "end": v(9, 8.67) * mm});
            skLineSegment(sketch, "E655.1", {"start": v(5.36, 8.67) * mm, "end": v(5.23, 8.9) * mm});
            skLineSegment(sketch, "E655.2", {"start": v(5.23, 8.9) * mm, "end": v(6.22, 10.62) * mm});
            skLineSegment(sketch, "E655.3", {"start": v(6.22, 10.62) * mm, "end": v(8.2, 10.62) * mm});
            skLineSegment(sketch, "E655.4", {"start": v(8.2, 10.62) * mm, "end": v(9.15, 8.93) * mm});
            skLineSegment(sketch, "E656", {"start": v(31.85, 8.88) * mm, "end": v(31.73, 8.67) * mm});
            skLineSegment(sketch, "E657.2", {"start": v(27.93, 8.85) * mm, "end": v(28.92, 10.57) * mm});
            skLineSegment(sketch, "E657.3", {"start": v(28.92, 10.57) * mm, "end": v(30.9, 10.57) * mm});
            skLineSegment(sketch, "E657.4", {"start": v(30.9, 10.57) * mm, "end": v(31.85, 8.88) * mm});
            skLineSegment(sketch, "E658", {"start": v(39.41, 13.3) * mm, "end": v(38.4, 11.55) * mm});
            skLineSegment(sketch, "E659.0", {"start": v(38.4, 11.55) * mm, "end": v(36.48, 11.55) * mm});
            skLineSegment(sketch, "E659.1", {"start": v(36.48, 11.55) * mm, "end": v(35.5, 13.27) * mm});
            skLineSegment(sketch, "E659.2", {"start": v(35.5, 13.27) * mm, "end": v(36.48, 15) * mm});
            skLineSegment(sketch, "E659.3", {"start": v(36.48, 15) * mm, "end": v(38.47, 15) * mm});
            skLineSegment(sketch, "E659.4", {"start": v(38.47, 15) * mm, "end": v(39.41, 13.3) * mm});
            skLineSegment(sketch, "E660", {"start": v(47, 13.54) * mm, "end": v(46, 11.8) * mm});
            skLineSegment(sketch, "E661.0", {"start": v(46, 11.8) * mm, "end": v(44.08, 11.8) * mm});
            skLineSegment(sketch, "E661.1", {"start": v(44.08, 11.8) * mm, "end": v(43.08, 13.51) * mm});
            skLineSegment(sketch, "E661.2", {"start": v(43.08, 13.51) * mm, "end": v(44.07, 15.23) * mm});
            skLineSegment(sketch, "E661.3", {"start": v(44.07, 15.23) * mm, "end": v(46.06, 15.23) * mm});
            skLineSegment(sketch, "E661.4", {"start": v(46.06, 15.23) * mm, "end": v(47, 13.54) * mm});
            skLineSegment(sketch, "E662", {"start": v(43.27, 11.4) * mm, "end": v(42.27, 9.66) * mm});
            skLineSegment(sketch, "E663.0", {"start": v(42.27, 9.66) * mm, "end": v(40.35, 9.66) * mm});
            skLineSegment(sketch, "E663.1", {"start": v(40.35, 9.66) * mm, "end": v(39.35, 11.38) * mm});
            skLineSegment(sketch, "E663.2", {"start": v(39.35, 11.38) * mm, "end": v(40.35, 13.1) * mm});
            skLineSegment(sketch, "E663.3", {"start": v(40.35, 13.1) * mm, "end": v(42.33, 13.1) * mm});
            skLineSegment(sketch, "E663.4", {"start": v(42.33, 13.1) * mm, "end": v(43.27, 11.4) * mm});
            skLineSegment(sketch, "E664", {"start": v(35.62, 11.43) * mm, "end": v(34.6, 9.69) * mm});
            skLineSegment(sketch, "E665.0", {"start": v(34.6, 9.69) * mm, "end": v(32.69, 9.69) * mm});
            skLineSegment(sketch, "E665.1", {"start": v(32.69, 9.69) * mm, "end": v(31.7, 11.4) * mm});
            skLineSegment(sketch, "E665.2", {"start": v(31.7, 11.4) * mm, "end": v(32.69, 13.12) * mm});
            skLineSegment(sketch, "E665.3", {"start": v(32.69, 13.12) * mm, "end": v(34.67, 13.12) * mm});
            skLineSegment(sketch, "E665.4", {"start": v(34.67, 13.12) * mm, "end": v(35.62, 11.43) * mm});
            skLineSegment(sketch, "E666", {"start": v(39.34, 8.98) * mm, "end": v(39.17, 8.67) * mm});
            skLineSegment(sketch, "E667.1", {"start": v(35.58, 8.67) * mm, "end": v(35.42, 8.95) * mm});
            skLineSegment(sketch, "E667.2", {"start": v(35.42, 8.95) * mm, "end": v(36.42, 10.67) * mm});
            skLineSegment(sketch, "E667.3", {"start": v(36.42, 10.67) * mm, "end": v(38.4, 10.67) * mm});
            skLineSegment(sketch, "E667.4", {"start": v(38.4, 10.67) * mm, "end": v(39.34, 8.98) * mm});
            skLineSegment(sketch, "E668", {"start": v(46.97, 9.58) * mm, "end": v(46.45, 8.67) * mm});
            skLineSegment(sketch, "E669.1", {"start": v(43.56, 8.67) * mm, "end": v(43.05, 9.55) * mm});
            skLineSegment(sketch, "E669.2", {"start": v(43.05, 9.55) * mm, "end": v(44.05, 11.27) * mm});
            skLineSegment(sketch, "E669.3", {"start": v(44.05, 11.27) * mm, "end": v(46.03, 11.27) * mm});
            skLineSegment(sketch, "E669.4", {"start": v(46.03, 11.27) * mm, "end": v(46.97, 9.58) * mm});
            skLineSegment(sketch, "E670", {"start": v(27.93, 8.85) * mm, "end": v(28.07, 8.67) * mm});
            skLineSegment(sketch, "E671", {"start": v(50.82, 11.67) * mm, "end": v(49.82, 9.93) * mm});
            skLineSegment(sketch, "E672.0", {"start": v(49.82, 9.93) * mm, "end": v(47.9, 9.93) * mm});
            skLineSegment(sketch, "E672.1", {"start": v(47.9, 9.93) * mm, "end": v(46.9, 11.64) * mm});
            skLineSegment(sketch, "E672.2", {"start": v(46.9, 11.64) * mm, "end": v(47.9, 13.36) * mm});
            skLineSegment(sketch, "E672.3", {"start": v(47.9, 13.36) * mm, "end": v(49.88, 13.36) * mm});
            skLineSegment(sketch, "E672.4", {"start": v(49.88, 13.36) * mm, "end": v(50.82, 11.67) * mm});
            skLineSegment(sketch, "E673", {"start": v(54.67, 13.63) * mm, "end": v(53.66, 11.89) * mm});
            skLineSegment(sketch, "E674.0", {"start": v(53.66, 11.89) * mm, "end": v(51.74, 11.89) * mm});
            skLineSegment(sketch, "E674.1", {"start": v(51.74, 11.89) * mm, "end": v(50.75, 13.6) * mm});
            skLineSegment(sketch, "E674.2", {"start": v(50.75, 13.6) * mm, "end": v(51.74, 15.32) * mm});
            skLineSegment(sketch, "E674.3", {"start": v(51.74, 15.32) * mm, "end": v(53.72, 15.32) * mm});
            skLineSegment(sketch, "E674.4", {"start": v(53.72, 15.32) * mm, "end": v(54.67, 13.63) * mm});
            skLineSegment(sketch, "E675", {"start": v(54.58, 9.42) * mm, "end": v(54.15, 8.67) * mm});
            skLineSegment(sketch, "E676.1", {"start": v(51.08, 8.67) * mm, "end": v(50.66, 9.4) * mm});
            skLineSegment(sketch, "E676.2", {"start": v(50.66, 9.4) * mm, "end": v(51.66, 11.11) * mm});
            skLineSegment(sketch, "E676.3", {"start": v(51.66, 11.11) * mm, "end": v(53.64, 11.11) * mm});
            skLineSegment(sketch, "E676.4", {"start": v(53.64, 11.11) * mm, "end": v(54.58, 9.42) * mm});
            skLineSegment(sketch, "E677", {"start": v(58.4, 11.45) * mm, "end": v(57.4, 9.7) * mm});
            skLineSegment(sketch, "E678.0", {"start": v(57.4, 9.7) * mm, "end": v(55.48, 9.7) * mm});
            skLineSegment(sketch, "E678.1", {"start": v(55.48, 9.7) * mm, "end": v(54.5, 11.42) * mm});
            skLineSegment(sketch, "E678.2", {"start": v(54.5, 11.42) * mm, "end": v(55.48, 13.14) * mm});
            skLineSegment(sketch, "E678.3", {"start": v(55.48, 13.14) * mm, "end": v(57.47, 13.14) * mm});
            skLineSegment(sketch, "E678.4", {"start": v(57.47, 13.14) * mm, "end": v(58.4, 11.45) * mm});
            skLineSegment(sketch, "E679", {"start": v(62.23, 13.65) * mm, "end": v(61.22, 11.9) * mm});
            skLineSegment(sketch, "E680.0", {"start": v(61.22, 11.9) * mm, "end": v(59.3, 11.9) * mm});
            skLineSegment(sketch, "E680.1", {"start": v(59.3, 11.9) * mm, "end": v(58.31, 13.63) * mm});
            skLineSegment(sketch, "E680.2", {"start": v(58.31, 13.63) * mm, "end": v(59.3, 15.34) * mm});
            skLineSegment(sketch, "E680.3", {"start": v(59.3, 15.34) * mm, "end": v(61.29, 15.34) * mm});
            skLineSegment(sketch, "E680.4", {"start": v(61.29, 15.34) * mm, "end": v(62.23, 13.65) * mm});
            skLineSegment(sketch, "E681", {"start": v(62.17, 9.47) * mm, "end": v(61.7, 8.67) * mm});
            skLineSegment(sketch, "E682.1", {"start": v(58.7, 8.67) * mm, "end": v(58.25, 9.45) * mm});
            skLineSegment(sketch, "E682.2", {"start": v(58.25, 9.45) * mm, "end": v(59.24, 11.17) * mm});
            skLineSegment(sketch, "E682.3", {"start": v(59.24, 11.17) * mm, "end": v(61.22, 11.17) * mm});
            skLineSegment(sketch, "E682.4", {"start": v(61.22, 11.17) * mm, "end": v(62.17, 9.47) * mm});
            skLineSegment(sketch, "E683", {"start": v(65.28, 10.7) * mm, "end": v(64.7, 9.71) * mm});
            skLineSegment(sketch, "E684.0", {"start": v(64.7, 9.71) * mm, "end": v(62.78, 9.71) * mm});
            skLineSegment(sketch, "E684.1", {"start": v(62.78, 9.71) * mm, "end": v(61.8, 11.43) * mm});
            skLineSegment(sketch, "E684.2", {"start": v(61.8, 11.43) * mm, "end": v(62.78, 13.15) * mm});
            skLineSegment(sketch, "E684.3", {"start": v(62.78, 13.15) * mm, "end": v(64.77, 13.15) * mm});
            skLineSegment(sketch, "E684.4", {"start": v(64.77, 13.15) * mm, "end": v(65.28, 12.23) * mm});
            skLineSegment(sketch, "E685", {"start": v(-69.72, 32.73) * mm, "end": v(-69.72, 31.87) * mm});
            skSolve(sketch);
        }
        {
            var Q0;
            {var subQ4=sQuery(id+"F0.wireOp",EDGE,"E1.right");Q0=makeQuery(id+"F0.imprint","IMPRINT",FACE,{"disambiguationData":[TD([[makeQuery(id+"F0.imprint","IMPRINT",EDGE,{"derivedFrom":subQ4}),-1.0]])]});}
            var Q1;
            {var subQ1=sQuery(id+"F0.wireOp",EDGE,"E5.right");Q1=makeQuery(id+"F0.imprint","IMPRINT",FACE,{"disambiguationData":[TD([[makeQuery(id+"F0.imprint","IMPRINT",EDGE,{"derivedFrom":subQ1}),1.0]])]});}
            var Q2;
            {var subQ1=sQuery(id+"F0.wireOp",EDGE,"E5.bottom");Q2=makeQuery(id+"F0.imprint","IMPRINT",FACE,{"disambiguationData":[TD([[makeQuery(id+"F0.imprint","IMPRINT",EDGE,{"derivedFrom":subQ1}),1.0]])]});}
            var Q3;
            Q3=makeQuery(id+"F0.imprint","IMPRINT",FACE,{"disambiguationData":[TD([[makeQuery(id+"F0.imprint","IMPRINT",EDGE,{"derivedFrom":sQuery(id+"F0.wireOp",EDGE,"E10.right")}),-1.0]])]});
            var Q4;
            {var subQ1=sQuery(id+"F0.wireOp",EDGE,"E3.top");Q4=makeQuery(id+"F0.imprint","IMPRINT",FACE,{"disambiguationData":[TD([[makeQuery(id+"F0.imprint","IMPRINT",EDGE,{"derivedFrom":subQ1}),-1.0]])]});}
            extrude(context, id + "F1", {"entities" : qUnion([Q0, Q1, Q2, Q3, Q4]), "depth" : 6 * mm});
        }
        {
            var Q0;
            {var subQ1=sQuery(id+"F0.wireOp",EDGE,"E3.top");Q0=makeQuery(id+"F0.imprint","IMPRINT",FACE,{"disambiguationData":[TD([[makeQuery(id+"F0.imprint","IMPRINT",EDGE,{"derivedFrom":subQ1}),-1.0]])]});}
            var Q1;
            {var subQ1=sQuery(id+"F0.wireOp",EDGE,"E5.bottom");Q1=makeQuery(id+"F0.imprint","IMPRINT",FACE,{"disambiguationData":[TD([[makeQuery(id+"F0.imprint","IMPRINT",EDGE,{"derivedFrom":subQ1}),1.0]])]});}
            extrude(context, id + "F2", {"entities" : qUnion([Q0, Q1]), "operationType" : NewBodyOperationType.REMOVE, "depth" : 2 * mm});
        }
        {
            var Q0;
            Q0=makeQuery(id+"F0.imprint","IMPRINT",FACE,{"disambiguationData":[TD([[makeQuery(id+"F0.imprint","IMPRINT",EDGE,{"derivedFrom":sQuery(id+"F0.wireOp",EDGE,"E10.right")}),-1.0]])]});
            extrude(context, id + "F3", {"entities" : qUnion([Q0]), "operationType" : NewBodyOperationType.ADD, "depth" : 8 * mm});
        }
        {
            var Q0;
            Q0=qCreatedBy(makeId("Top.planeOp"),FACE);
            var sketch = newSketch(context, id + "F4", { "sketchPlane" : qUnion([Q0])});
            skLineSegment(sketch, "E686.bottom", {"start": v(67.63, -6) * mm, "end": v(12.13, -6) * mm});
            skLineSegment(sketch, "E686.top", {"start": v(67.63, -2) * mm, "end": v(12.13, -2) * mm});
            skLineSegment(sketch, "E686.left", {"start": v(67.63, -6) * mm, "end": v(67.63, -2) * mm});
            skLineSegment(sketch, "E686.right", {"start": v(-75.37, -6) * mm, "end": v(-75.37, -2) * mm});
            skLineSegment(sketch, "E687", {"start": v(45.13, -6) * mm, "end": v(45.13, -2) * mm});
            skLineSegment(sketch, "E688", {"start": v(-52.87, -6) * mm, "end": v(-52.87, -2) * mm});
            skLineSegment(sketch, "E689", {"start": v(-52.87, -2) * mm, "end": v(-52.87, -4) * mm});
            skLineSegment(sketch, "E690", {"start": v(-42.87, -6) * mm, "end": v(-42.87, -2) * mm});
            skLineSegment(sketch, "E691", {"start": v(35.13, -6) * mm, "end": v(35.13, -2) * mm});
            skLineSegment(sketch, "E692", {"start": v(12.13, -6) * mm, "end": v(12.13, -2) * mm});
            skLineSegment(sketch, "E693", {"start": v(-19.87, -6) * mm, "end": v(-19.87, -2) * mm});
            skLineSegment(sketch, "E694", {"start": v(-19.87, -2) * mm, "end": v(-19.87, -4) * mm});
            skLineSegment(sketch, "E695.trimOffspring", {"start": v(-19.87, -6) * mm, "end": v(-75.37, -6) * mm});
            skLineSegment(sketch, "E696.trimOffspring", {"start": v(-19.87, -2) * mm, "end": v(-75.37, -2) * mm});
            skSolve(sketch);
        }
        {
            var Q0;
            {var subQ3=sQuery(id+"F4.wireOp",EDGE,"E686.right");Q0=makeQuery(id+"F4.imprint","IMPRINT",FACE,{"disambiguationData":[TD([[makeQuery(id+"F4.imprint","IMPRINT",EDGE,{"derivedFrom":subQ3}),-1.0]])]});}
            var Q1;
            {var subQ1=sQuery(id+"F4.wireOp",EDGE,"E690");Q1=makeQuery(id+"F4.imprint","IMPRINT",FACE,{"disambiguationData":[TD([[makeQuery(id+"F4.imprint","IMPRINT",EDGE,{"derivedFrom":subQ1}),-1.0]])]});}
            var Q2;
            {var subQ2=sQuery(id+"F4.wireOp",EDGE,"E691");Q2=makeQuery(id+"F4.imprint","IMPRINT",FACE,{"disambiguationData":[TD([[makeQuery(id+"F4.imprint","IMPRINT",EDGE,{"derivedFrom":subQ2}),1.0]])]});}
            var Q3;
            {var subQ0=sQuery(id+"F4.wireOp",EDGE,"E686.left");Q3=makeQuery(id+"F4.imprint","IMPRINT",FACE,{"disambiguationData":[TD([[makeQuery(id+"F4.imprint","IMPRINT",EDGE,{"derivedFrom":subQ0}),1.0]])]});}
            extrude(context, id + "F5", {"entities" : qUnion([Q0, Q1, Q2, Q3]), "operationType" : NewBodyOperationType.REMOVE, "depth" : 5 * mm});
        }
        {
            var Q0;
            Q0=makeQuery(id+"F0.imprint","IMPRINT",FACE,{"disambiguationData":[TD([[makeQuery(id+"F0.imprint","IMPRINT",EDGE,{"derivedFrom":sQuery(id+"F0.wireOp",EDGE,"E37.0")}),1.0]])]});
            extrude(context, id + "F6", {"entities" : qUnion([Q0]), "operationType" : NewBodyOperationType.ADD, "depth" : 3 * mm});
        }
    });
